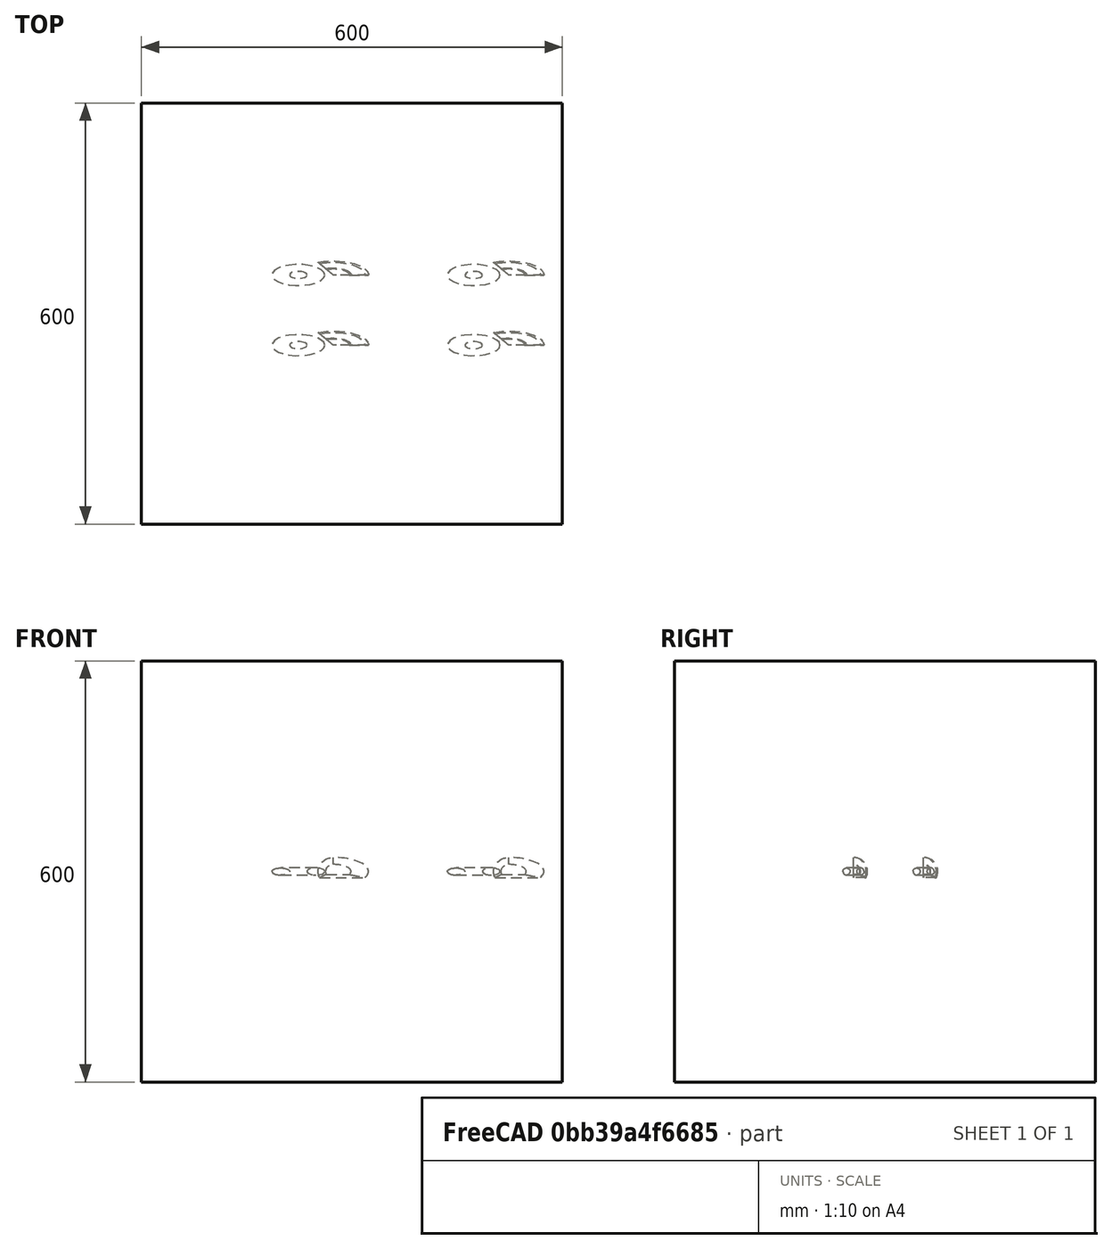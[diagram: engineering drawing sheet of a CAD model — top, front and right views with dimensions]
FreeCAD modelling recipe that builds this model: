
FCSTD DOCUMENT  (FreeCAD 1.0R39109 (Git))
Label: arrayTest-6_scaled
License: All rights reserved
LicenseURL: http://en.wikipedia.org/wiki/All_rights_reserved
objects: App::DocumentObjectGroupPython×1248, Part::FeaturePython×5, App::Part×2, Part::MultiFuse×1
note: 6 computed .brp shape members not serialized (recipe doc carries the construction recipe); baked Part::Feature solids carry a one-line shape summary decoded from their .brp

FEATURE [App::DocumentObjectGroupPython] HALFPI  # scripted group (container) (typed FeaturePython)
  name = HALFPI
  value = pi/2.
FEATURE [App::DocumentObjectGroupPython] PI  # scripted group (container) (typed FeaturePython)
  name = PI
  value = 1.*pi
FEATURE [App::DocumentObjectGroupPython] TWOPI  # scripted group (container) (typed FeaturePython)
  name = TWOPI
  value = 2.*pi
FEATURE [App::DocumentObjectGroupPython] Constants  # scripted group (container) (typed FeaturePython)
  Group = -> [HALFPI,PI,TWOPI]
FEATURE [App::DocumentObjectGroupPython] Variables  # scripted group (container) (typed FeaturePython)
FEATURE [App::DocumentObjectGroupPython] Quantities  # scripted group (container) (typed FeaturePython)
FEATURE [App::DocumentObjectGroupPython] Isotopes  # scripted group (container) (typed FeaturePython)
FEATURE [App::DocumentObjectGroupPython] Elements  # scripted group (container) (typed FeaturePython)
FEATURE [App::DocumentObjectGroupPython] G4Isotopes  # scripted group (container) (typed FeaturePython)
FEATURE [App::DocumentObjectGroupPython] H_element  # scripted group (container) (typed FeaturePython)
  Z = 1
  atom_value = 1.008
  formula = H
  name = H_element
FEATURE [App::DocumentObjectGroupPython] He_element  # scripted group (container) (typed FeaturePython)
  Z = 2
  atom_value = 4.0026
  formula = He
  name = He_element
FEATURE [App::DocumentObjectGroupPython] Li_element  # scripted group (container) (typed FeaturePython)
  Z = 3
  atom_value = 6.94
  formula = Li
  name = Li_element
FEATURE [App::DocumentObjectGroupPython] Be_element  # scripted group (container) (typed FeaturePython)
  Z = 4
  atom_value = 9.01218
  formula = Be
  name = Be_element
FEATURE [App::DocumentObjectGroupPython] B_element  # scripted group (container) (typed FeaturePython)
  Z = 5
  atom_value = 10.81
  formula = B
  name = B_element
FEATURE [App::DocumentObjectGroupPython] C_element  # scripted group (container) (typed FeaturePython)
  Z = 6
  atom_value = 12.011
  formula = C
  name = C_element
FEATURE [App::DocumentObjectGroupPython] N_element  # scripted group (container) (typed FeaturePython)
  Z = 7
  atom_value = 14.007
  formula = N
  name = N_element
FEATURE [App::DocumentObjectGroupPython] O_element  # scripted group (container) (typed FeaturePython)
  Z = 8
  atom_value = 15.999
  formula = O
  name = O_element
FEATURE [App::DocumentObjectGroupPython] F_element  # scripted group (container) (typed FeaturePython)
  Z = 9
  atom_value = 18.9984
  formula = F
  name = F_element
FEATURE [App::DocumentObjectGroupPython] Ne_element  # scripted group (container) (typed FeaturePython)
  Z = 10
  atom_value = 20.1797
  formula = Ne
  name = Ne_element
FEATURE [App::DocumentObjectGroupPython] Na_element  # scripted group (container) (typed FeaturePython)
  Z = 11
  atom_value = 22.9898
  formula = Na
  name = Na_element
FEATURE [App::DocumentObjectGroupPython] Mg_element  # scripted group (container) (typed FeaturePython)
  Z = 12
  atom_value = 24.305
  formula = Mg
  name = Mg_element
FEATURE [App::DocumentObjectGroupPython] Al_element  # scripted group (container) (typed FeaturePython)
  Z = 13
  atom_value = 26.9815
  formula = Al
  name = Al_element
FEATURE [App::DocumentObjectGroupPython] Si_element  # scripted group (container) (typed FeaturePython)
  Z = 14
  atom_value = 28.085
  formula = Si
  name = Si_element
FEATURE [App::DocumentObjectGroupPython] P_element  # scripted group (container) (typed FeaturePython)
  Z = 15
  atom_value = 30.9738
  formula = P
  name = P_element
FEATURE [App::DocumentObjectGroupPython] S_element  # scripted group (container) (typed FeaturePython)
  Z = 16
  atom_value = 32.06
  formula = S
  name = S_element
FEATURE [App::DocumentObjectGroupPython] Cl_element  # scripted group (container) (typed FeaturePython)
  Z = 17
  atom_value = 35.45
  formula = Cl
  name = Cl_element
FEATURE [App::DocumentObjectGroupPython] Ar_element  # scripted group (container) (typed FeaturePython)
  Z = 18
  atom_value = 39.95
  formula = Ar
  name = Ar_element
FEATURE [App::DocumentObjectGroupPython] K_element  # scripted group (container) (typed FeaturePython)
  Z = 19
  atom_value = 39.0983
  formula = K
  name = K_element
FEATURE [App::DocumentObjectGroupPython] Ca_element  # scripted group (container) (typed FeaturePython)
  Z = 20
  atom_value = 40.078
  formula = Ca
  name = Ca_element
FEATURE [App::DocumentObjectGroupPython] Sc_element  # scripted group (container) (typed FeaturePython)
  Z = 21
  atom_value = 44.9559
  formula = Sc
  name = Sc_element
FEATURE [App::DocumentObjectGroupPython] Ti_element  # scripted group (container) (typed FeaturePython)
  Z = 22
  atom_value = 47.867
  formula = Ti
  name = Ti_element
FEATURE [App::DocumentObjectGroupPython] V_element  # scripted group (container) (typed FeaturePython)
  Z = 23
  atom_value = 50.9415
  formula = V
  name = V_element
FEATURE [App::DocumentObjectGroupPython] Cr_element  # scripted group (container) (typed FeaturePython)
  Z = 24
  atom_value = 51.9961
  formula = Cr
  name = Cr_element
FEATURE [App::DocumentObjectGroupPython] Mn_element  # scripted group (container) (typed FeaturePython)
  Z = 25
  atom_value = 54.938
  formula = Mn
  name = Mn_element
FEATURE [App::DocumentObjectGroupPython] Fe_element  # scripted group (container) (typed FeaturePython)
  Z = 26
  atom_value = 55.845
  formula = Fe
  name = Fe_element
FEATURE [App::DocumentObjectGroupPython] Co_element  # scripted group (container) (typed FeaturePython)
  Z = 27
  atom_value = 58.9332
  formula = Co
  name = Co_element
FEATURE [App::DocumentObjectGroupPython] Ni_element  # scripted group (container) (typed FeaturePython)
  Z = 28
  atom_value = 58.6934
  formula = Ni
  name = Ni_element
FEATURE [App::DocumentObjectGroupPython] Cu_element  # scripted group (container) (typed FeaturePython)
  Z = 29
  atom_value = 63.546
  formula = Cu
  name = Cu_element
FEATURE [App::DocumentObjectGroupPython] Zn_element  # scripted group (container) (typed FeaturePython)
  Z = 30
  atom_value = 65.38
  formula = Zn
  name = Zn_element
FEATURE [App::DocumentObjectGroupPython] Ga_element  # scripted group (container) (typed FeaturePython)
  Z = 31
  atom_value = 69.723
  formula = Ga
  name = Ga_element
FEATURE [App::DocumentObjectGroupPython] Ge_element  # scripted group (container) (typed FeaturePython)
  Z = 32
  atom_value = 72.63
  formula = Ge
  name = Ge_element
FEATURE [App::DocumentObjectGroupPython] As_element  # scripted group (container) (typed FeaturePython)
  Z = 33
  atom_value = 74.9216
  formula = As
  name = As_element
FEATURE [App::DocumentObjectGroupPython] Se_element  # scripted group (container) (typed FeaturePython)
  Z = 34
  atom_value = 78.971
  formula = Se
  name = Se_element
FEATURE [App::DocumentObjectGroupPython] Br_element  # scripted group (container) (typed FeaturePython)
  Z = 35
  atom_value = 79.904
  formula = Br
  name = Br_element
FEATURE [App::DocumentObjectGroupPython] Kr_element  # scripted group (container) (typed FeaturePython)
  Z = 36
  atom_value = 83.798
  formula = Kr
  name = Kr_element
FEATURE [App::DocumentObjectGroupPython] Rb_element  # scripted group (container) (typed FeaturePython)
  Z = 37
  atom_value = 85.4678
  formula = Rb
  name = Rb_element
FEATURE [App::DocumentObjectGroupPython] Sr_element  # scripted group (container) (typed FeaturePython)
  Z = 38
  atom_value = 87.62
  formula = Sr
  name = Sr_element
FEATURE [App::DocumentObjectGroupPython] Y_element  # scripted group (container) (typed FeaturePython)
  Z = 39
  atom_value = 88.9058
  formula = Y
  name = Y_element
FEATURE [App::DocumentObjectGroupPython] Zr_element  # scripted group (container) (typed FeaturePython)
  Z = 40
  atom_value = 91.224
  formula = Zr
  name = Zr_element
FEATURE [App::DocumentObjectGroupPython] Nb_element  # scripted group (container) (typed FeaturePython)
  Z = 41
  atom_value = 92.9064
  formula = Nb
  name = Nb_element
FEATURE [App::DocumentObjectGroupPython] Mo_element  # scripted group (container) (typed FeaturePython)
  Z = 42
  atom_value = 95.95
  formula = Mo
  name = Mo_element
FEATURE [App::DocumentObjectGroupPython] Tc_element  # scripted group (container) (typed FeaturePython)
  Z = 43
  atom_value = 97
  formula = Tc
  name = Tc_element
FEATURE [App::DocumentObjectGroupPython] Ru_element  # scripted group (container) (typed FeaturePython)
  Z = 44
  atom_value = 101.07
  formula = Ru
  name = Ru_element
FEATURE [App::DocumentObjectGroupPython] Rh_element  # scripted group (container) (typed FeaturePython)
  Z = 45
  atom_value = 102.905
  formula = Rh
  name = Rh_element
FEATURE [App::DocumentObjectGroupPython] Pd_element  # scripted group (container) (typed FeaturePython)
  Z = 46
  atom_value = 106.42
  formula = Pd
  name = Pd_element
FEATURE [App::DocumentObjectGroupPython] Ag_element  # scripted group (container) (typed FeaturePython)
  Z = 47
  atom_value = 107.868
  formula = Ag
  name = Ag_element
FEATURE [App::DocumentObjectGroupPython] Cd_element  # scripted group (container) (typed FeaturePython)
  Z = 48
  atom_value = 112.414
  formula = Cd
  name = Cd_element
FEATURE [App::DocumentObjectGroupPython] In_element  # scripted group (container) (typed FeaturePython)
  Z = 49
  atom_value = 114.818
  formula = In
  name = In_element
FEATURE [App::DocumentObjectGroupPython] Sn_element  # scripted group (container) (typed FeaturePython)
  Z = 50
  atom_value = 118.71
  formula = Sn
  name = Sn_element
FEATURE [App::DocumentObjectGroupPython] Sb_element  # scripted group (container) (typed FeaturePython)
  Z = 51
  atom_value = 121.76
  formula = Sb
  name = Sb_element
FEATURE [App::DocumentObjectGroupPython] Te_element  # scripted group (container) (typed FeaturePython)
  Z = 52
  atom_value = 127.6
  formula = Te
  name = Te_element
FEATURE [App::DocumentObjectGroupPython] I_element  # scripted group (container) (typed FeaturePython)
  Z = 53
  atom_value = 126.904
  formula = I
  name = I_element
FEATURE [App::DocumentObjectGroupPython] Xe_element  # scripted group (container) (typed FeaturePython)
  Z = 54
  atom_value = 131.293
  formula = Xe
  name = Xe_element
FEATURE [App::DocumentObjectGroupPython] Cs_element  # scripted group (container) (typed FeaturePython)
  Z = 55
  atom_value = 132.905
  formula = Cs
  name = Cs_element
FEATURE [App::DocumentObjectGroupPython] Ba_element  # scripted group (container) (typed FeaturePython)
  Z = 56
  atom_value = 137.327
  formula = Ba
  name = Ba_element
FEATURE [App::DocumentObjectGroupPython] La_element  # scripted group (container) (typed FeaturePython)
  Z = 57
  atom_value = 138.905
  formula = La
  name = La_element
FEATURE [App::DocumentObjectGroupPython] Ce_element  # scripted group (container) (typed FeaturePython)
  Z = 58
  atom_value = 140.116
  formula = Ce
  name = Ce_element
FEATURE [App::DocumentObjectGroupPython] Pr_element  # scripted group (container) (typed FeaturePython)
  Z = 59
  atom_value = 140.908
  formula = Pr
  name = Pr_element
FEATURE [App::DocumentObjectGroupPython] Nd_element  # scripted group (container) (typed FeaturePython)
  Z = 60
  atom_value = 144.242
  formula = Nd
  name = Nd_element
FEATURE [App::DocumentObjectGroupPython] Pm_element  # scripted group (container) (typed FeaturePython)
  Z = 61
  atom_value = 145
  formula = Pm
  name = Pm_element
FEATURE [App::DocumentObjectGroupPython] Sm_element  # scripted group (container) (typed FeaturePython)
  Z = 62
  atom_value = 150.36
  formula = Sm
  name = Sm_element
FEATURE [App::DocumentObjectGroupPython] Eu_element  # scripted group (container) (typed FeaturePython)
  Z = 63
  atom_value = 151.964
  formula = Eu
  name = Eu_element
FEATURE [App::DocumentObjectGroupPython] Gd_element  # scripted group (container) (typed FeaturePython)
  Z = 64
  atom_value = 157.25
  formula = Gd
  name = Gd_element
FEATURE [App::DocumentObjectGroupPython] Tb_element  # scripted group (container) (typed FeaturePython)
  Z = 65
  atom_value = 158.925
  formula = Tb
  name = Tb_element
FEATURE [App::DocumentObjectGroupPython] Dy_element  # scripted group (container) (typed FeaturePython)
  Z = 66
  atom_value = 162.5
  formula = Dy
  name = Dy_element
FEATURE [App::DocumentObjectGroupPython] Ho_element  # scripted group (container) (typed FeaturePython)
  Z = 67
  atom_value = 164.93
  formula = Ho
  name = Ho_element
FEATURE [App::DocumentObjectGroupPython] Er_element  # scripted group (container) (typed FeaturePython)
  Z = 68
  atom_value = 167.259
  formula = Er
  name = Er_element
FEATURE [App::DocumentObjectGroupPython] Tm_element  # scripted group (container) (typed FeaturePython)
  Z = 69
  atom_value = 168.934
  formula = Tm
  name = Tm_element
FEATURE [App::DocumentObjectGroupPython] Yb_element  # scripted group (container) (typed FeaturePython)
  Z = 70
  atom_value = 173.045
  formula = Yb
  name = Yb_element
FEATURE [App::DocumentObjectGroupPython] Lu_element  # scripted group (container) (typed FeaturePython)
  Z = 71
  atom_value = 174.967
  formula = Lu
  name = Lu_element
FEATURE [App::DocumentObjectGroupPython] Hf_element  # scripted group (container) (typed FeaturePython)
  Z = 72
  atom_value = 178.49
  formula = Hf
  name = Hf_element
FEATURE [App::DocumentObjectGroupPython] Ta_element  # scripted group (container) (typed FeaturePython)
  Z = 73
  atom_value = 180.948
  formula = Ta
  name = Ta_element
FEATURE [App::DocumentObjectGroupPython] W_element  # scripted group (container) (typed FeaturePython)
  Z = 74
  atom_value = 183.84
  formula = W
  name = W_element
FEATURE [App::DocumentObjectGroupPython] Re_element  # scripted group (container) (typed FeaturePython)
  Z = 75
  atom_value = 186.207
  formula = Re
  name = Re_element
FEATURE [App::DocumentObjectGroupPython] Os_element  # scripted group (container) (typed FeaturePython)
  Z = 76
  atom_value = 190.23
  formula = Os
  name = Os_element
FEATURE [App::DocumentObjectGroupPython] Ir_element  # scripted group (container) (typed FeaturePython)
  Z = 77
  atom_value = 192.217
  formula = Ir
  name = Ir_element
FEATURE [App::DocumentObjectGroupPython] Pt_element  # scripted group (container) (typed FeaturePython)
  Z = 78
  atom_value = 195.084
  formula = Pt
  name = Pt_element
FEATURE [App::DocumentObjectGroupPython] Au_element  # scripted group (container) (typed FeaturePython)
  Z = 79
  atom_value = 196.967
  formula = Au
  name = Au_element
FEATURE [App::DocumentObjectGroupPython] Hg_element  # scripted group (container) (typed FeaturePython)
  Z = 80
  atom_value = 200.592
  formula = Hg
  name = Hg_element
FEATURE [App::DocumentObjectGroupPython] Tl_element  # scripted group (container) (typed FeaturePython)
  Z = 81
  atom_value = 204.38
  formula = Tl
  name = Tl_element
FEATURE [App::DocumentObjectGroupPython] Pb_element  # scripted group (container) (typed FeaturePython)
  Z = 82
  atom_value = 207.2
  formula = Pb
  name = Pb_element
FEATURE [App::DocumentObjectGroupPython] Bi_element  # scripted group (container) (typed FeaturePython)
  Z = 83
  atom_value = 208.98
  formula = Bi
  name = Bi_element
FEATURE [App::DocumentObjectGroupPython] Po_element  # scripted group (container) (typed FeaturePython)
  Z = 84
  atom_value = 209
  formula = Po
  name = Po_element
FEATURE [App::DocumentObjectGroupPython] At_element  # scripted group (container) (typed FeaturePython)
  Z = 85
  atom_value = 210
  formula = At
  name = At_element
FEATURE [App::DocumentObjectGroupPython] Rn_element  # scripted group (container) (typed FeaturePython)
  Z = 86
  atom_value = 222
  formula = Rn
  name = Rn_element
FEATURE [App::DocumentObjectGroupPython] Fr_element  # scripted group (container) (typed FeaturePython)
  Z = 87
  atom_value = 223
  formula = Fr
  name = Fr_element
FEATURE [App::DocumentObjectGroupPython] Ra_element  # scripted group (container) (typed FeaturePython)
  Z = 88
  atom_value = 226
  formula = Ra
  name = Ra_element
FEATURE [App::DocumentObjectGroupPython] Ac_element  # scripted group (container) (typed FeaturePython)
  Z = 89
  atom_value = 227
  formula = Ac
  name = Ac_element
FEATURE [App::DocumentObjectGroupPython] Th_element  # scripted group (container) (typed FeaturePython)
  Z = 90
  atom_value = 232.038
  formula = Th
  name = Th_element
FEATURE [App::DocumentObjectGroupPython] Pa_element  # scripted group (container) (typed FeaturePython)
  Z = 91
  atom_value = 231.036
  formula = Pa
  name = Pa_element
FEATURE [App::DocumentObjectGroupPython] U_element  # scripted group (container) (typed FeaturePython)
  Z = 92
  atom_value = 238.029
  formula = U
  name = U_element
FEATURE [App::DocumentObjectGroupPython] Np_element  # scripted group (container) (typed FeaturePython)
  Z = 93
  atom_value = 237
  formula = Np
  name = Np_element
FEATURE [App::DocumentObjectGroupPython] Pu_element  # scripted group (container) (typed FeaturePython)
  Z = 94
  atom_value = 244
  formula = Pu
  name = Pu_element
FEATURE [App::DocumentObjectGroupPython] Am_element  # scripted group (container) (typed FeaturePython)
  Z = 95
  atom_value = 243
  formula = Am
  name = Am_element
FEATURE [App::DocumentObjectGroupPython] Cm_element  # scripted group (container) (typed FeaturePython)
  Z = 96
  atom_value = 247
  formula = Cm
  name = Cm_element
FEATURE [App::DocumentObjectGroupPython] Bk_element  # scripted group (container) (typed FeaturePython)
  Z = 97
  atom_value = 247
  formula = Bk
  name = Bk_element
FEATURE [App::DocumentObjectGroupPython] Cf_element  # scripted group (container) (typed FeaturePython)
  Z = 98
  atom_value = 251
  formula = Cf
  name = Cf_element
FEATURE [App::DocumentObjectGroupPython] G4Elements  # scripted group (container) (typed FeaturePython)
  Group = -> [H_element,He_element,Li_element,Be_element,B_element,C_element,N_element,O_element,F_element,Ne_element,Na_element,Mg_element,Al_element,Si_element,P_element,S_element,Cl_element,Ar_element,K_element,Ca_element,Sc_element,Ti_element,V_element,Cr_element,Mn_element,Fe_element,Co_element,Ni_element,Cu_element,Zn_element,Ga_element,Ge_element,As_element,Se_element,Br_element,Kr_element,Rb_element,+61 more]
FEATURE [App::DocumentObjectGroupPython] H_element001  label="H_element : 0.101"  # scripted group (container) (typed FeaturePython)
  n = 0.101327
FEATURE [App::DocumentObjectGroupPython] C_element001  label="C_element : 0.775"  # scripted group (container) (typed FeaturePython)
  n = 0.7755
FEATURE [App::DocumentObjectGroupPython] N_element001  label="N_element : 0.035"  # scripted group (container) (typed FeaturePython)
  n = 0.035057
FEATURE [App::DocumentObjectGroupPython] O_element001  label="O_element : 0.052"  # scripted group (container) (typed FeaturePython)
  n = 0.0523159
FEATURE [App::DocumentObjectGroupPython] F_element001  label="F_element : 0.017"  # scripted group (container) (typed FeaturePython)
  n = 0.017422
FEATURE [App::DocumentObjectGroupPython] Ca_element001  label="Ca_element : 0.018"  # scripted group (container) (typed FeaturePython)
  n = 0.018378
FEATURE [App::DocumentObjectGroupPython] G4_A_150_TISSUE  label="G4_A-150_TISSUE"  # scripted group (container) (typed FeaturePython)
  Dunit = g/cm3
  Dvalue = 1.127
  Group = -> [H_element001,C_element001,N_element001,O_element001,F_element001,Ca_element001]
  conduct = 2
  density = 1
  expand = 3
  formula = G4_A-150_TISSUE
  name = G4_A-150_TISSUE
  specific = 4
FEATURE [App::DocumentObjectGroupPython] C_element002  label="C_element : 3"  # scripted group (container) (typed FeaturePython)
  n = 3
  ref = C_element
FEATURE [App::DocumentObjectGroupPython] H_element002  label="H_element : 6"  # scripted group (container) (typed FeaturePython)
  n = 6
  ref = H_element
FEATURE [App::DocumentObjectGroupPython] O_element002  label="O_element : 1"  # scripted group (container) (typed FeaturePython)
  n = 1
  ref = O_element
FEATURE [App::DocumentObjectGroupPython] G4_ACETONE  # scripted group (container) (typed FeaturePython)
  Dunit = g/cm3
  Dvalue = 0.7899
  Group = -> [C_element002,H_element002,O_element002]
  conduct = 2
  density = 1
  expand = 3
  formula = G4_ACETONE
  name = G4_ACETONE
  specific = 4
FEATURE [App::DocumentObjectGroupPython] C_element003  label="C_element : 2"  # scripted group (container) (typed FeaturePython)
  n = 2
  ref = C_element
FEATURE [App::DocumentObjectGroupPython] H_element003  label="H_element : 2"  # scripted group (container) (typed FeaturePython)
  n = 2
  ref = H_element
FEATURE [App::DocumentObjectGroupPython] G4_ACETYLENE  # scripted group (container) (typed FeaturePython)
  Dunit = g/cm3
  Dvalue = 0.0010967
  Group = -> [C_element003,H_element003]
  conduct = 2
  density = 1
  expand = 3
  formula = G4_ACETYLENE
  name = G4_ACETYLENE
  specific = 4
FEATURE [App::DocumentObjectGroupPython] C_element004  label="C_element : 5"  # scripted group (container) (typed FeaturePython)
  n = 5
  ref = C_element
FEATURE [App::DocumentObjectGroupPython] H_element004  label="H_element : 5"  # scripted group (container) (typed FeaturePython)
  n = 5
  ref = H_element
FEATURE [App::DocumentObjectGroupPython] N_element002  label="N_element : 5"  # scripted group (container) (typed FeaturePython)
  n = 5
  ref = N_element
FEATURE [App::DocumentObjectGroupPython] G4_ADENINE  # scripted group (container) (typed FeaturePython)
  Dunit = g/cm3
  Dvalue = 1.6
  Group = -> [C_element004,H_element004,N_element002]
  conduct = 2
  density = 1
  expand = 3
  formula = G4_ADENINE
  name = G4_ADENINE
  specific = 4
FEATURE [App::DocumentObjectGroupPython] H_element005  label="H_element : 0.114"  # scripted group (container) (typed FeaturePython)
  n = 0.114
FEATURE [App::DocumentObjectGroupPython] C_element005  label="C_element : 0.598"  # scripted group (container) (typed FeaturePython)
  n = 0.598
FEATURE [App::DocumentObjectGroupPython] N_element003  label="N_element : 0.007"  # scripted group (container) (typed FeaturePython)
  n = 0.007
FEATURE [App::DocumentObjectGroupPython] O_element003  label="O_element : 0.278"  # scripted group (container) (typed FeaturePython)
  n = 0.278
FEATURE [App::DocumentObjectGroupPython] Na_element001  label="Na_element : 0.001"  # scripted group (container) (typed FeaturePython)
  n = 0.001
FEATURE [App::DocumentObjectGroupPython] S_element001  label="S_element : 0.001"  # scripted group (container) (typed FeaturePython)
  n = 0.001
FEATURE [App::DocumentObjectGroupPython] Cl_element001  label="Cl_element : 0.001"  # scripted group (container) (typed FeaturePython)
  n = 0.001
FEATURE [App::DocumentObjectGroupPython] G4_ADIPOSE_TISSUE_ICRP  # scripted group (container) (typed FeaturePython)
  Dunit = g/cm3
  Dvalue = 0.95
  Group = -> [H_element005,C_element005,N_element003,O_element003,Na_element001,S_element001,Cl_element001]
  conduct = 2
  density = 1
  expand = 3
  formula = G4_ADIPOSE_TISSUE_ICRP
  name = G4_ADIPOSE_TISSUE_ICRP
  specific = 4
FEATURE [App::DocumentObjectGroupPython] C_element006  label="C_element : 0.000"  # scripted group (container) (typed FeaturePython)
  n = 0.000124
FEATURE [App::DocumentObjectGroupPython] N_element004  label="N_element : 0.755"  # scripted group (container) (typed FeaturePython)
  n = 0.755268
FEATURE [App::DocumentObjectGroupPython] O_element004  label="O_element : 0.232"  # scripted group (container) (typed FeaturePython)
  n = 0.231781
FEATURE [App::DocumentObjectGroupPython] Ar_element001  label="Ar_element : 0.013"  # scripted group (container) (typed FeaturePython)
  n = 0.012827
FEATURE [App::DocumentObjectGroupPython] G4_AIR  # scripted group (container) (typed FeaturePython)
  Dunit = g/cm3
  Dvalue = 0.00120479
  Group = -> [C_element006,N_element004,O_element004,Ar_element001]
  conduct = 2
  density = 1
  expand = 3
  formula = G4_AIR
  name = G4_AIR
  specific = 4
FEATURE [App::DocumentObjectGroupPython] C_element007  label="C_element : 006"  # scripted group (container) (typed FeaturePython)
  n = 3
  ref = C_element
FEATURE [App::DocumentObjectGroupPython] H_element006  label="H_element : 7"  # scripted group (container) (typed FeaturePython)
  n = 7
  ref = H_element
FEATURE [App::DocumentObjectGroupPython] N_element005  label="N_element : 1"  # scripted group (container) (typed FeaturePython)
  n = 1
  ref = N_element
FEATURE [App::DocumentObjectGroupPython] O_element005  label="O_element : 2"  # scripted group (container) (typed FeaturePython)
  n = 2
  ref = O_element
FEATURE [App::DocumentObjectGroupPython] G4_ALANINE  # scripted group (container) (typed FeaturePython)
  Dunit = g/cm3
  Dvalue = 1.42
  Group = -> [C_element007,H_element006,N_element005,O_element005]
  conduct = 2
  density = 1
  expand = 3
  formula = G4_ALANINE
  name = G4_ALANINE
  specific = 4
FEATURE [App::DocumentObjectGroupPython] Al_element001  label="Al_element : 2"  # scripted group (container) (typed FeaturePython)
  n = 2
  ref = Al_element
FEATURE [App::DocumentObjectGroupPython] O_element006  label="O_element : 3"  # scripted group (container) (typed FeaturePython)
  n = 3
  ref = O_element
FEATURE [App::DocumentObjectGroupPython] G4_ALUMINUM_OXIDE  # scripted group (container) (typed FeaturePython)
  Dunit = g/cm3
  Dvalue = 3.97
  Group = -> [Al_element001,O_element006]
  conduct = 2
  density = 1
  expand = 3
  formula = G4_ALUMINUM_OXIDE
  name = G4_ALUMINUM_OXIDE
  specific = 4
FEATURE [App::DocumentObjectGroupPython] H_element007  label="H_element : 0.106"  # scripted group (container) (typed FeaturePython)
  n = 0.10593
FEATURE [App::DocumentObjectGroupPython] C_element008  label="C_element : 0.789"  # scripted group (container) (typed FeaturePython)
  n = 0.788974
FEATURE [App::DocumentObjectGroupPython] O_element007  label="O_element : 0.105"  # scripted group (container) (typed FeaturePython)
  n = 0.105096
FEATURE [App::DocumentObjectGroupPython] G4_AMBER  # scripted group (container) (typed FeaturePython)
  Dunit = g/cm3
  Dvalue = 1.1
  Group = -> [H_element007,C_element008,O_element007]
  conduct = 2
  density = 1
  expand = 3
  formula = G4_AMBER
  name = G4_AMBER
  specific = 4
FEATURE [App::DocumentObjectGroupPython] N_element006  label="N_element : 006"  # scripted group (container) (typed FeaturePython)
  n = 1
  ref = N_element
FEATURE [App::DocumentObjectGroupPython] H_element008  label="H_element : 3"  # scripted group (container) (typed FeaturePython)
  n = 3
  ref = H_element
FEATURE [App::DocumentObjectGroupPython] G4_AMMONIA  # scripted group (container) (typed FeaturePython)
  Dunit = g/cm3
  Dvalue = 0.000826019
  Group = -> [N_element006,H_element008]
  conduct = 2
  density = 1
  expand = 3
  formula = G4_AMMONIA
  name = G4_AMMONIA
  specific = 4
FEATURE [App::DocumentObjectGroupPython] C_element009  label="C_element : 6"  # scripted group (container) (typed FeaturePython)
  n = 6
  ref = C_element
FEATURE [App::DocumentObjectGroupPython] H_element009  label="H_element : 008"  # scripted group (container) (typed FeaturePython)
  n = 7
  ref = H_element
FEATURE [App::DocumentObjectGroupPython] N_element007  label="N_element : 007"  # scripted group (container) (typed FeaturePython)
  n = 1
  ref = N_element
FEATURE [App::DocumentObjectGroupPython] G4_ANILINE  # scripted group (container) (typed FeaturePython)
  Dunit = g/cm3
  Dvalue = 1.0235
  Group = -> [C_element009,H_element009,N_element007]
  conduct = 2
  density = 1
  expand = 3
  formula = G4_ANILINE
  name = G4_ANILINE
  specific = 4
FEATURE [App::DocumentObjectGroupPython] C_element010  label="C_element : 14"  # scripted group (container) (typed FeaturePython)
  n = 14
  ref = C_element
FEATURE [App::DocumentObjectGroupPython] H_element010  label="H_element : 10"  # scripted group (container) (typed FeaturePython)
  n = 10
  ref = H_element
FEATURE [App::DocumentObjectGroupPython] G4_ANTHRACENE  # scripted group (container) (typed FeaturePython)
  Dunit = g/cm3
  Dvalue = 1.283
  Group = -> [C_element010,H_element010]
  conduct = 2
  density = 1
  expand = 3
  formula = G4_ANTHRACENE
  name = G4_ANTHRACENE
  specific = 4
FEATURE [App::DocumentObjectGroupPython] H_element011  label="H_element : 0.065"  # scripted group (container) (typed FeaturePython)
  n = 0.0654709
FEATURE [App::DocumentObjectGroupPython] C_element011  label="C_element : 0.537"  # scripted group (container) (typed FeaturePython)
  n = 0.536944
FEATURE [App::DocumentObjectGroupPython] N_element008  label="N_element : 0.021"  # scripted group (container) (typed FeaturePython)
  n = 0.0215
FEATURE [App::DocumentObjectGroupPython] O_element008  label="O_element : 0.032"  # scripted group (container) (typed FeaturePython)
  n = 0.032085
FEATURE [App::DocumentObjectGroupPython] F_element002  label="F_element : 0.167"  # scripted group (container) (typed FeaturePython)
  n = 0.167411
FEATURE [App::DocumentObjectGroupPython] Ca_element002  label="Ca_element : 0.177"  # scripted group (container) (typed FeaturePython)
  n = 0.176589
FEATURE [App::DocumentObjectGroupPython] G4_B_100_BONE  label="G4_B-100_BONE"  # scripted group (container) (typed FeaturePython)
  Dunit = g/cm3
  Dvalue = 1.45
  Group = -> [H_element011,C_element011,N_element008,O_element008,F_element002,Ca_element002]
  conduct = 2
  density = 1
  expand = 3
  formula = G4_B-100_BONE
  name = G4_B-100_BONE
  specific = 4
FEATURE [App::DocumentObjectGroupPython] H_element012  label="H_element : 0.057"  # scripted group (container) (typed FeaturePython)
  n = 0.057441
FEATURE [App::DocumentObjectGroupPython] C_element012  label="C_element : 0.790"  # scripted group (container) (typed FeaturePython)
  n = 0.774591
FEATURE [App::DocumentObjectGroupPython] O_element009  label="O_element : 0.168"  # scripted group (container) (typed FeaturePython)
  n = 0.167968
FEATURE [App::DocumentObjectGroupPython] G4_BAKELITE  # scripted group (container) (typed FeaturePython)
  Dunit = g/cm3
  Dvalue = 1.25
  Group = -> [H_element012,C_element012,O_element009]
  conduct = 2
  density = 1
  expand = 3
  formula = G4_BAKELITE
  name = G4_BAKELITE
  specific = 4
FEATURE [App::DocumentObjectGroupPython] Ba_element001  label="Ba_element : 1"  # scripted group (container) (typed FeaturePython)
  n = 1
  ref = Ba_element
FEATURE [App::DocumentObjectGroupPython] F_element003  label="F_element : 2"  # scripted group (container) (typed FeaturePython)
  n = 2
  ref = F_element
FEATURE [App::DocumentObjectGroupPython] G4_BARIUM_FLUORIDE  # scripted group (container) (typed FeaturePython)
  Dunit = g/cm3
  Dvalue = 4.89
  Group = -> [Ba_element001,F_element003]
  conduct = 2
  density = 1
  expand = 3
  formula = G4_BARIUM_FLUORIDE
  name = G4_BARIUM_FLUORIDE
  specific = 4
FEATURE [App::DocumentObjectGroupPython] Ba_element002  label="Ba_element : 002"  # scripted group (container) (typed FeaturePython)
  n = 1
  ref = Ba_element
FEATURE [App::DocumentObjectGroupPython] S_element002  label="S_element : 1"  # scripted group (container) (typed FeaturePython)
  n = 1
  ref = S_element
FEATURE [App::DocumentObjectGroupPython] O_element010  label="O_element : 4"  # scripted group (container) (typed FeaturePython)
  n = 4
  ref = O_element
FEATURE [App::DocumentObjectGroupPython] G4_BARIUM_SULFATE  # scripted group (container) (typed FeaturePython)
  Dunit = g/cm3
  Dvalue = 4.5
  Group = -> [Ba_element002,S_element002,O_element010]
  conduct = 2
  density = 1
  expand = 3
  formula = G4_BARIUM_SULFATE
  name = G4_BARIUM_SULFATE
  specific = 4
FEATURE [App::DocumentObjectGroupPython] C_element013  label="C_element : 007"  # scripted group (container) (typed FeaturePython)
  n = 6
  ref = C_element
FEATURE [App::DocumentObjectGroupPython] H_element013  label="H_element : 009"  # scripted group (container) (typed FeaturePython)
  n = 6
  ref = H_element
FEATURE [App::DocumentObjectGroupPython] G4_BENZENE  # scripted group (container) (typed FeaturePython)
  Dunit = g/cm3
  Dvalue = 0.87865
  Group = -> [C_element013,H_element013]
  conduct = 2
  density = 1
  expand = 3
  formula = G4_BENZENE
  name = G4_BENZENE
  specific = 4
FEATURE [App::DocumentObjectGroupPython] Be_element001  label="Be_element : 1"  # scripted group (container) (typed FeaturePython)
  n = 1
  ref = Be_element
FEATURE [App::DocumentObjectGroupPython] O_element011  label="O_element : 005"  # scripted group (container) (typed FeaturePython)
  n = 1
  ref = O_element
FEATURE [App::DocumentObjectGroupPython] G4_BERYLLIUM_OXIDE  # scripted group (container) (typed FeaturePython)
  Dunit = g/cm3
  Dvalue = 3.01
  Group = -> [Be_element001,O_element011]
  conduct = 2
  density = 1
  expand = 3
  formula = G4_BERYLLIUM_OXIDE
  name = G4_BERYLLIUM_OXIDE
  specific = 4
FEATURE [App::DocumentObjectGroupPython] Bi_element001  label="Bi_element : 4"  # scripted group (container) (typed FeaturePython)
  n = 4
  ref = Bi_element
FEATURE [App::DocumentObjectGroupPython] Ge_element001  label="Ge_element : 3"  # scripted group (container) (typed FeaturePython)
  n = 3
  ref = Ge_element
FEATURE [App::DocumentObjectGroupPython] O_element012  label="O_element : 12"  # scripted group (container) (typed FeaturePython)
  n = 12
  ref = O_element
FEATURE [App::DocumentObjectGroupPython] G4_BGO  # scripted group (container) (typed FeaturePython)
  Dunit = g/cm3
  Dvalue = 7.13
  Group = -> [Bi_element001,Ge_element001,O_element012]
  conduct = 2
  density = 1
  expand = 3
  formula = G4_BGO
  name = G4_BGO
  specific = 4
FEATURE [App::DocumentObjectGroupPython] H_element014  label="H_element : 0.102"  # scripted group (container) (typed FeaturePython)
  n = 0.102
FEATURE [App::DocumentObjectGroupPython] C_element014  label="C_element : 0.110"  # scripted group (container) (typed FeaturePython)
  n = 0.11
FEATURE [App::DocumentObjectGroupPython] N_element009  label="N_element : 0.033"  # scripted group (container) (typed FeaturePython)
  n = 0.033
FEATURE [App::DocumentObjectGroupPython] O_element013  label="O_element : 0.745"  # scripted group (container) (typed FeaturePython)
  n = 0.745
FEATURE [App::DocumentObjectGroupPython] Na_element002  label="Na_element : 0.002"  # scripted group (container) (typed FeaturePython)
  n = 0.001
FEATURE [App::DocumentObjectGroupPython] P_element001  label="P_element : 0.001"  # scripted group (container) (typed FeaturePython)
  n = 0.001
FEATURE [App::DocumentObjectGroupPython] S_element003  label="S_element : 0.002"  # scripted group (container) (typed FeaturePython)
  n = 0.002
FEATURE [App::DocumentObjectGroupPython] Cl_element002  label="Cl_element : 0.003"  # scripted group (container) (typed FeaturePython)
  n = 0.003
FEATURE [App::DocumentObjectGroupPython] K_element001  label="K_element : 0.002"  # scripted group (container) (typed FeaturePython)
  n = 0.002
FEATURE [App::DocumentObjectGroupPython] Fe_element001  label="Fe_element : 0.001"  # scripted group (container) (typed FeaturePython)
  n = 0.001
FEATURE [App::DocumentObjectGroupPython] G4_BLOOD_ICRP  # scripted group (container) (typed FeaturePython)
  Dunit = g/cm3
  Dvalue = 1.06
  Group = -> [H_element014,C_element014,N_element009,O_element013,Na_element002,P_element001,S_element003,Cl_element002,K_element001,Fe_element001]
  conduct = 2
  density = 1
  expand = 3
  formula = G4_BLOOD_ICRP
  name = G4_BLOOD_ICRP
  specific = 4
FEATURE [App::DocumentObjectGroupPython] H_element015  label="H_element : 0.064"  # scripted group (container) (typed FeaturePython)
  n = 0.064
FEATURE [App::DocumentObjectGroupPython] C_element015  label="C_element : 0.278"  # scripted group (container) (typed FeaturePython)
  n = 0.278
FEATURE [App::DocumentObjectGroupPython] N_element010  label="N_element : 0.027"  # scripted group (container) (typed FeaturePython)
  n = 0.027
FEATURE [App::DocumentObjectGroupPython] O_element014  label="O_element : 0.410"  # scripted group (container) (typed FeaturePython)
  n = 0.41
FEATURE [App::DocumentObjectGroupPython] Mg_element001  label="Mg_element : 0.002"  # scripted group (container) (typed FeaturePython)
  n = 0.002
FEATURE [App::DocumentObjectGroupPython] P_element002  label="P_element : 0.070"  # scripted group (container) (typed FeaturePython)
  n = 0.07
FEATURE [App::DocumentObjectGroupPython] S_element004  label="S_element : 0.003"  # scripted group (container) (typed FeaturePython)
  n = 0.002
FEATURE [App::DocumentObjectGroupPython] Ca_element003  label="Ca_element : 0.147"  # scripted group (container) (typed FeaturePython)
  n = 0.147
FEATURE [App::DocumentObjectGroupPython] G4_BONE_COMPACT_ICRU  # scripted group (container) (typed FeaturePython)
  Dunit = g/cm3
  Dvalue = 1.85
  Group = -> [H_element015,C_element015,N_element010,O_element014,Mg_element001,P_element002,S_element004,Ca_element003]
  conduct = 2
  density = 1
  expand = 3
  formula = G4_BONE_COMPACT_ICRU
  name = G4_BONE_COMPACT_ICRU
  specific = 4
FEATURE [App::DocumentObjectGroupPython] H_element016  label="H_element : 0.034"  # scripted group (container) (typed FeaturePython)
  n = 0.034
FEATURE [App::DocumentObjectGroupPython] C_element016  label="C_element : 0.155"  # scripted group (container) (typed FeaturePython)
  n = 0.155
FEATURE [App::DocumentObjectGroupPython] N_element011  label="N_element : 0.042"  # scripted group (container) (typed FeaturePython)
  n = 0.042
FEATURE [App::DocumentObjectGroupPython] O_element015  label="O_element : 0.435"  # scripted group (container) (typed FeaturePython)
  n = 0.435
FEATURE [App::DocumentObjectGroupPython] Na_element003  label="Na_element : 0.003"  # scripted group (container) (typed FeaturePython)
  n = 0.001
FEATURE [App::DocumentObjectGroupPython] Mg_element002  label="Mg_element : 0.003"  # scripted group (container) (typed FeaturePython)
  n = 0.002
FEATURE [App::DocumentObjectGroupPython] P_element003  label="P_element : 0.103"  # scripted group (container) (typed FeaturePython)
  n = 0.103
FEATURE [App::DocumentObjectGroupPython] S_element005  label="S_element : 0.004"  # scripted group (container) (typed FeaturePython)
  n = 0.003
FEATURE [App::DocumentObjectGroupPython] Ca_element004  label="Ca_element : 0.225"  # scripted group (container) (typed FeaturePython)
  n = 0.225
FEATURE [App::DocumentObjectGroupPython] G4_BONE_CORTICAL_ICRP  # scripted group (container) (typed FeaturePython)
  Dunit = g/cm3
  Dvalue = 1.92
  Group = -> [H_element016,C_element016,N_element011,O_element015,Na_element003,Mg_element002,P_element003,S_element005,Ca_element004]
  conduct = 2
  density = 1
  expand = 3
  formula = G4_BONE_CORTICAL_ICRP
  name = G4_BONE_CORTICAL_ICRP
  specific = 4
FEATURE [App::DocumentObjectGroupPython] B_element001  label="B_element : 4"  # scripted group (container) (typed FeaturePython)
  n = 4
  ref = B_element
FEATURE [App::DocumentObjectGroupPython] C_element017  label="C_element : 1"  # scripted group (container) (typed FeaturePython)
  n = 1
  ref = C_element
FEATURE [App::DocumentObjectGroupPython] G4_BORON_CARBIDE  # scripted group (container) (typed FeaturePython)
  Dunit = g/cm3
  Dvalue = 2.52
  Group = -> [B_element001,C_element017]
  conduct = 2
  density = 1
  expand = 3
  formula = G4_BORON_CARBIDE
  name = G4_BORON_CARBIDE
  specific = 4
FEATURE [App::DocumentObjectGroupPython] B_element002  label="B_element : 2"  # scripted group (container) (typed FeaturePython)
  n = 2
  ref = B_element
FEATURE [App::DocumentObjectGroupPython] O_element016  label="O_element : 006"  # scripted group (container) (typed FeaturePython)
  n = 3
  ref = O_element
FEATURE [App::DocumentObjectGroupPython] G4_BORON_OXIDE  # scripted group (container) (typed FeaturePython)
  Dunit = g/cm3
  Dvalue = 1.812
  Group = -> [B_element002,O_element016]
  conduct = 2
  density = 1
  expand = 3
  formula = G4_BORON_OXIDE
  name = G4_BORON_OXIDE
  specific = 4
FEATURE [App::DocumentObjectGroupPython] H_element017  label="H_element : 0.107"  # scripted group (container) (typed FeaturePython)
  n = 0.107
FEATURE [App::DocumentObjectGroupPython] C_element018  label="C_element : 0.145"  # scripted group (container) (typed FeaturePython)
  n = 0.145
FEATURE [App::DocumentObjectGroupPython] N_element012  label="N_element : 0.022"  # scripted group (container) (typed FeaturePython)
  n = 0.022
FEATURE [App::DocumentObjectGroupPython] O_element017  label="O_element : 0.712"  # scripted group (container) (typed FeaturePython)
  n = 0.712
FEATURE [App::DocumentObjectGroupPython] Na_element004  label="Na_element : 0.004"  # scripted group (container) (typed FeaturePython)
  n = 0.002
FEATURE [App::DocumentObjectGroupPython] P_element004  label="P_element : 0.004"  # scripted group (container) (typed FeaturePython)
  n = 0.004
FEATURE [App::DocumentObjectGroupPython] S_element006  label="S_element : 0.005"  # scripted group (container) (typed FeaturePython)
  n = 0.002
FEATURE [App::DocumentObjectGroupPython] Cl_element003  label="Cl_element : 0.004"  # scripted group (container) (typed FeaturePython)
  n = 0.003
FEATURE [App::DocumentObjectGroupPython] K_element002  label="K_element : 0.003"  # scripted group (container) (typed FeaturePython)
  n = 0.003
FEATURE [App::DocumentObjectGroupPython] G4_BRAIN_ICRP  # scripted group (container) (typed FeaturePython)
  Dunit = g/cm3
  Dvalue = 1.04
  Group = -> [H_element017,C_element018,N_element012,O_element017,Na_element004,P_element004,S_element006,Cl_element003,K_element002]
  conduct = 2
  density = 1
  expand = 3
  formula = G4_BRAIN_ICRP
  name = G4_BRAIN_ICRP
  specific = 4
FEATURE [App::DocumentObjectGroupPython] C_element019  label="C_element : 4"  # scripted group (container) (typed FeaturePython)
  n = 4
  ref = C_element
FEATURE [App::DocumentObjectGroupPython] H_element018  label="H_element : 010"  # scripted group (container) (typed FeaturePython)
  n = 10
  ref = H_element
FEATURE [App::DocumentObjectGroupPython] G4_BUTANE  # scripted group (container) (typed FeaturePython)
  Dunit = g/cm3
  Dvalue = 0.00249343
  Group = -> [C_element019,H_element018]
  conduct = 2
  density = 1
  expand = 3
  formula = G4_BUTANE
  name = G4_BUTANE
  specific = 4
FEATURE [App::DocumentObjectGroupPython] C_element020  label="C_element : 008"  # scripted group (container) (typed FeaturePython)
  n = 4
  ref = C_element
FEATURE [App::DocumentObjectGroupPython] H_element019  label="H_element : 011"  # scripted group (container) (typed FeaturePython)
  n = 10
  ref = H_element
FEATURE [App::DocumentObjectGroupPython] O_element018  label="O_element : 007"  # scripted group (container) (typed FeaturePython)
  n = 1
  ref = O_element
FEATURE [App::DocumentObjectGroupPython] G4_N_BUTYL_ALCOHOL  label="G4_N-BUTYL_ALCOHOL"  # scripted group (container) (typed FeaturePython)
  Dunit = g/cm3
  Dvalue = 0.8098
  Group = -> [C_element020,H_element019,O_element018]
  conduct = 2
  density = 1
  expand = 3
  formula = G4_N-BUTYL_ALCOHOL
  name = G4_N-BUTYL_ALCOHOL
  specific = 4
FEATURE [App::DocumentObjectGroupPython] H_element020  label="H_element : 0.025"  # scripted group (container) (typed FeaturePython)
  n = 0.02468
FEATURE [App::DocumentObjectGroupPython] C_element021  label="C_element : 0.502"  # scripted group (container) (typed FeaturePython)
  n = 0.501611
FEATURE [App::DocumentObjectGroupPython] O_element019  label="O_element : 0.005"  # scripted group (container) (typed FeaturePython)
  n = 0.004527
FEATURE [App::DocumentObjectGroupPython] F_element004  label="F_element : 0.465"  # scripted group (container) (typed FeaturePython)
  n = 0.465209
FEATURE [App::DocumentObjectGroupPython] Si_element001  label="Si_element : 0.004"  # scripted group (container) (typed FeaturePython)
  n = 0.003973
FEATURE [App::DocumentObjectGroupPython] G4_C_552  label="G4_C-552"  # scripted group (container) (typed FeaturePython)
  Dunit = g/cm3
  Dvalue = 1.76
  Group = -> [H_element020,C_element021,O_element019,F_element004,Si_element001]
  conduct = 2
  density = 1
  expand = 3
  formula = G4_C-552
  name = G4_C-552
  specific = 4
FEATURE [App::DocumentObjectGroupPython] Cd_element001  label="Cd_element : 1"  # scripted group (container) (typed FeaturePython)
  n = 1
  ref = Cd_element
FEATURE [App::DocumentObjectGroupPython] Te_element001  label="Te_element : 1"  # scripted group (container) (typed FeaturePython)
  n = 1
  ref = Te_element
FEATURE [App::DocumentObjectGroupPython] G4_CADMIUM_TELLURIDE  # scripted group (container) (typed FeaturePython)
  Dunit = g/cm3
  Dvalue = 6.2
  Group = -> [Cd_element001,Te_element001]
  conduct = 2
  density = 1
  expand = 3
  formula = G4_CADMIUM_TELLURIDE
  name = G4_CADMIUM_TELLURIDE
  specific = 4
FEATURE [App::DocumentObjectGroupPython] Cd_element002  label="Cd_element : 002"  # scripted group (container) (typed FeaturePython)
  n = 1
  ref = Cd_element
FEATURE [App::DocumentObjectGroupPython] W_element001  label="W_element : 1"  # scripted group (container) (typed FeaturePython)
  n = 1
  ref = W_element
FEATURE [App::DocumentObjectGroupPython] O_element020  label="O_element : 008"  # scripted group (container) (typed FeaturePython)
  n = 4
  ref = O_element
FEATURE [App::DocumentObjectGroupPython] G4_CADMIUM_TUNGSTATE  # scripted group (container) (typed FeaturePython)
  Dunit = g/cm3
  Dvalue = 7.9
  Group = -> [Cd_element002,W_element001,O_element020]
  conduct = 2
  density = 1
  expand = 3
  formula = G4_CADMIUM_TUNGSTATE
  name = G4_CADMIUM_TUNGSTATE
  specific = 4
FEATURE [App::DocumentObjectGroupPython] Ca_element005  label="Ca_element : 1"  # scripted group (container) (typed FeaturePython)
  n = 1
  ref = Ca_element
FEATURE [App::DocumentObjectGroupPython] C_element022  label="C_element : 009"  # scripted group (container) (typed FeaturePython)
  n = 1
  ref = C_element
FEATURE [App::DocumentObjectGroupPython] O_element021  label="O_element : 009"  # scripted group (container) (typed FeaturePython)
  n = 3
  ref = O_element
FEATURE [App::DocumentObjectGroupPython] G4_CALCIUM_CARBONATE  # scripted group (container) (typed FeaturePython)
  Dunit = g/cm3
  Dvalue = 2.8
  Group = -> [Ca_element005,C_element022,O_element021]
  conduct = 2
  density = 1
  expand = 3
  formula = G4_CALCIUM_CARBONATE
  name = G4_CALCIUM_CARBONATE
  specific = 4
FEATURE [App::DocumentObjectGroupPython] Ca_element006  label="Ca_element : 002"  # scripted group (container) (typed FeaturePython)
  n = 1
  ref = Ca_element
FEATURE [App::DocumentObjectGroupPython] F_element005  label="F_element : 003"  # scripted group (container) (typed FeaturePython)
  n = 2
  ref = F_element
FEATURE [App::DocumentObjectGroupPython] G4_CALCIUM_FLUORIDE  # scripted group (container) (typed FeaturePython)
  Dunit = g/cm3
  Dvalue = 3.18
  Group = -> [Ca_element006,F_element005]
  conduct = 2
  density = 1
  expand = 3
  formula = G4_CALCIUM_FLUORIDE
  name = G4_CALCIUM_FLUORIDE
  specific = 4
FEATURE [App::DocumentObjectGroupPython] Ca_element007  label="Ca_element : 003"  # scripted group (container) (typed FeaturePython)
  n = 1
  ref = Ca_element
FEATURE [App::DocumentObjectGroupPython] O_element022  label="O_element : 010"  # scripted group (container) (typed FeaturePython)
  n = 1
  ref = O_element
FEATURE [App::DocumentObjectGroupPython] G4_CALCIUM_OXIDE  # scripted group (container) (typed FeaturePython)
  Dunit = g/cm3
  Dvalue = 3.3
  Group = -> [Ca_element007,O_element022]
  conduct = 2
  density = 1
  expand = 3
  formula = G4_CALCIUM_OXIDE
  name = G4_CALCIUM_OXIDE
  specific = 4
FEATURE [App::DocumentObjectGroupPython] Ca_element008  label="Ca_element : 004"  # scripted group (container) (typed FeaturePython)
  n = 1
  ref = Ca_element
FEATURE [App::DocumentObjectGroupPython] S_element007  label="S_element : 002"  # scripted group (container) (typed FeaturePython)
  n = 1
  ref = S_element
FEATURE [App::DocumentObjectGroupPython] O_element023  label="O_element : 011"  # scripted group (container) (typed FeaturePython)
  n = 4
  ref = O_element
FEATURE [App::DocumentObjectGroupPython] G4_CALCIUM_SULFATE  # scripted group (container) (typed FeaturePython)
  Dunit = g/cm3
  Dvalue = 2.96
  Group = -> [Ca_element008,S_element007,O_element023]
  conduct = 2
  density = 1
  expand = 3
  formula = G4_CALCIUM_SULFATE
  name = G4_CALCIUM_SULFATE
  specific = 4
FEATURE [App::DocumentObjectGroupPython] Ca_element009  label="Ca_element : 005"  # scripted group (container) (typed FeaturePython)
  n = 1
  ref = Ca_element
FEATURE [App::DocumentObjectGroupPython] W_element002  label="W_element : 002"  # scripted group (container) (typed FeaturePython)
  n = 1
  ref = W_element
FEATURE [App::DocumentObjectGroupPython] O_element024  label="O_element : 012"  # scripted group (container) (typed FeaturePython)
  n = 4
  ref = O_element
FEATURE [App::DocumentObjectGroupPython] G4_CALCIUM_TUNGSTATE  # scripted group (container) (typed FeaturePython)
  Dunit = g/cm3
  Dvalue = 6.062
  Group = -> [Ca_element009,W_element002,O_element024]
  conduct = 2
  density = 1
  expand = 3
  formula = G4_CALCIUM_TUNGSTATE
  name = G4_CALCIUM_TUNGSTATE
  specific = 4
FEATURE [App::DocumentObjectGroupPython] C_element023  label="C_element : 010"  # scripted group (container) (typed FeaturePython)
  n = 1
  ref = C_element
FEATURE [App::DocumentObjectGroupPython] O_element025  label="O_element : 013"  # scripted group (container) (typed FeaturePython)
  n = 2
  ref = O_element
FEATURE [App::DocumentObjectGroupPython] G4_CARBON_DIOXIDE  # scripted group (container) (typed FeaturePython)
  Dunit = g/cm3
  Dvalue = 0.00184212
  Group = -> [C_element023,O_element025]
  conduct = 2
  density = 1
  expand = 3
  formula = G4_CARBON_DIOXIDE
  name = G4_CARBON_DIOXIDE
  specific = 4
FEATURE [App::DocumentObjectGroupPython] C_element024  label="C_element : 011"  # scripted group (container) (typed FeaturePython)
  n = 1
  ref = C_element
FEATURE [App::DocumentObjectGroupPython] Cl_element004  label="Cl_element : 4"  # scripted group (container) (typed FeaturePython)
  n = 4
  ref = Cl_element
FEATURE [App::DocumentObjectGroupPython] G4_CARBON_TETRACHLORIDE  # scripted group (container) (typed FeaturePython)
  Dunit = g/cm3
  Dvalue = 1.594
  Group = -> [C_element024,Cl_element004]
  conduct = 2
  density = 1
  expand = 3
  formula = G4_CARBON_TETRACHLORIDE
  name = G4_CARBON_TETRACHLORIDE
  specific = 4
FEATURE [App::DocumentObjectGroupPython] C_element025  label="C_element : 012"  # scripted group (container) (typed FeaturePython)
  n = 6
  ref = C_element
FEATURE [App::DocumentObjectGroupPython] H_element021  label="H_element : 012"  # scripted group (container) (typed FeaturePython)
  n = 10
  ref = H_element
FEATURE [App::DocumentObjectGroupPython] O_element026  label="O_element : 5"  # scripted group (container) (typed FeaturePython)
  n = 5
  ref = O_element
FEATURE [App::DocumentObjectGroupPython] G4_CELLULOSE_CELLOPHANE  # scripted group (container) (typed FeaturePython)
  Dunit = g/cm3
  Dvalue = 1.42
  Group = -> [C_element025,H_element021,O_element026]
  conduct = 2
  density = 1
  expand = 3
  formula = G4_CELLULOSE_CELLOPHANE
  name = G4_CELLULOSE_CELLOPHANE
  specific = 4
FEATURE [App::DocumentObjectGroupPython] H_element022  label="H_element : 0.067"  # scripted group (container) (typed FeaturePython)
  n = 0.067125
FEATURE [App::DocumentObjectGroupPython] C_element026  label="C_element : 0.545"  # scripted group (container) (typed FeaturePython)
  n = 0.545403
FEATURE [App::DocumentObjectGroupPython] O_element027  label="O_element : 0.387"  # scripted group (container) (typed FeaturePython)
  n = 0.387472
FEATURE [App::DocumentObjectGroupPython] G4_CELLULOSE_BUTYRATE  # scripted group (container) (typed FeaturePython)
  Dunit = g/cm3
  Dvalue = 1.2
  Group = -> [H_element022,C_element026,O_element027]
  conduct = 2
  density = 1
  expand = 3
  formula = G4_CELLULOSE_BUTYRATE
  name = G4_CELLULOSE_BUTYRATE
  specific = 4
FEATURE [App::DocumentObjectGroupPython] H_element023  label="H_element : 0.029"  # scripted group (container) (typed FeaturePython)
  n = 0.029216
FEATURE [App::DocumentObjectGroupPython] C_element027  label="C_element : 0.271"  # scripted group (container) (typed FeaturePython)
  n = 0.271296
FEATURE [App::DocumentObjectGroupPython] N_element013  label="N_element : 0.121"  # scripted group (container) (typed FeaturePython)
  n = 0.121276
FEATURE [App::DocumentObjectGroupPython] O_element028  label="O_element : 0.578"  # scripted group (container) (typed FeaturePython)
  n = 0.578212
FEATURE [App::DocumentObjectGroupPython] G4_CELLULOSE_NITRATE  # scripted group (container) (typed FeaturePython)
  Dunit = g/cm3
  Dvalue = 1.49
  Group = -> [H_element023,C_element027,N_element013,O_element028]
  conduct = 2
  density = 1
  expand = 3
  formula = G4_CELLULOSE_NITRATE
  name = G4_CELLULOSE_NITRATE
  specific = 4
FEATURE [App::DocumentObjectGroupPython] H_element024  label="H_element : 0.108"  # scripted group (container) (typed FeaturePython)
  n = 0.107596
FEATURE [App::DocumentObjectGroupPython] N_element014  label="N_element : 0.001"  # scripted group (container) (typed FeaturePython)
  n = 0.0008
FEATURE [App::DocumentObjectGroupPython] O_element029  label="O_element : 0.875"  # scripted group (container) (typed FeaturePython)
  n = 0.874976
FEATURE [App::DocumentObjectGroupPython] S_element008  label="S_element : 0.015"  # scripted group (container) (typed FeaturePython)
  n = 0.014627
FEATURE [App::DocumentObjectGroupPython] Ce_element001  label="Ce_element : 0.002"  # scripted group (container) (typed FeaturePython)
  n = 0.002001
FEATURE [App::DocumentObjectGroupPython] G4_CERIC_SULFATE  # scripted group (container) (typed FeaturePython)
  Dunit = g/cm3
  Dvalue = 1.03
  Group = -> [H_element024,N_element014,O_element029,S_element008,Ce_element001]
  conduct = 2
  density = 1
  expand = 3
  formula = G4_CERIC_SULFATE
  name = G4_CERIC_SULFATE
  specific = 4
FEATURE [App::DocumentObjectGroupPython] Cs_element001  label="Cs_element : 1"  # scripted group (container) (typed FeaturePython)
  n = 1
  ref = Cs_element
FEATURE [App::DocumentObjectGroupPython] F_element006  label="F_element : 1"  # scripted group (container) (typed FeaturePython)
  n = 1
  ref = F_element
FEATURE [App::DocumentObjectGroupPython] G4_CESIUM_FLUORIDE  # scripted group (container) (typed FeaturePython)
  Dunit = g/cm3
  Dvalue = 4.115
  Group = -> [Cs_element001,F_element006]
  conduct = 2
  density = 1
  expand = 3
  formula = G4_CESIUM_FLUORIDE
  name = G4_CESIUM_FLUORIDE
  specific = 4
FEATURE [App::DocumentObjectGroupPython] Cs_element002  label="Cs_element : 002"  # scripted group (container) (typed FeaturePython)
  n = 1
  ref = Cs_element
FEATURE [App::DocumentObjectGroupPython] I_element001  label="I_element : 1"  # scripted group (container) (typed FeaturePython)
  n = 1
  ref = I_element
FEATURE [App::DocumentObjectGroupPython] G4_CESIUM_IODIDE  # scripted group (container) (typed FeaturePython)
  Dunit = g/cm3
  Dvalue = 4.51
  Group = -> [Cs_element002,I_element001]
  conduct = 2
  density = 1
  expand = 3
  formula = G4_CESIUM_IODIDE
  name = G4_CESIUM_IODIDE
  specific = 4
FEATURE [App::DocumentObjectGroupPython] C_element028  label="C_element : 013"  # scripted group (container) (typed FeaturePython)
  n = 6
  ref = C_element
FEATURE [App::DocumentObjectGroupPython] H_element025  label="H_element : 013"  # scripted group (container) (typed FeaturePython)
  n = 5
  ref = H_element
FEATURE [App::DocumentObjectGroupPython] Cl_element005  label="Cl_element : 1"  # scripted group (container) (typed FeaturePython)
  n = 1
  ref = Cl_element
FEATURE [App::DocumentObjectGroupPython] G4_CHLOROBENZENE  # scripted group (container) (typed FeaturePython)
  Dunit = g/cm3
  Dvalue = 1.1058
  Group = -> [C_element028,H_element025,Cl_element005]
  conduct = 2
  density = 1
  expand = 3
  formula = G4_CHLOROBENZENE
  name = G4_CHLOROBENZENE
  specific = 4
FEATURE [App::DocumentObjectGroupPython] C_element029  label="C_element : 014"  # scripted group (container) (typed FeaturePython)
  n = 1
  ref = C_element
FEATURE [App::DocumentObjectGroupPython] H_element026  label="H_element : 1"  # scripted group (container) (typed FeaturePython)
  n = 1
  ref = H_element
FEATURE [App::DocumentObjectGroupPython] Cl_element006  label="Cl_element : 3"  # scripted group (container) (typed FeaturePython)
  n = 3
  ref = Cl_element
FEATURE [App::DocumentObjectGroupPython] G4_CHLOROFORM  # scripted group (container) (typed FeaturePython)
  Dunit = g/cm3
  Dvalue = 1.4832
  Group = -> [C_element029,H_element026,Cl_element006]
  conduct = 2
  density = 1
  expand = 3
  formula = G4_CHLOROFORM
  name = G4_CHLOROFORM
  specific = 4
FEATURE [App::DocumentObjectGroupPython] H_element027  label="H_element : 0.010"  # scripted group (container) (typed FeaturePython)
  n = 0.01
FEATURE [App::DocumentObjectGroupPython] C_element030  label="C_element : 0.001"  # scripted group (container) (typed FeaturePython)
  n = 0.001
FEATURE [App::DocumentObjectGroupPython] O_element030  label="O_element : 0.529"  # scripted group (container) (typed FeaturePython)
  n = 0.529107
FEATURE [App::DocumentObjectGroupPython] Na_element005  label="Na_element : 0.016"  # scripted group (container) (typed FeaturePython)
  n = 0.016
FEATURE [App::DocumentObjectGroupPython] Mg_element003  label="Mg_element : 0.004"  # scripted group (container) (typed FeaturePython)
  n = 0.002
FEATURE [App::DocumentObjectGroupPython] Al_element002  label="Al_element : 0.034"  # scripted group (container) (typed FeaturePython)
  n = 0.033872
FEATURE [App::DocumentObjectGroupPython] Si_element002  label="Si_element : 0.337"  # scripted group (container) (typed FeaturePython)
  n = 0.337021
FEATURE [App::DocumentObjectGroupPython] K_element003  label="K_element : 0.013"  # scripted group (container) (typed FeaturePython)
  n = 0.013
FEATURE [App::DocumentObjectGroupPython] Ca_element010  label="Ca_element : 0.044"  # scripted group (container) (typed FeaturePython)
  n = 0.044
FEATURE [App::DocumentObjectGroupPython] Fe_element002  label="Fe_element : 0.014"  # scripted group (container) (typed FeaturePython)
  n = 0.014
FEATURE [App::DocumentObjectGroupPython] G4_CONCRETE  # scripted group (container) (typed FeaturePython)
  Dunit = g/cm3
  Dvalue = 2.3
  Group = -> [H_element027,C_element030,O_element030,Na_element005,Mg_element003,Al_element002,Si_element002,K_element003,Ca_element010,Fe_element002]
  conduct = 2
  density = 1
  expand = 3
  formula = G4_CONCRETE
  name = G4_CONCRETE
  specific = 4
FEATURE [App::DocumentObjectGroupPython] C_element031  label="C_element : 015"  # scripted group (container) (typed FeaturePython)
  n = 6
  ref = C_element
FEATURE [App::DocumentObjectGroupPython] H_element028  label="H_element : 12"  # scripted group (container) (typed FeaturePython)
  n = 12
  ref = H_element
FEATURE [App::DocumentObjectGroupPython] G4_CYCLOHEXANE  # scripted group (container) (typed FeaturePython)
  Dunit = g/cm3
  Dvalue = 0.779
  Group = -> [C_element031,H_element028]
  conduct = 2
  density = 1
  expand = 3
  formula = G4_CYCLOHEXANE
  name = G4_CYCLOHEXANE
  specific = 4
FEATURE [App::DocumentObjectGroupPython] C_element032  label="C_element : 016"  # scripted group (container) (typed FeaturePython)
  n = 6
  ref = C_element
FEATURE [App::DocumentObjectGroupPython] H_element029  label="H_element : 4"  # scripted group (container) (typed FeaturePython)
  n = 4
  ref = H_element
FEATURE [App::DocumentObjectGroupPython] Cl_element007  label="Cl_element : 2"  # scripted group (container) (typed FeaturePython)
  n = 2
  ref = Cl_element
FEATURE [App::DocumentObjectGroupPython] G4_1_2_DICHLOROBENZENE  label="G4_1.2-DICHLOROBENZENE"  # scripted group (container) (typed FeaturePython)
  Dunit = g/cm3
  Dvalue = 1.3048
  Group = -> [C_element032,H_element029,Cl_element007]
  conduct = 2
  density = 1
  expand = 3
  formula = G4_1.2-DICHLOROBENZENE
  name = G4_1.2-DICHLOROBENZENE
  specific = 4
FEATURE [App::DocumentObjectGroupPython] C_element033  label="C_element : 017"  # scripted group (container) (typed FeaturePython)
  n = 4
  ref = C_element
FEATURE [App::DocumentObjectGroupPython] H_element030  label="H_element : 8"  # scripted group (container) (typed FeaturePython)
  n = 8
  ref = H_element
FEATURE [App::DocumentObjectGroupPython] O_element031  label="O_element : 014"  # scripted group (container) (typed FeaturePython)
  n = 1
  ref = O_element
FEATURE [App::DocumentObjectGroupPython] Cl_element008  label="Cl_element : 005"  # scripted group (container) (typed FeaturePython)
  n = 2
  ref = Cl_element
FEATURE [App::DocumentObjectGroupPython] G4_DICHLORODIETHYL_ETHER  # scripted group (container) (typed FeaturePython)
  Dunit = g/cm3
  Dvalue = 1.2199
  Group = -> [C_element033,H_element030,O_element031,Cl_element008]
  conduct = 2
  density = 1
  expand = 3
  formula = G4_DICHLORODIETHYL_ETHER
  name = G4_DICHLORODIETHYL_ETHER
  specific = 4
FEATURE [App::DocumentObjectGroupPython] C_element034  label="C_element : 018"  # scripted group (container) (typed FeaturePython)
  n = 2
  ref = C_element
FEATURE [App::DocumentObjectGroupPython] H_element031  label="H_element : 014"  # scripted group (container) (typed FeaturePython)
  n = 4
  ref = H_element
FEATURE [App::DocumentObjectGroupPython] Cl_element009  label="Cl_element : 006"  # scripted group (container) (typed FeaturePython)
  n = 2
  ref = Cl_element
FEATURE [App::DocumentObjectGroupPython] G4_1_2_DICHLOROETHANE  label="G4_1.2-DICHLOROETHANE"  # scripted group (container) (typed FeaturePython)
  Dunit = g/cm3
  Dvalue = 1.2351
  Group = -> [C_element034,H_element031,Cl_element009]
  conduct = 2
  density = 1
  expand = 3
  formula = G4_1.2-DICHLOROETHANE
  name = G4_1.2-DICHLOROETHANE
  specific = 4
FEATURE [App::DocumentObjectGroupPython] C_element035  label="C_element : 019"  # scripted group (container) (typed FeaturePython)
  n = 4
  ref = C_element
FEATURE [App::DocumentObjectGroupPython] H_element032  label="H_element : 015"  # scripted group (container) (typed FeaturePython)
  n = 10
  ref = H_element
FEATURE [App::DocumentObjectGroupPython] O_element032  label="O_element : 015"  # scripted group (container) (typed FeaturePython)
  n = 1
  ref = O_element
FEATURE [App::DocumentObjectGroupPython] G4_DIETHYL_ETHER  # scripted group (container) (typed FeaturePython)
  Dunit = g/cm3
  Dvalue = 0.71378
  Group = -> [C_element035,H_element032,O_element032]
  conduct = 2
  density = 1
  expand = 3
  formula = G4_DIETHYL_ETHER
  name = G4_DIETHYL_ETHER
  specific = 4
FEATURE [App::DocumentObjectGroupPython] C_element036  label="C_element : 020"  # scripted group (container) (typed FeaturePython)
  n = 3
  ref = C_element
FEATURE [App::DocumentObjectGroupPython] H_element033  label="H_element : 016"  # scripted group (container) (typed FeaturePython)
  n = 7
  ref = H_element
FEATURE [App::DocumentObjectGroupPython] N_element015  label="N_element : 008"  # scripted group (container) (typed FeaturePython)
  n = 1
  ref = N_element
FEATURE [App::DocumentObjectGroupPython] O_element033  label="O_element : 016"  # scripted group (container) (typed FeaturePython)
  n = 1
  ref = O_element
FEATURE [App::DocumentObjectGroupPython] G4_N_N_DIMETHYL_FORMAMIDE  label="G4_N.N-DIMETHYL_FORMAMIDE"  # scripted group (container) (typed FeaturePython)
  Dunit = g/cm3
  Dvalue = 0.9487
  Group = -> [C_element036,H_element033,N_element015,O_element033]
  conduct = 2
  density = 1
  expand = 3
  formula = G4_N.N-DIMETHYL_FORMAMIDE
  name = G4_N.N-DIMETHYL_FORMAMIDE
  specific = 4
FEATURE [App::DocumentObjectGroupPython] C_element037  label="C_element : 021"  # scripted group (container) (typed FeaturePython)
  n = 2
  ref = C_element
FEATURE [App::DocumentObjectGroupPython] H_element034  label="H_element : 017"  # scripted group (container) (typed FeaturePython)
  n = 6
  ref = H_element
FEATURE [App::DocumentObjectGroupPython] O_element034  label="O_element : 017"  # scripted group (container) (typed FeaturePython)
  n = 1
  ref = O_element
FEATURE [App::DocumentObjectGroupPython] S_element009  label="S_element : 003"  # scripted group (container) (typed FeaturePython)
  n = 1
  ref = S_element
FEATURE [App::DocumentObjectGroupPython] G4_DIMETHYL_SULFOXIDE  # scripted group (container) (typed FeaturePython)
  Dunit = g/cm3
  Dvalue = 1.1014
  Group = -> [C_element037,H_element034,O_element034,S_element009]
  conduct = 2
  density = 1
  expand = 3
  formula = G4_DIMETHYL_SULFOXIDE
  name = G4_DIMETHYL_SULFOXIDE
  specific = 4
FEATURE [App::DocumentObjectGroupPython] C_element038  label="C_element : 022"  # scripted group (container) (typed FeaturePython)
  n = 2
  ref = C_element
FEATURE [App::DocumentObjectGroupPython] H_element035  label="H_element : 018"  # scripted group (container) (typed FeaturePython)
  n = 6
  ref = H_element
FEATURE [App::DocumentObjectGroupPython] G4_ETHANE  # scripted group (container) (typed FeaturePython)
  Dunit = g/cm3
  Dvalue = 0.00125324
  Group = -> [C_element038,H_element035]
  conduct = 2
  density = 1
  expand = 3
  formula = G4_ETHANE
  name = G4_ETHANE
  specific = 4
FEATURE [App::DocumentObjectGroupPython] C_element039  label="C_element : 023"  # scripted group (container) (typed FeaturePython)
  n = 2
  ref = C_element
FEATURE [App::DocumentObjectGroupPython] H_element036  label="H_element : 019"  # scripted group (container) (typed FeaturePython)
  n = 6
  ref = H_element
FEATURE [App::DocumentObjectGroupPython] O_element035  label="O_element : 018"  # scripted group (container) (typed FeaturePython)
  n = 1
  ref = O_element
FEATURE [App::DocumentObjectGroupPython] G4_ETHYL_ALCOHOL  # scripted group (container) (typed FeaturePython)
  Dunit = g/cm3
  Dvalue = 0.7893
  Group = -> [C_element039,H_element036,O_element035]
  conduct = 2
  density = 1
  expand = 3
  formula = G4_ETHYL_ALCOHOL
  name = G4_ETHYL_ALCOHOL
  specific = 4
FEATURE [App::DocumentObjectGroupPython] H_element037  label="H_element : 0.090"  # scripted group (container) (typed FeaturePython)
  n = 0.090027
FEATURE [App::DocumentObjectGroupPython] C_element040  label="C_element : 0.585"  # scripted group (container) (typed FeaturePython)
  n = 0.585182
FEATURE [App::DocumentObjectGroupPython] O_element036  label="O_element : 0.325"  # scripted group (container) (typed FeaturePython)
  n = 0.324791
FEATURE [App::DocumentObjectGroupPython] G4_ETHYL_CELLULOSE  # scripted group (container) (typed FeaturePython)
  Dunit = g/cm3
  Dvalue = 1.13
  Group = -> [H_element037,C_element040,O_element036]
  conduct = 2
  density = 1
  expand = 3
  formula = G4_ETHYL_CELLULOSE
  name = G4_ETHYL_CELLULOSE
  specific = 4
FEATURE [App::DocumentObjectGroupPython] C_element041  label="C_element : 024"  # scripted group (container) (typed FeaturePython)
  n = 2
  ref = C_element
FEATURE [App::DocumentObjectGroupPython] H_element038  label="H_element : 020"  # scripted group (container) (typed FeaturePython)
  n = 4
  ref = H_element
FEATURE [App::DocumentObjectGroupPython] G4_ETHYLENE  # scripted group (container) (typed FeaturePython)
  Dunit = g/cm3
  Dvalue = 0.00117497
  Group = -> [C_element041,H_element038]
  conduct = 2
  density = 1
  expand = 3
  formula = G4_ETHYLENE
  name = G4_ETHYLENE
  specific = 4
FEATURE [App::DocumentObjectGroupPython] H_element039  label="H_element : 0.096"  # scripted group (container) (typed FeaturePython)
  n = 0.096
FEATURE [App::DocumentObjectGroupPython] C_element042  label="C_element : 0.195"  # scripted group (container) (typed FeaturePython)
  n = 0.195
FEATURE [App::DocumentObjectGroupPython] N_element016  label="N_element : 0.057"  # scripted group (container) (typed FeaturePython)
  n = 0.057
FEATURE [App::DocumentObjectGroupPython] O_element037  label="O_element : 0.646"  # scripted group (container) (typed FeaturePython)
  n = 0.646
FEATURE [App::DocumentObjectGroupPython] Na_element006  label="Na_element : 0.017"  # scripted group (container) (typed FeaturePython)
  n = 0.001
FEATURE [App::DocumentObjectGroupPython] P_element005  label="P_element : 0.104"  # scripted group (container) (typed FeaturePython)
  n = 0.001
FEATURE [App::DocumentObjectGroupPython] S_element010  label="S_element : 0.016"  # scripted group (container) (typed FeaturePython)
  n = 0.003
FEATURE [App::DocumentObjectGroupPython] Cl_element010  label="Cl_element : 0.005"  # scripted group (container) (typed FeaturePython)
  n = 0.001
FEATURE [App::DocumentObjectGroupPython] G4_EYE_LENS_ICRP  # scripted group (container) (typed FeaturePython)
  Dunit = g/cm3
  Dvalue = 1.07
  Group = -> [H_element039,C_element042,N_element016,O_element037,Na_element006,P_element005,S_element010,Cl_element010]
  conduct = 2
  density = 1
  expand = 3
  formula = G4_EYE_LENS_ICRP
  name = G4_EYE_LENS_ICRP
  specific = 4
FEATURE [App::DocumentObjectGroupPython] Fe_element003  label="Fe_element : 2"  # scripted group (container) (typed FeaturePython)
  n = 2
  ref = Fe_element
FEATURE [App::DocumentObjectGroupPython] O_element038  label="O_element : 019"  # scripted group (container) (typed FeaturePython)
  n = 3
  ref = O_element
FEATURE [App::DocumentObjectGroupPython] G4_FERRIC_OXIDE  # scripted group (container) (typed FeaturePython)
  Dunit = g/cm3
  Dvalue = 5.2
  Group = -> [Fe_element003,O_element038]
  conduct = 2
  density = 1
  expand = 3
  formula = G4_FERRIC_OXIDE
  name = G4_FERRIC_OXIDE
  specific = 4
FEATURE [App::DocumentObjectGroupPython] Fe_element004  label="Fe_element : 1"  # scripted group (container) (typed FeaturePython)
  n = 1
  ref = Fe_element
FEATURE [App::DocumentObjectGroupPython] B_element003  label="B_element : 1"  # scripted group (container) (typed FeaturePython)
  n = 1
  ref = B_element
FEATURE [App::DocumentObjectGroupPython] G4_FERROBORIDE  # scripted group (container) (typed FeaturePython)
  Dunit = g/cm3
  Dvalue = 7.15
  Group = -> [Fe_element004,B_element003]
  conduct = 2
  density = 1
  expand = 3
  formula = G4_FERROBORIDE
  name = G4_FERROBORIDE
  specific = 4
FEATURE [App::DocumentObjectGroupPython] Fe_element005  label="Fe_element : 003"  # scripted group (container) (typed FeaturePython)
  n = 1
  ref = Fe_element
FEATURE [App::DocumentObjectGroupPython] O_element039  label="O_element : 020"  # scripted group (container) (typed FeaturePython)
  n = 1
  ref = O_element
FEATURE [App::DocumentObjectGroupPython] G4_FERROUS_OXIDE  # scripted group (container) (typed FeaturePython)
  Dunit = g/cm3
  Dvalue = 5.7
  Group = -> [Fe_element005,O_element039]
  conduct = 2
  density = 1
  expand = 3
  formula = G4_FERROUS_OXIDE
  name = G4_FERROUS_OXIDE
  specific = 4
FEATURE [App::DocumentObjectGroupPython] H_element040  label="H_element : 0.115"  # scripted group (container) (typed FeaturePython)
  n = 0.108259
FEATURE [App::DocumentObjectGroupPython] N_element017  label="N_element : 0.000"  # scripted group (container) (typed FeaturePython)
  n = 2.7e-05
FEATURE [App::DocumentObjectGroupPython] O_element040  label="O_element : 0.879"  # scripted group (container) (typed FeaturePython)
  n = 0.878636
FEATURE [App::DocumentObjectGroupPython] Na_element007  label="Na_element : 0.000"  # scripted group (container) (typed FeaturePython)
  n = 2.2e-05
FEATURE [App::DocumentObjectGroupPython] S_element011  label="S_element : 0.013"  # scripted group (container) (typed FeaturePython)
  n = 0.012968
FEATURE [App::DocumentObjectGroupPython] Cl_element011  label="Cl_element : 0.000"  # scripted group (container) (typed FeaturePython)
  n = 3.4e-05
FEATURE [App::DocumentObjectGroupPython] Fe_element006  label="Fe_element : 0.000"  # scripted group (container) (typed FeaturePython)
  n = 5.4e-05
FEATURE [App::DocumentObjectGroupPython] G4_FERROUS_SULFATE  # scripted group (container) (typed FeaturePython)
  Dunit = g/cm3
  Dvalue = 1.024
  Group = -> [H_element040,N_element017,O_element040,Na_element007,S_element011,Cl_element011,Fe_element006]
  conduct = 2
  density = 1
  expand = 3
  formula = G4_FERROUS_SULFATE
  name = G4_FERROUS_SULFATE
  specific = 4
FEATURE [App::DocumentObjectGroupPython] C_element043  label="C_element : 0.099"  # scripted group (container) (typed FeaturePython)
  n = 0.099335
FEATURE [App::DocumentObjectGroupPython] F_element007  label="F_element : 0.314"  # scripted group (container) (typed FeaturePython)
  n = 0.314247
FEATURE [App::DocumentObjectGroupPython] Cl_element012  label="Cl_element : 0.586"  # scripted group (container) (typed FeaturePython)
  n = 0.586418
FEATURE [App::DocumentObjectGroupPython] G4_FREON_12  label="G4_FREON-12"  # scripted group (container) (typed FeaturePython)
  Dunit = g/cm3
  Dvalue = 1.12
  Group = -> [C_element043,F_element007,Cl_element012]
  conduct = 2
  density = 1
  expand = 3
  formula = G4_FREON-12
  name = G4_FREON-12
  specific = 4
FEATURE [App::DocumentObjectGroupPython] C_element044  label="C_element : 0.057"  # scripted group (container) (typed FeaturePython)
  n = 0.057245
FEATURE [App::DocumentObjectGroupPython] F_element008  label="F_element : 0.181"  # scripted group (container) (typed FeaturePython)
  n = 0.181096
FEATURE [App::DocumentObjectGroupPython] Br_element001  label="Br_element : 0.762"  # scripted group (container) (typed FeaturePython)
  n = 0.761659
FEATURE [App::DocumentObjectGroupPython] G4_FREON_12B2  label="G4_FREON-12B2"  # scripted group (container) (typed FeaturePython)
  Dunit = g/cm3
  Dvalue = 1.8
  Group = -> [C_element044,F_element008,Br_element001]
  conduct = 2
  density = 1
  expand = 3
  formula = G4_FREON-12B2
  name = G4_FREON-12B2
  specific = 4
FEATURE [App::DocumentObjectGroupPython] C_element045  label="C_element : 0.115"  # scripted group (container) (typed FeaturePython)
  n = 0.114983
FEATURE [App::DocumentObjectGroupPython] F_element009  label="F_element : 0.546"  # scripted group (container) (typed FeaturePython)
  n = 0.545621
FEATURE [App::DocumentObjectGroupPython] Cl_element013  label="Cl_element : 0.339"  # scripted group (container) (typed FeaturePython)
  n = 0.339396
FEATURE [App::DocumentObjectGroupPython] G4_FREON_13  label="G4_FREON-13"  # scripted group (container) (typed FeaturePython)
  Dunit = g/cm3
  Dvalue = 0.95
  Group = -> [C_element045,F_element009,Cl_element013]
  conduct = 2
  density = 1
  expand = 3
  formula = G4_FREON-13
  name = G4_FREON-13
  specific = 4
FEATURE [App::DocumentObjectGroupPython] C_element046  label="C_element : 025"  # scripted group (container) (typed FeaturePython)
  n = 1
  ref = C_element
FEATURE [App::DocumentObjectGroupPython] F_element010  label="F_element : 3"  # scripted group (container) (typed FeaturePython)
  n = 3
  ref = F_element
FEATURE [App::DocumentObjectGroupPython] Br_element002  label="Br_element : 1"  # scripted group (container) (typed FeaturePython)
  n = 1
  ref = Br_element
FEATURE [App::DocumentObjectGroupPython] G4_FREON_13B1  label="G4_FREON-13B1"  # scripted group (container) (typed FeaturePython)
  Dunit = g/cm3
  Dvalue = 1.5
  Group = -> [C_element046,F_element010,Br_element002]
  conduct = 2
  density = 1
  expand = 3
  formula = G4_FREON-13B1
  name = G4_FREON-13B1
  specific = 4
FEATURE [App::DocumentObjectGroupPython] C_element047  label="C_element : 0.061"  # scripted group (container) (typed FeaturePython)
  n = 0.061309
FEATURE [App::DocumentObjectGroupPython] F_element011  label="F_element : 0.291"  # scripted group (container) (typed FeaturePython)
  n = 0.290924
FEATURE [App::DocumentObjectGroupPython] I_element002  label="I_element : 0.648"  # scripted group (container) (typed FeaturePython)
  n = 0.647767
FEATURE [App::DocumentObjectGroupPython] G4_FREON_13I1  label="G4_FREON-13I1"  # scripted group (container) (typed FeaturePython)
  Dunit = g/cm3
  Dvalue = 1.8
  Group = -> [C_element047,F_element011,I_element002]
  conduct = 2
  density = 1
  expand = 3
  formula = G4_FREON-13I1
  name = G4_FREON-13I1
  specific = 4
FEATURE [App::DocumentObjectGroupPython] Gd_element001  label="Gd_element : 2"  # scripted group (container) (typed FeaturePython)
  n = 2
  ref = Gd_element
FEATURE [App::DocumentObjectGroupPython] O_element041  label="O_element : 021"  # scripted group (container) (typed FeaturePython)
  n = 2
  ref = O_element
FEATURE [App::DocumentObjectGroupPython] S_element012  label="S_element : 004"  # scripted group (container) (typed FeaturePython)
  n = 1
  ref = S_element
FEATURE [App::DocumentObjectGroupPython] G4_GADOLINIUM_OXYSULFIDE  # scripted group (container) (typed FeaturePython)
  Dunit = g/cm3
  Dvalue = 7.44
  Group = -> [Gd_element001,O_element041,S_element012]
  conduct = 2
  density = 1
  expand = 3
  formula = G4_GADOLINIUM_OXYSULFIDE
  name = G4_GADOLINIUM_OXYSULFIDE
  specific = 4
FEATURE [App::DocumentObjectGroupPython] Ga_element001  label="Ga_element : 1"  # scripted group (container) (typed FeaturePython)
  n = 1
  ref = Ga_element
FEATURE [App::DocumentObjectGroupPython] As_element001  label="As_element : 1"  # scripted group (container) (typed FeaturePython)
  n = 1
  ref = As_element
FEATURE [App::DocumentObjectGroupPython] G4_GALLIUM_ARSENIDE  # scripted group (container) (typed FeaturePython)
  Dunit = g/cm3
  Dvalue = 5.31
  Group = -> [Ga_element001,As_element001]
  conduct = 2
  density = 1
  expand = 3
  formula = G4_GALLIUM_ARSENIDE
  name = G4_GALLIUM_ARSENIDE
  specific = 4
FEATURE [App::DocumentObjectGroupPython] H_element041  label="H_element : 0.081"  # scripted group (container) (typed FeaturePython)
  n = 0.08118
FEATURE [App::DocumentObjectGroupPython] C_element048  label="C_element : 0.416"  # scripted group (container) (typed FeaturePython)
  n = 0.41606
FEATURE [App::DocumentObjectGroupPython] N_element018  label="N_element : 0.111"  # scripted group (container) (typed FeaturePython)
  n = 0.11124
FEATURE [App::DocumentObjectGroupPython] O_element042  label="O_element : 0.381"  # scripted group (container) (typed FeaturePython)
  n = 0.38064
FEATURE [App::DocumentObjectGroupPython] S_element013  label="S_element : 0.011"  # scripted group (container) (typed FeaturePython)
  n = 0.01088
FEATURE [App::DocumentObjectGroupPython] G4_GEL_PHOTO_EMULSION  # scripted group (container) (typed FeaturePython)
  Dunit = g/cm3
  Dvalue = 1.2914
  Group = -> [H_element041,C_element048,N_element018,O_element042,S_element013]
  conduct = 2
  density = 1
  expand = 3
  formula = G4_GEL_PHOTO_EMULSION
  name = G4_GEL_PHOTO_EMULSION
  specific = 4
FEATURE [App::DocumentObjectGroupPython] B_element004  label="B_element : 0.040"  # scripted group (container) (typed FeaturePython)
  n = 0.0400639
FEATURE [App::DocumentObjectGroupPython] O_element043  label="O_element : 0.540"  # scripted group (container) (typed FeaturePython)
  n = 0.539561
FEATURE [App::DocumentObjectGroupPython] Na_element008  label="Na_element : 0.028"  # scripted group (container) (typed FeaturePython)
  n = 0.0281909
FEATURE [App::DocumentObjectGroupPython] Al_element003  label="Al_element : 0.012"  # scripted group (container) (typed FeaturePython)
  n = 0.011644
FEATURE [App::DocumentObjectGroupPython] Si_element003  label="Si_element : 0.377"  # scripted group (container) (typed FeaturePython)
  n = 0.377219
FEATURE [App::DocumentObjectGroupPython] K_element004  label="K_element : 0.014"  # scripted group (container) (typed FeaturePython)
  n = 0.00332099
FEATURE [App::DocumentObjectGroupPython] G4_Pyrex_Glass  # scripted group (container) (typed FeaturePython)
  Dunit = g/cm3
  Dvalue = 2.23
  Group = -> [B_element004,O_element043,Na_element008,Al_element003,Si_element003,K_element004]
  conduct = 2
  density = 1
  expand = 3
  formula = G4_Pyrex_Glass
  name = G4_Pyrex_Glass
  specific = 4
FEATURE [App::DocumentObjectGroupPython] O_element044  label="O_element : 0.156"  # scripted group (container) (typed FeaturePython)
  n = 0.156453
FEATURE [App::DocumentObjectGroupPython] Si_element004  label="Si_element : 0.081"  # scripted group (container) (typed FeaturePython)
  n = 0.080866
FEATURE [App::DocumentObjectGroupPython] Ti_element001  label="Ti_element : 0.008"  # scripted group (container) (typed FeaturePython)
  n = 0.008092
FEATURE [App::DocumentObjectGroupPython] As_element002  label="As_element : 0.003"  # scripted group (container) (typed FeaturePython)
  n = 0.002651
FEATURE [App::DocumentObjectGroupPython] Pb_element001  label="Pb_element : 0.752"  # scripted group (container) (typed FeaturePython)
  n = 0.751938
FEATURE [App::DocumentObjectGroupPython] G4_GLASS_LEAD  # scripted group (container) (typed FeaturePython)
  Dunit = g/cm3
  Dvalue = 6.22
  Group = -> [O_element044,Si_element004,Ti_element001,As_element002,Pb_element001]
  conduct = 2
  density = 1
  expand = 3
  formula = G4_GLASS_LEAD
  name = G4_GLASS_LEAD
  specific = 4
FEATURE [App::DocumentObjectGroupPython] O_element045  label="O_element : 0.460"  # scripted group (container) (typed FeaturePython)
  n = 0.4598
FEATURE [App::DocumentObjectGroupPython] Na_element009  label="Na_element : 0.096"  # scripted group (container) (typed FeaturePython)
  n = 0.0964411
FEATURE [App::DocumentObjectGroupPython] Si_element005  label="Si_element : 0.378"  # scripted group (container) (typed FeaturePython)
  n = 0.336553
FEATURE [App::DocumentObjectGroupPython] Ca_element011  label="Ca_element : 0.107"  # scripted group (container) (typed FeaturePython)
  n = 0.107205
FEATURE [App::DocumentObjectGroupPython] G4_GLASS_PLATE  # scripted group (container) (typed FeaturePython)
  Dunit = g/cm3
  Dvalue = 2.4
  Group = -> [O_element045,Na_element009,Si_element005,Ca_element011]
  conduct = 2
  density = 1
  expand = 3
  formula = G4_GLASS_PLATE
  name = G4_GLASS_PLATE
  specific = 4
FEATURE [App::DocumentObjectGroupPython] C_element049  label="C_element : 026"  # scripted group (container) (typed FeaturePython)
  n = 5
  ref = C_element
FEATURE [App::DocumentObjectGroupPython] H_element042  label="H_element : 021"  # scripted group (container) (typed FeaturePython)
  n = 10
  ref = H_element
FEATURE [App::DocumentObjectGroupPython] N_element019  label="N_element : 2"  # scripted group (container) (typed FeaturePython)
  n = 2
  ref = N_element
FEATURE [App::DocumentObjectGroupPython] O_element046  label="O_element : 022"  # scripted group (container) (typed FeaturePython)
  n = 3
  ref = O_element
FEATURE [App::DocumentObjectGroupPython] G4_GLUTAMINE  # scripted group (container) (typed FeaturePython)
  Dunit = g/cm3
  Dvalue = 1.46
  Group = -> [C_element049,H_element042,N_element019,O_element046]
  conduct = 2
  density = 1
  expand = 3
  formula = G4_GLUTAMINE
  name = G4_GLUTAMINE
  specific = 4
FEATURE [App::DocumentObjectGroupPython] C_element050  label="C_element : 027"  # scripted group (container) (typed FeaturePython)
  n = 3
  ref = C_element
FEATURE [App::DocumentObjectGroupPython] H_element043  label="H_element : 022"  # scripted group (container) (typed FeaturePython)
  n = 8
  ref = H_element
FEATURE [App::DocumentObjectGroupPython] O_element047  label="O_element : 023"  # scripted group (container) (typed FeaturePython)
  n = 3
  ref = O_element
FEATURE [App::DocumentObjectGroupPython] G4_GLYCEROL  # scripted group (container) (typed FeaturePython)
  Dunit = g/cm3
  Dvalue = 1.2613
  Group = -> [C_element050,H_element043,O_element047]
  conduct = 2
  density = 1
  expand = 3
  formula = G4_GLYCEROL
  name = G4_GLYCEROL
  specific = 4
FEATURE [App::DocumentObjectGroupPython] C_element051  label="C_element : 028"  # scripted group (container) (typed FeaturePython)
  n = 5
  ref = C_element
FEATURE [App::DocumentObjectGroupPython] H_element044  label="H_element : 023"  # scripted group (container) (typed FeaturePython)
  n = 5
  ref = H_element
FEATURE [App::DocumentObjectGroupPython] N_element020  label="N_element : 009"  # scripted group (container) (typed FeaturePython)
  n = 5
  ref = N_element
FEATURE [App::DocumentObjectGroupPython] O_element048  label="O_element : 024"  # scripted group (container) (typed FeaturePython)
  n = 1
  ref = O_element
FEATURE [App::DocumentObjectGroupPython] G4_GUANINE  # scripted group (container) (typed FeaturePython)
  Dunit = g/cm3
  Dvalue = 2.2
  Group = -> [C_element051,H_element044,N_element020,O_element048]
  conduct = 2
  density = 1
  expand = 3
  formula = G4_GUANINE
  name = G4_GUANINE
  specific = 4
FEATURE [App::DocumentObjectGroupPython] Ca_element012  label="Ca_element : 006"  # scripted group (container) (typed FeaturePython)
  n = 1
  ref = Ca_element
FEATURE [App::DocumentObjectGroupPython] S_element014  label="S_element : 005"  # scripted group (container) (typed FeaturePython)
  n = 1
  ref = S_element
FEATURE [App::DocumentObjectGroupPython] O_element049  label="O_element : 6"  # scripted group (container) (typed FeaturePython)
  n = 6
  ref = O_element
FEATURE [App::DocumentObjectGroupPython] H_element045  label="H_element : 024"  # scripted group (container) (typed FeaturePython)
  n = 4
  ref = H_element
FEATURE [App::DocumentObjectGroupPython] G4_GYPSUM  # scripted group (container) (typed FeaturePython)
  Dunit = g/cm3
  Dvalue = 2.32
  Group = -> [Ca_element012,S_element014,O_element049,H_element045]
  conduct = 2
  density = 1
  expand = 3
  formula = G4_GYPSUM
  name = G4_GYPSUM
  specific = 4
FEATURE [App::DocumentObjectGroupPython] C_element052  label="C_element : 7"  # scripted group (container) (typed FeaturePython)
  n = 7
  ref = C_element
FEATURE [App::DocumentObjectGroupPython] H_element046  label="H_element : 16"  # scripted group (container) (typed FeaturePython)
  n = 16
  ref = H_element
FEATURE [App::DocumentObjectGroupPython] G4_N_HEPTANE  label="G4_N-HEPTANE"  # scripted group (container) (typed FeaturePython)
  Dunit = g/cm3
  Dvalue = 0.68376
  Group = -> [C_element052,H_element046]
  conduct = 2
  density = 1
  expand = 3
  formula = G4_N-HEPTANE
  name = G4_N-HEPTANE
  specific = 4
FEATURE [App::DocumentObjectGroupPython] C_element053  label="C_element : 029"  # scripted group (container) (typed FeaturePython)
  n = 6
  ref = C_element
FEATURE [App::DocumentObjectGroupPython] H_element047  label="H_element : 14"  # scripted group (container) (typed FeaturePython)
  n = 14
  ref = H_element
FEATURE [App::DocumentObjectGroupPython] G4_N_HEXANE  label="G4_N-HEXANE"  # scripted group (container) (typed FeaturePython)
  Dunit = g/cm3
  Dvalue = 0.6603
  Group = -> [C_element053,H_element047]
  conduct = 2
  density = 1
  expand = 3
  formula = G4_N-HEXANE
  name = G4_N-HEXANE
  specific = 4
FEATURE [App::DocumentObjectGroupPython] C_element054  label="C_element : 22"  # scripted group (container) (typed FeaturePython)
  n = 22
  ref = C_element
FEATURE [App::DocumentObjectGroupPython] H_element048  label="H_element : 025"  # scripted group (container) (typed FeaturePython)
  n = 10
  ref = H_element
FEATURE [App::DocumentObjectGroupPython] N_element021  label="N_element : 010"  # scripted group (container) (typed FeaturePython)
  n = 2
  ref = N_element
FEATURE [App::DocumentObjectGroupPython] O_element050  label="O_element : 025"  # scripted group (container) (typed FeaturePython)
  n = 5
  ref = O_element
FEATURE [App::DocumentObjectGroupPython] G4_KAPTON  # scripted group (container) (typed FeaturePython)
  Dunit = g/cm3
  Dvalue = 1.42
  Group = -> [C_element054,H_element048,N_element021,O_element050]
  conduct = 2
  density = 1
  expand = 3
  formula = G4_KAPTON
  name = G4_KAPTON
  specific = 4
FEATURE [App::DocumentObjectGroupPython] La_element001  label="La_element : 1"  # scripted group (container) (typed FeaturePython)
  n = 1
  ref = La_element
FEATURE [App::DocumentObjectGroupPython] Br_element003  label="Br_element : 002"  # scripted group (container) (typed FeaturePython)
  n = 1
  ref = Br_element
FEATURE [App::DocumentObjectGroupPython] O_element051  label="O_element : 026"  # scripted group (container) (typed FeaturePython)
  n = 1
  ref = O_element
FEATURE [App::DocumentObjectGroupPython] G4_LANTHANUM_OXYBROMIDE  # scripted group (container) (typed FeaturePython)
  Dunit = g/cm3
  Dvalue = 6.28
  Group = -> [La_element001,Br_element003,O_element051]
  conduct = 2
  density = 1
  expand = 3
  formula = G4_LANTHANUM_OXYBROMIDE
  name = G4_LANTHANUM_OXYBROMIDE
  specific = 4
FEATURE [App::DocumentObjectGroupPython] La_element002  label="La_element : 2"  # scripted group (container) (typed FeaturePython)
  n = 2
  ref = La_element
FEATURE [App::DocumentObjectGroupPython] O_element052  label="O_element : 027"  # scripted group (container) (typed FeaturePython)
  n = 2
  ref = O_element
FEATURE [App::DocumentObjectGroupPython] S_element015  label="S_element : 006"  # scripted group (container) (typed FeaturePython)
  n = 1
  ref = S_element
FEATURE [App::DocumentObjectGroupPython] G4_LANTHANUM_OXYSULFIDE  # scripted group (container) (typed FeaturePython)
  Dunit = g/cm3
  Dvalue = 5.86
  Group = -> [La_element002,O_element052,S_element015]
  conduct = 2
  density = 1
  expand = 3
  formula = G4_LANTHANUM_OXYSULFIDE
  name = G4_LANTHANUM_OXYSULFIDE
  specific = 4
FEATURE [App::DocumentObjectGroupPython] O_element053  label="O_element : 0.072"  # scripted group (container) (typed FeaturePython)
  n = 0.071682
FEATURE [App::DocumentObjectGroupPython] Pb_element002  label="Pb_element : 0.928"  # scripted group (container) (typed FeaturePython)
  n = 0.928318
FEATURE [App::DocumentObjectGroupPython] G4_LEAD_OXIDE  # scripted group (container) (typed FeaturePython)
  Dunit = g/cm3
  Dvalue = 9.53
  Group = -> [O_element053,Pb_element002]
  conduct = 2
  density = 1
  expand = 3
  formula = G4_LEAD_OXIDE
  name = G4_LEAD_OXIDE
  specific = 4
FEATURE [App::DocumentObjectGroupPython] Li_element001  label="Li_element : 1"  # scripted group (container) (typed FeaturePython)
  n = 1
  ref = Li_element
FEATURE [App::DocumentObjectGroupPython] N_element022  label="N_element : 011"  # scripted group (container) (typed FeaturePython)
  n = 1
  ref = N_element
FEATURE [App::DocumentObjectGroupPython] H_element049  label="H_element : 026"  # scripted group (container) (typed FeaturePython)
  n = 2
  ref = H_element
FEATURE [App::DocumentObjectGroupPython] G4_LITHIUM_AMIDE  # scripted group (container) (typed FeaturePython)
  Dunit = g/cm3
  Dvalue = 1.178
  Group = -> [Li_element001,N_element022,H_element049]
  conduct = 2
  density = 1
  expand = 3
  formula = G4_LITHIUM_AMIDE
  name = G4_LITHIUM_AMIDE
  specific = 4
FEATURE [App::DocumentObjectGroupPython] Li_element002  label="Li_element : 2"  # scripted group (container) (typed FeaturePython)
  n = 2
  ref = Li_element
FEATURE [App::DocumentObjectGroupPython] C_element055  label="C_element : 030"  # scripted group (container) (typed FeaturePython)
  n = 1
  ref = C_element
FEATURE [App::DocumentObjectGroupPython] O_element054  label="O_element : 028"  # scripted group (container) (typed FeaturePython)
  n = 3
  ref = O_element
FEATURE [App::DocumentObjectGroupPython] G4_LITHIUM_CARBONATE  # scripted group (container) (typed FeaturePython)
  Dunit = g/cm3
  Dvalue = 2.11
  Group = -> [Li_element002,C_element055,O_element054]
  conduct = 2
  density = 1
  expand = 3
  formula = G4_LITHIUM_CARBONATE
  name = G4_LITHIUM_CARBONATE
  specific = 4
FEATURE [App::DocumentObjectGroupPython] Li_element003  label="Li_element : 003"  # scripted group (container) (typed FeaturePython)
  n = 1
  ref = Li_element
FEATURE [App::DocumentObjectGroupPython] F_element012  label="F_element : 004"  # scripted group (container) (typed FeaturePython)
  n = 1
  ref = F_element
FEATURE [App::DocumentObjectGroupPython] G4_LITHIUM_FLUORIDE  # scripted group (container) (typed FeaturePython)
  Dunit = g/cm3
  Dvalue = 2.635
  Group = -> [Li_element003,F_element012]
  conduct = 2
  density = 1
  expand = 3
  formula = G4_LITHIUM_FLUORIDE
  name = G4_LITHIUM_FLUORIDE
  specific = 4
FEATURE [App::DocumentObjectGroupPython] Li_element004  label="Li_element : 004"  # scripted group (container) (typed FeaturePython)
  n = 1
  ref = Li_element
FEATURE [App::DocumentObjectGroupPython] H_element050  label="H_element : 027"  # scripted group (container) (typed FeaturePython)
  n = 1
  ref = H_element
FEATURE [App::DocumentObjectGroupPython] G4_LITHIUM_HYDRIDE  # scripted group (container) (typed FeaturePython)
  Dunit = g/cm3
  Dvalue = 0.82
  Group = -> [Li_element004,H_element050]
  conduct = 2
  density = 1
  expand = 3
  formula = G4_LITHIUM_HYDRIDE
  name = G4_LITHIUM_HYDRIDE
  specific = 4
FEATURE [App::DocumentObjectGroupPython] Li_element005  label="Li_element : 005"  # scripted group (container) (typed FeaturePython)
  n = 1
  ref = Li_element
FEATURE [App::DocumentObjectGroupPython] I_element003  label="I_element : 002"  # scripted group (container) (typed FeaturePython)
  n = 1
  ref = I_element
FEATURE [App::DocumentObjectGroupPython] G4_LITHIUM_IODIDE  # scripted group (container) (typed FeaturePython)
  Dunit = g/cm3
  Dvalue = 3.494
  Group = -> [Li_element005,I_element003]
  conduct = 2
  density = 1
  expand = 3
  formula = G4_LITHIUM_IODIDE
  name = G4_LITHIUM_IODIDE
  specific = 4
FEATURE [App::DocumentObjectGroupPython] Li_element006  label="Li_element : 006"  # scripted group (container) (typed FeaturePython)
  n = 2
  ref = Li_element
FEATURE [App::DocumentObjectGroupPython] O_element055  label="O_element : 029"  # scripted group (container) (typed FeaturePython)
  n = 1
  ref = O_element
FEATURE [App::DocumentObjectGroupPython] G4_LITHIUM_OXIDE  # scripted group (container) (typed FeaturePython)
  Dunit = g/cm3
  Dvalue = 2.013
  Group = -> [Li_element006,O_element055]
  conduct = 2
  density = 1
  expand = 3
  formula = G4_LITHIUM_OXIDE
  name = G4_LITHIUM_OXIDE
  specific = 4
FEATURE [App::DocumentObjectGroupPython] Li_element007  label="Li_element : 007"  # scripted group (container) (typed FeaturePython)
  n = 2
  ref = Li_element
FEATURE [App::DocumentObjectGroupPython] B_element005  label="B_element : 005"  # scripted group (container) (typed FeaturePython)
  n = 4
  ref = B_element
FEATURE [App::DocumentObjectGroupPython] O_element056  label="O_element : 7"  # scripted group (container) (typed FeaturePython)
  n = 7
  ref = O_element
FEATURE [App::DocumentObjectGroupPython] G4_LITHIUM_TETRABORATE  # scripted group (container) (typed FeaturePython)
  Dunit = g/cm3
  Dvalue = 2.44
  Group = -> [Li_element007,B_element005,O_element056]
  conduct = 2
  density = 1
  expand = 3
  formula = G4_LITHIUM_TETRABORATE
  name = G4_LITHIUM_TETRABORATE
  specific = 4
FEATURE [App::DocumentObjectGroupPython] H_element051  label="H_element : 0.105"  # scripted group (container) (typed FeaturePython)
  n = 0.105
FEATURE [App::DocumentObjectGroupPython] C_element056  label="C_element : 0.083"  # scripted group (container) (typed FeaturePython)
  n = 0.083
FEATURE [App::DocumentObjectGroupPython] N_element023  label="N_element : 0.023"  # scripted group (container) (typed FeaturePython)
  n = 0.023
FEATURE [App::DocumentObjectGroupPython] O_element057  label="O_element : 0.779"  # scripted group (container) (typed FeaturePython)
  n = 0.779
FEATURE [App::DocumentObjectGroupPython] Na_element010  label="Na_element : 0.097"  # scripted group (container) (typed FeaturePython)
  n = 0.002
FEATURE [App::DocumentObjectGroupPython] P_element006  label="P_element : 0.105"  # scripted group (container) (typed FeaturePython)
  n = 0.001
FEATURE [App::DocumentObjectGroupPython] S_element016  label="S_element : 0.017"  # scripted group (container) (typed FeaturePython)
  n = 0.002
FEATURE [App::DocumentObjectGroupPython] Cl_element014  label="Cl_element : 0.587"  # scripted group (container) (typed FeaturePython)
  n = 0.003
FEATURE [App::DocumentObjectGroupPython] K_element005  label="K_element : 0.015"  # scripted group (container) (typed FeaturePython)
  n = 0.002
FEATURE [App::DocumentObjectGroupPython] G4_LUNG_ICRP  # scripted group (container) (typed FeaturePython)
  Dunit = g/cm3
  Dvalue = 1.04
  Group = -> [H_element051,C_element056,N_element023,O_element057,Na_element010,P_element006,S_element016,Cl_element014,K_element005]
  conduct = 2
  density = 1
  expand = 3
  formula = G4_LUNG_ICRP
  name = G4_LUNG_ICRP
  specific = 4
FEATURE [App::DocumentObjectGroupPython] H_element052  label="H_element : 0.116"  # scripted group (container) (typed FeaturePython)
  n = 0.114318
FEATURE [App::DocumentObjectGroupPython] C_element057  label="C_element : 0.656"  # scripted group (container) (typed FeaturePython)
  n = 0.655824
FEATURE [App::DocumentObjectGroupPython] O_element058  label="O_element : 0.092"  # scripted group (container) (typed FeaturePython)
  n = 0.0921831
FEATURE [App::DocumentObjectGroupPython] Mg_element004  label="Mg_element : 0.135"  # scripted group (container) (typed FeaturePython)
  n = 0.134792
FEATURE [App::DocumentObjectGroupPython] Ca_element013  label="Ca_element : 0.003"  # scripted group (container) (typed FeaturePython)
  n = 0.002883
FEATURE [App::DocumentObjectGroupPython] G4_M3_WAX  # scripted group (container) (typed FeaturePython)
  Dunit = g/cm3
  Dvalue = 1.05
  Group = -> [H_element052,C_element057,O_element058,Mg_element004,Ca_element013]
  conduct = 2
  density = 1
  expand = 3
  formula = G4_M3_WAX
  name = G4_M3_WAX
  specific = 4
FEATURE [App::DocumentObjectGroupPython] Mg_element005  label="Mg_element : 1"  # scripted group (container) (typed FeaturePython)
  n = 1
  ref = Mg_element
FEATURE [App::DocumentObjectGroupPython] C_element058  label="C_element : 031"  # scripted group (container) (typed FeaturePython)
  n = 1
  ref = C_element
FEATURE [App::DocumentObjectGroupPython] O_element059  label="O_element : 030"  # scripted group (container) (typed FeaturePython)
  n = 3
  ref = O_element
FEATURE [App::DocumentObjectGroupPython] G4_MAGNESIUM_CARBONATE  # scripted group (container) (typed FeaturePython)
  Dunit = g/cm3
  Dvalue = 2.958
  Group = -> [Mg_element005,C_element058,O_element059]
  conduct = 2
  density = 1
  expand = 3
  formula = G4_MAGNESIUM_CARBONATE
  name = G4_MAGNESIUM_CARBONATE
  specific = 4
FEATURE [App::DocumentObjectGroupPython] Mg_element006  label="Mg_element : 002"  # scripted group (container) (typed FeaturePython)
  n = 1
  ref = Mg_element
FEATURE [App::DocumentObjectGroupPython] F_element013  label="F_element : 005"  # scripted group (container) (typed FeaturePython)
  n = 2
  ref = F_element
FEATURE [App::DocumentObjectGroupPython] G4_MAGNESIUM_FLUORIDE  # scripted group (container) (typed FeaturePython)
  Dunit = g/cm3
  Dvalue = 3
  Group = -> [Mg_element006,F_element013]
  conduct = 2
  density = 1
  expand = 3
  formula = G4_MAGNESIUM_FLUORIDE
  name = G4_MAGNESIUM_FLUORIDE
  specific = 4
FEATURE [App::DocumentObjectGroupPython] Mg_element007  label="Mg_element : 003"  # scripted group (container) (typed FeaturePython)
  n = 1
  ref = Mg_element
FEATURE [App::DocumentObjectGroupPython] O_element060  label="O_element : 031"  # scripted group (container) (typed FeaturePython)
  n = 1
  ref = O_element
FEATURE [App::DocumentObjectGroupPython] G4_MAGNESIUM_OXIDE  # scripted group (container) (typed FeaturePython)
  Dunit = g/cm3
  Dvalue = 3.58
  Group = -> [Mg_element007,O_element060]
  conduct = 2
  density = 1
  expand = 3
  formula = G4_MAGNESIUM_OXIDE
  name = G4_MAGNESIUM_OXIDE
  specific = 4
FEATURE [App::DocumentObjectGroupPython] Mg_element008  label="Mg_element : 004"  # scripted group (container) (typed FeaturePython)
  n = 1
  ref = Mg_element
FEATURE [App::DocumentObjectGroupPython] B_element006  label="B_element : 006"  # scripted group (container) (typed FeaturePython)
  n = 4
  ref = B_element
FEATURE [App::DocumentObjectGroupPython] O_element061  label="O_element : 032"  # scripted group (container) (typed FeaturePython)
  n = 7
  ref = O_element
FEATURE [App::DocumentObjectGroupPython] G4_MAGNESIUM_TETRABORATE  # scripted group (container) (typed FeaturePython)
  Dunit = g/cm3
  Dvalue = 2.53
  Group = -> [Mg_element008,B_element006,O_element061]
  conduct = 2
  density = 1
  expand = 3
  formula = G4_MAGNESIUM_TETRABORATE
  name = G4_MAGNESIUM_TETRABORATE
  specific = 4
FEATURE [App::DocumentObjectGroupPython] Hg_element001  label="Hg_element : 1"  # scripted group (container) (typed FeaturePython)
  n = 1
  ref = Hg_element
FEATURE [App::DocumentObjectGroupPython] I_element004  label="I_element : 2"  # scripted group (container) (typed FeaturePython)
  n = 2
  ref = I_element
FEATURE [App::DocumentObjectGroupPython] G4_MERCURIC_IODIDE  # scripted group (container) (typed FeaturePython)
  Dunit = g/cm3
  Dvalue = 6.36
  Group = -> [Hg_element001,I_element004]
  conduct = 2
  density = 1
  expand = 3
  formula = G4_MERCURIC_IODIDE
  name = G4_MERCURIC_IODIDE
  specific = 4
FEATURE [App::DocumentObjectGroupPython] C_element059  label="C_element : 032"  # scripted group (container) (typed FeaturePython)
  n = 1
  ref = C_element
FEATURE [App::DocumentObjectGroupPython] H_element053  label="H_element : 028"  # scripted group (container) (typed FeaturePython)
  n = 4
  ref = H_element
FEATURE [App::DocumentObjectGroupPython] G4_METHANE  # scripted group (container) (typed FeaturePython)
  Dunit = g/cm3
  Dvalue = 0.000667151
  Group = -> [C_element059,H_element053]
  conduct = 2
  density = 1
  expand = 3
  formula = G4_METHANE
  name = G4_METHANE
  specific = 4
FEATURE [App::DocumentObjectGroupPython] C_element060  label="C_element : 033"  # scripted group (container) (typed FeaturePython)
  n = 1
  ref = C_element
FEATURE [App::DocumentObjectGroupPython] H_element054  label="H_element : 029"  # scripted group (container) (typed FeaturePython)
  n = 4
  ref = H_element
FEATURE [App::DocumentObjectGroupPython] O_element062  label="O_element : 033"  # scripted group (container) (typed FeaturePython)
  n = 1
  ref = O_element
FEATURE [App::DocumentObjectGroupPython] G4_METHANOL  # scripted group (container) (typed FeaturePython)
  Dunit = g/cm3
  Dvalue = 0.7914
  Group = -> [C_element060,H_element054,O_element062]
  conduct = 2
  density = 1
  expand = 3
  formula = G4_METHANOL
  name = G4_METHANOL
  specific = 4
FEATURE [App::DocumentObjectGroupPython] H_element055  label="H_element : 0.134"  # scripted group (container) (typed FeaturePython)
  n = 0.13404
FEATURE [App::DocumentObjectGroupPython] C_element061  label="C_element : 0.778"  # scripted group (container) (typed FeaturePython)
  n = 0.77796
FEATURE [App::DocumentObjectGroupPython] O_element063  label="O_element : 0.035"  # scripted group (container) (typed FeaturePython)
  n = 0.03502
FEATURE [App::DocumentObjectGroupPython] Mg_element009  label="Mg_element : 0.039"  # scripted group (container) (typed FeaturePython)
  n = 0.038594
FEATURE [App::DocumentObjectGroupPython] Ti_element002  label="Ti_element : 0.014"  # scripted group (container) (typed FeaturePython)
  n = 0.014386
FEATURE [App::DocumentObjectGroupPython] G4_MIX_D_WAX  # scripted group (container) (typed FeaturePython)
  Dunit = g/cm3
  Dvalue = 0.99
  Group = -> [H_element055,C_element061,O_element063,Mg_element009,Ti_element002]
  conduct = 2
  density = 1
  expand = 3
  formula = G4_MIX_D_WAX
  name = G4_MIX_D_WAX
  specific = 4
FEATURE [App::DocumentObjectGroupPython] H_element056  label="H_element : 0.135"  # scripted group (container) (typed FeaturePython)
  n = 0.081192
FEATURE [App::DocumentObjectGroupPython] C_element062  label="C_element : 0.583"  # scripted group (container) (typed FeaturePython)
  n = 0.583442
FEATURE [App::DocumentObjectGroupPython] N_element024  label="N_element : 0.018"  # scripted group (container) (typed FeaturePython)
  n = 0.017798
FEATURE [App::DocumentObjectGroupPython] O_element064  label="O_element : 0.186"  # scripted group (container) (typed FeaturePython)
  n = 0.186381
FEATURE [App::DocumentObjectGroupPython] Mg_element010  label="Mg_element : 0.130"  # scripted group (container) (typed FeaturePython)
  n = 0.130287
FEATURE [App::DocumentObjectGroupPython] Cl_element015  label="Cl_element : 0.588"  # scripted group (container) (typed FeaturePython)
  n = 0.0009
FEATURE [App::DocumentObjectGroupPython] G4_MS20_TISSUE  # scripted group (container) (typed FeaturePython)
  Dunit = g/cm3
  Dvalue = 1
  Group = -> [H_element056,C_element062,N_element024,O_element064,Mg_element010,Cl_element015]
  conduct = 2
  density = 1
  expand = 3
  formula = G4_MS20_TISSUE
  name = G4_MS20_TISSUE
  specific = 4
FEATURE [App::DocumentObjectGroupPython] H_element057  label="H_element : 0.136"  # scripted group (container) (typed FeaturePython)
  n = 0.102
FEATURE [App::DocumentObjectGroupPython] C_element063  label="C_element : 0.143"  # scripted group (container) (typed FeaturePython)
  n = 0.143
FEATURE [App::DocumentObjectGroupPython] N_element025  label="N_element : 0.034"  # scripted group (container) (typed FeaturePython)
  n = 0.034
FEATURE [App::DocumentObjectGroupPython] O_element065  label="O_element : 0.710"  # scripted group (container) (typed FeaturePython)
  n = 0.71
FEATURE [App::DocumentObjectGroupPython] Na_element011  label="Na_element : 0.098"  # scripted group (container) (typed FeaturePython)
  n = 0.001
FEATURE [App::DocumentObjectGroupPython] P_element007  label="P_element : 0.002"  # scripted group (container) (typed FeaturePython)
  n = 0.002
FEATURE [App::DocumentObjectGroupPython] S_element017  label="S_element : 0.018"  # scripted group (container) (typed FeaturePython)
  n = 0.003
FEATURE [App::DocumentObjectGroupPython] Cl_element016  label="Cl_element : 0.589"  # scripted group (container) (typed FeaturePython)
  n = 0.001
FEATURE [App::DocumentObjectGroupPython] K_element006  label="K_element : 0.004"  # scripted group (container) (typed FeaturePython)
  n = 0.004
FEATURE [App::DocumentObjectGroupPython] G4_MUSCLE_SKELETAL_ICRP  # scripted group (container) (typed FeaturePython)
  Dunit = g/cm3
  Dvalue = 1.05
  Group = -> [H_element057,C_element063,N_element025,O_element065,Na_element011,P_element007,S_element017,Cl_element016,K_element006]
  conduct = 2
  density = 1
  expand = 3
  formula = G4_MUSCLE_SKELETAL_ICRP
  name = G4_MUSCLE_SKELETAL_ICRP
  specific = 4
FEATURE [App::DocumentObjectGroupPython] H_element058  label="H_element : 0.137"  # scripted group (container) (typed FeaturePython)
  n = 0.102102
FEATURE [App::DocumentObjectGroupPython] C_element064  label="C_element : 0.123"  # scripted group (container) (typed FeaturePython)
  n = 0.123123
FEATURE [App::DocumentObjectGroupPython] N_element026  label="N_element : 0.756"  # scripted group (container) (typed FeaturePython)
  n = 0.035035
FEATURE [App::DocumentObjectGroupPython] O_element066  label="O_element : 0.730"  # scripted group (container) (typed FeaturePython)
  n = 0.72973
FEATURE [App::DocumentObjectGroupPython] Na_element012  label="Na_element : 0.099"  # scripted group (container) (typed FeaturePython)
  n = 0.001001
FEATURE [App::DocumentObjectGroupPython] P_element008  label="P_element : 0.106"  # scripted group (container) (typed FeaturePython)
  n = 0.002002
FEATURE [App::DocumentObjectGroupPython] S_element018  label="S_element : 0.019"  # scripted group (container) (typed FeaturePython)
  n = 0.004004
FEATURE [App::DocumentObjectGroupPython] K_element007  label="K_element : 0.016"  # scripted group (container) (typed FeaturePython)
  n = 0.003003
FEATURE [App::DocumentObjectGroupPython] G4_MUSCLE_STRIATED_ICRU  # scripted group (container) (typed FeaturePython)
  Dunit = g/cm3
  Dvalue = 1.04
  Group = -> [H_element058,C_element064,N_element026,O_element066,Na_element012,P_element008,S_element018,K_element007]
  conduct = 2
  density = 1
  expand = 3
  formula = G4_MUSCLE_STRIATED_ICRU
  name = G4_MUSCLE_STRIATED_ICRU
  specific = 4
FEATURE [App::DocumentObjectGroupPython] H_element059  label="H_element : 0.098"  # scripted group (container) (typed FeaturePython)
  n = 0.0982341
FEATURE [App::DocumentObjectGroupPython] C_element065  label="C_element : 0.156"  # scripted group (container) (typed FeaturePython)
  n = 0.156214
FEATURE [App::DocumentObjectGroupPython] N_element027  label="N_element : 0.757"  # scripted group (container) (typed FeaturePython)
  n = 0.035451
FEATURE [App::DocumentObjectGroupPython] O_element067  label="O_element : 0.880"  # scripted group (container) (typed FeaturePython)
  n = 0.710101
FEATURE [App::DocumentObjectGroupPython] G4_MUSCLE_WITH_SUCROSE  # scripted group (container) (typed FeaturePython)
  Dunit = g/cm3
  Dvalue = 1.11
  Group = -> [H_element059,C_element065,N_element027,O_element067]
  conduct = 2
  density = 1
  expand = 3
  formula = G4_MUSCLE_WITH_SUCROSE
  name = G4_MUSCLE_WITH_SUCROSE
  specific = 4
FEATURE [App::DocumentObjectGroupPython] H_element060  label="H_element : 0.138"  # scripted group (container) (typed FeaturePython)
  n = 0.101969
FEATURE [App::DocumentObjectGroupPython] C_element066  label="C_element : 0.120"  # scripted group (container) (typed FeaturePython)
  n = 0.120058
FEATURE [App::DocumentObjectGroupPython] N_element028  label="N_element : 0.758"  # scripted group (container) (typed FeaturePython)
  n = 0.035451
FEATURE [App::DocumentObjectGroupPython] O_element068  label="O_element : 0.743"  # scripted group (container) (typed FeaturePython)
  n = 0.742522
FEATURE [App::DocumentObjectGroupPython] G4_MUSCLE_WITHOUT_SUCROSE  # scripted group (container) (typed FeaturePython)
  Dunit = g/cm3
  Dvalue = 1.07
  Group = -> [H_element060,C_element066,N_element028,O_element068]
  conduct = 2
  density = 1
  expand = 3
  formula = G4_MUSCLE_WITHOUT_SUCROSE
  name = G4_MUSCLE_WITHOUT_SUCROSE
  specific = 4
FEATURE [App::DocumentObjectGroupPython] C_element067  label="C_element : 10"  # scripted group (container) (typed FeaturePython)
  n = 10
  ref = C_element
FEATURE [App::DocumentObjectGroupPython] H_element061  label="H_element : 030"  # scripted group (container) (typed FeaturePython)
  n = 8
  ref = H_element
FEATURE [App::DocumentObjectGroupPython] G4_NAPHTHALENE  # scripted group (container) (typed FeaturePython)
  Dunit = g/cm3
  Dvalue = 1.145
  Group = -> [C_element067,H_element061]
  conduct = 2
  density = 1
  expand = 3
  formula = G4_NAPHTHALENE
  name = G4_NAPHTHALENE
  specific = 4
FEATURE [App::DocumentObjectGroupPython] C_element068  label="C_element : 034"  # scripted group (container) (typed FeaturePython)
  n = 6
  ref = C_element
FEATURE [App::DocumentObjectGroupPython] H_element062  label="H_element : 031"  # scripted group (container) (typed FeaturePython)
  n = 5
  ref = H_element
FEATURE [App::DocumentObjectGroupPython] N_element029  label="N_element : 012"  # scripted group (container) (typed FeaturePython)
  n = 1
  ref = N_element
FEATURE [App::DocumentObjectGroupPython] O_element069  label="O_element : 034"  # scripted group (container) (typed FeaturePython)
  n = 2
  ref = O_element
FEATURE [App::DocumentObjectGroupPython] G4_NITROBENZENE  # scripted group (container) (typed FeaturePython)
  Dunit = g/cm3
  Dvalue = 1.19867
  Group = -> [C_element068,H_element062,N_element029,O_element069]
  conduct = 2
  density = 1
  expand = 3
  formula = G4_NITROBENZENE
  name = G4_NITROBENZENE
  specific = 4
FEATURE [App::DocumentObjectGroupPython] N_element030  label="N_element : 013"  # scripted group (container) (typed FeaturePython)
  n = 2
  ref = N_element
FEATURE [App::DocumentObjectGroupPython] O_element070  label="O_element : 035"  # scripted group (container) (typed FeaturePython)
  n = 1
  ref = O_element
FEATURE [App::DocumentObjectGroupPython] G4_NITROUS_OXIDE  # scripted group (container) (typed FeaturePython)
  Dunit = g/cm3
  Dvalue = 0.00183094
  Group = -> [N_element030,O_element070]
  conduct = 2
  density = 1
  expand = 3
  formula = G4_NITROUS_OXIDE
  name = G4_NITROUS_OXIDE
  specific = 4
FEATURE [App::DocumentObjectGroupPython] H_element063  label="H_element : 0.104"  # scripted group (container) (typed FeaturePython)
  n = 0.103509
FEATURE [App::DocumentObjectGroupPython] C_element069  label="C_element : 0.648"  # scripted group (container) (typed FeaturePython)
  n = 0.648416
FEATURE [App::DocumentObjectGroupPython] N_element031  label="N_element : 0.100"  # scripted group (container) (typed FeaturePython)
  n = 0.0995361
FEATURE [App::DocumentObjectGroupPython] O_element071  label="O_element : 0.149"  # scripted group (container) (typed FeaturePython)
  n = 0.148539
FEATURE [App::DocumentObjectGroupPython] G4_NYLON_8062  label="G4_NYLON-8062"  # scripted group (container) (typed FeaturePython)
  Dunit = g/cm3
  Dvalue = 1.08
  Group = -> [H_element063,C_element069,N_element031,O_element071]
  conduct = 2
  density = 1
  expand = 3
  formula = G4_NYLON-8062
  name = G4_NYLON-8062
  specific = 4
FEATURE [App::DocumentObjectGroupPython] C_element070  label="C_element : 035"  # scripted group (container) (typed FeaturePython)
  n = 6
  ref = C_element
FEATURE [App::DocumentObjectGroupPython] H_element064  label="H_element : 11"  # scripted group (container) (typed FeaturePython)
  n = 11
  ref = H_element
FEATURE [App::DocumentObjectGroupPython] N_element032  label="N_element : 014"  # scripted group (container) (typed FeaturePython)
  n = 1
  ref = N_element
FEATURE [App::DocumentObjectGroupPython] O_element072  label="O_element : 036"  # scripted group (container) (typed FeaturePython)
  n = 1
  ref = O_element
FEATURE [App::DocumentObjectGroupPython] G4_NYLON_6_6  label="G4_NYLON-6-6"  # scripted group (container) (typed FeaturePython)
  Dunit = g/cm3
  Dvalue = 1.14
  Group = -> [C_element070,H_element064,N_element032,O_element072]
  conduct = 2
  density = 1
  expand = 3
  formula = G4_NYLON-6-6
  name = G4_NYLON-6-6
  specific = 4
FEATURE [App::DocumentObjectGroupPython] H_element065  label="H_element : 0.139"  # scripted group (container) (typed FeaturePython)
  n = 0.107062
FEATURE [App::DocumentObjectGroupPython] C_element071  label="C_element : 0.680"  # scripted group (container) (typed FeaturePython)
  n = 0.680449
FEATURE [App::DocumentObjectGroupPython] N_element033  label="N_element : 0.099"  # scripted group (container) (typed FeaturePython)
  n = 0.099189
FEATURE [App::DocumentObjectGroupPython] O_element073  label="O_element : 0.113"  # scripted group (container) (typed FeaturePython)
  n = 0.1133
FEATURE [App::DocumentObjectGroupPython] G4_NYLON_6_10  label="G4_NYLON-6-10"  # scripted group (container) (typed FeaturePython)
  Dunit = g/cm3
  Dvalue = 1.14
  Group = -> [H_element065,C_element071,N_element033,O_element073]
  conduct = 2
  density = 1
  expand = 3
  formula = G4_NYLON-6-10
  name = G4_NYLON-6-10
  specific = 4
FEATURE [App::DocumentObjectGroupPython] H_element066  label="H_element : 0.140"  # scripted group (container) (typed FeaturePython)
  n = 0.115476
FEATURE [App::DocumentObjectGroupPython] C_element072  label="C_element : 0.721"  # scripted group (container) (typed FeaturePython)
  n = 0.720818
FEATURE [App::DocumentObjectGroupPython] N_element034  label="N_element : 0.076"  # scripted group (container) (typed FeaturePython)
  n = 0.0764169
FEATURE [App::DocumentObjectGroupPython] O_element074  label="O_element : 0.087"  # scripted group (container) (typed FeaturePython)
  n = 0.0872889
FEATURE [App::DocumentObjectGroupPython] G4_NYLON_11_RILSAN  label="G4_NYLON-11_RILSAN"  # scripted group (container) (typed FeaturePython)
  Dunit = g/cm3
  Dvalue = 1.425
  Group = -> [H_element066,C_element072,N_element034,O_element074]
  conduct = 2
  density = 1
  expand = 3
  formula = G4_NYLON-11_RILSAN
  name = G4_NYLON-11_RILSAN
  specific = 4
FEATURE [App::DocumentObjectGroupPython] C_element073  label="C_element : 8"  # scripted group (container) (typed FeaturePython)
  n = 8
  ref = C_element
FEATURE [App::DocumentObjectGroupPython] H_element067  label="H_element : 18"  # scripted group (container) (typed FeaturePython)
  n = 18
  ref = H_element
FEATURE [App::DocumentObjectGroupPython] G4_OCTANE  # scripted group (container) (typed FeaturePython)
  Dunit = g/cm3
  Dvalue = 0.7026
  Group = -> [C_element073,H_element067]
  conduct = 2
  density = 1
  expand = 3
  formula = G4_OCTANE
  name = G4_OCTANE
  specific = 4
FEATURE [App::DocumentObjectGroupPython] C_element074  label="C_element : 25"  # scripted group (container) (typed FeaturePython)
  n = 25
  ref = C_element
FEATURE [App::DocumentObjectGroupPython] H_element068  label="H_element : 52"  # scripted group (container) (typed FeaturePython)
  n = 52
  ref = H_element
FEATURE [App::DocumentObjectGroupPython] G4_PARAFFIN  # scripted group (container) (typed FeaturePython)
  Dunit = g/cm3
  Dvalue = 0.93
  Group = -> [C_element074,H_element068]
  conduct = 2
  density = 1
  expand = 3
  formula = G4_PARAFFIN
  name = G4_PARAFFIN
  specific = 4
FEATURE [App::DocumentObjectGroupPython] C_element075  label="C_element : 036"  # scripted group (container) (typed FeaturePython)
  n = 5
  ref = C_element
FEATURE [App::DocumentObjectGroupPython] H_element069  label="H_element : 032"  # scripted group (container) (typed FeaturePython)
  n = 12
  ref = H_element
FEATURE [App::DocumentObjectGroupPython] G4_N_PENTANE  label="G4_N-PENTANE"  # scripted group (container) (typed FeaturePython)
  Dunit = g/cm3
  Dvalue = 0.6262
  Group = -> [C_element075,H_element069]
  conduct = 2
  density = 1
  expand = 3
  formula = G4_N-PENTANE
  name = G4_N-PENTANE
  specific = 4
FEATURE [App::DocumentObjectGroupPython] H_element070  label="H_element : 0.014"  # scripted group (container) (typed FeaturePython)
  n = 0.0141
FEATURE [App::DocumentObjectGroupPython] C_element076  label="C_element : 0.072"  # scripted group (container) (typed FeaturePython)
  n = 0.072261
FEATURE [App::DocumentObjectGroupPython] N_element035  label="N_element : 0.019"  # scripted group (container) (typed FeaturePython)
  n = 0.01932
FEATURE [App::DocumentObjectGroupPython] O_element075  label="O_element : 0.066"  # scripted group (container) (typed FeaturePython)
  n = 0.066101
FEATURE [App::DocumentObjectGroupPython] S_element019  label="S_element : 0.020"  # scripted group (container) (typed FeaturePython)
  n = 0.00189
FEATURE [App::DocumentObjectGroupPython] Br_element004  label="Br_element : 0.349"  # scripted group (container) (typed FeaturePython)
  n = 0.349103
FEATURE [App::DocumentObjectGroupPython] Ag_element001  label="Ag_element : 0.474"  # scripted group (container) (typed FeaturePython)
  n = 0.474105
FEATURE [App::DocumentObjectGroupPython] I_element005  label="I_element : 0.003"  # scripted group (container) (typed FeaturePython)
  n = 0.00312
FEATURE [App::DocumentObjectGroupPython] G4_PHOTO_EMULSION  # scripted group (container) (typed FeaturePython)
  Dunit = g/cm3
  Dvalue = 3.815
  Group = -> [H_element070,C_element076,N_element035,O_element075,S_element019,Br_element004,Ag_element001,I_element005]
  conduct = 2
  density = 1
  expand = 3
  formula = G4_PHOTO_EMULSION
  name = G4_PHOTO_EMULSION
  specific = 4
FEATURE [App::DocumentObjectGroupPython] C_element077  label="C_element : 9"  # scripted group (container) (typed FeaturePython)
  n = 9
  ref = C_element
FEATURE [App::DocumentObjectGroupPython] H_element071  label="H_element : 033"  # scripted group (container) (typed FeaturePython)
  n = 10
  ref = H_element
FEATURE [App::DocumentObjectGroupPython] G4_PLASTIC_SC_VINYLTOLUENE  # scripted group (container) (typed FeaturePython)
  Dunit = g/cm3
  Dvalue = 1.032
  Group = -> [C_element077,H_element071]
  conduct = 2
  density = 1
  expand = 3
  formula = G4_PLASTIC_SC_VINYLTOLUENE
  name = G4_PLASTIC_SC_VINYLTOLUENE
  specific = 4
FEATURE [App::DocumentObjectGroupPython] Pu_element001  label="Pu_element : 1"  # scripted group (container) (typed FeaturePython)
  n = 1
  ref = Pu_element
FEATURE [App::DocumentObjectGroupPython] O_element076  label="O_element : 037"  # scripted group (container) (typed FeaturePython)
  n = 2
  ref = O_element
FEATURE [App::DocumentObjectGroupPython] G4_PLUTONIUM_DIOXIDE  # scripted group (container) (typed FeaturePython)
  Dunit = g/cm3
  Dvalue = 11.46
  Group = -> [Pu_element001,O_element076]
  conduct = 2
  density = 1
  expand = 3
  formula = G4_PLUTONIUM_DIOXIDE
  name = G4_PLUTONIUM_DIOXIDE
  specific = 4
FEATURE [App::DocumentObjectGroupPython] C_element078  label="C_element : 037"  # scripted group (container) (typed FeaturePython)
  n = 3
  ref = C_element
FEATURE [App::DocumentObjectGroupPython] H_element072  label="H_element : 034"  # scripted group (container) (typed FeaturePython)
  n = 3
  ref = H_element
FEATURE [App::DocumentObjectGroupPython] N_element036  label="N_element : 015"  # scripted group (container) (typed FeaturePython)
  n = 1
  ref = N_element
FEATURE [App::DocumentObjectGroupPython] G4_POLYACRYLONITRILE  # scripted group (container) (typed FeaturePython)
  Dunit = g/cm3
  Dvalue = 1.17
  Group = -> [C_element078,H_element072,N_element036]
  conduct = 2
  density = 1
  expand = 3
  formula = G4_POLYACRYLONITRILE
  name = G4_POLYACRYLONITRILE
  specific = 4
FEATURE [App::DocumentObjectGroupPython] C_element079  label="C_element : 16"  # scripted group (container) (typed FeaturePython)
  n = 16
  ref = C_element
FEATURE [App::DocumentObjectGroupPython] H_element073  label="H_element : 035"  # scripted group (container) (typed FeaturePython)
  n = 14
  ref = H_element
FEATURE [App::DocumentObjectGroupPython] O_element077  label="O_element : 038"  # scripted group (container) (typed FeaturePython)
  n = 3
  ref = O_element
FEATURE [App::DocumentObjectGroupPython] G4_POLYCARBONATE  # scripted group (container) (typed FeaturePython)
  Dunit = g/cm3
  Dvalue = 1.2
  Group = -> [C_element079,H_element073,O_element077]
  conduct = 2
  density = 1
  expand = 3
  formula = G4_POLYCARBONATE
  name = G4_POLYCARBONATE
  specific = 4
FEATURE [App::DocumentObjectGroupPython] C_element080  label="C_element : 038"  # scripted group (container) (typed FeaturePython)
  n = 8
  ref = C_element
FEATURE [App::DocumentObjectGroupPython] H_element074  label="H_element : 036"  # scripted group (container) (typed FeaturePython)
  n = 7
  ref = H_element
FEATURE [App::DocumentObjectGroupPython] Cl_element017  label="Cl_element : 007"  # scripted group (container) (typed FeaturePython)
  n = 1
  ref = Cl_element
FEATURE [App::DocumentObjectGroupPython] G4_POLYCHLOROSTYRENE  # scripted group (container) (typed FeaturePython)
  Dunit = g/cm3
  Dvalue = 1.3
  Group = -> [C_element080,H_element074,Cl_element017]
  conduct = 2
  density = 1
  expand = 3
  formula = G4_POLYCHLOROSTYRENE
  name = G4_POLYCHLOROSTYRENE
  specific = 4
FEATURE [App::DocumentObjectGroupPython] C_element081  label="C_element : 039"  # scripted group (container) (typed FeaturePython)
  n = 1
  ref = C_element
FEATURE [App::DocumentObjectGroupPython] H_element075  label="H_element : 037"  # scripted group (container) (typed FeaturePython)
  n = 2
  ref = H_element
FEATURE [App::DocumentObjectGroupPython] G4_POLYETHYLENE  # scripted group (container) (typed FeaturePython)
  Dunit = g/cm3
  Dvalue = 0.94
  Group = -> [C_element081,H_element075]
  conduct = 2
  density = 1
  expand = 3
  formula = G4_POLYETHYLENE
  name = G4_POLYETHYLENE
  specific = 4
FEATURE [App::DocumentObjectGroupPython] C_element082  label="C_element : 040"  # scripted group (container) (typed FeaturePython)
  n = 10
  ref = C_element
FEATURE [App::DocumentObjectGroupPython] H_element076  label="H_element : 038"  # scripted group (container) (typed FeaturePython)
  n = 8
  ref = H_element
FEATURE [App::DocumentObjectGroupPython] O_element078  label="O_element : 039"  # scripted group (container) (typed FeaturePython)
  n = 4
  ref = O_element
FEATURE [App::DocumentObjectGroupPython] G4_MYLAR  # scripted group (container) (typed FeaturePython)
  Dunit = g/cm3
  Dvalue = 1.4
  Group = -> [C_element082,H_element076,O_element078]
  conduct = 2
  density = 1
  expand = 3
  formula = G4_MYLAR
  name = G4_MYLAR
  specific = 4
FEATURE [App::DocumentObjectGroupPython] C_element083  label="C_element : 041"  # scripted group (container) (typed FeaturePython)
  n = 5
  ref = C_element
FEATURE [App::DocumentObjectGroupPython] H_element077  label="H_element : 039"  # scripted group (container) (typed FeaturePython)
  n = 8
  ref = H_element
FEATURE [App::DocumentObjectGroupPython] O_element079  label="O_element : 040"  # scripted group (container) (typed FeaturePython)
  n = 2
  ref = O_element
FEATURE [App::DocumentObjectGroupPython] G4_PLEXIGLASS  # scripted group (container) (typed FeaturePython)
  Dunit = g/cm3
  Dvalue = 1.19
  Group = -> [C_element083,H_element077,O_element079]
  conduct = 2
  density = 1
  expand = 3
  formula = G4_PLEXIGLASS
  name = G4_PLEXIGLASS
  specific = 4
FEATURE [App::DocumentObjectGroupPython] C_element084  label="C_element : 042"  # scripted group (container) (typed FeaturePython)
  n = 1
  ref = C_element
FEATURE [App::DocumentObjectGroupPython] H_element078  label="H_element : 040"  # scripted group (container) (typed FeaturePython)
  n = 2
  ref = H_element
FEATURE [App::DocumentObjectGroupPython] O_element080  label="O_element : 041"  # scripted group (container) (typed FeaturePython)
  n = 1
  ref = O_element
FEATURE [App::DocumentObjectGroupPython] G4_POLYOXYMETHYLENE  # scripted group (container) (typed FeaturePython)
  Dunit = g/cm3
  Dvalue = 1.425
  Group = -> [C_element084,H_element078,O_element080]
  conduct = 2
  density = 1
  expand = 3
  formula = G4_POLYOXYMETHYLENE
  name = G4_POLYOXYMETHYLENE
  specific = 4
FEATURE [App::DocumentObjectGroupPython] C_element085  label="C_element : 043"  # scripted group (container) (typed FeaturePython)
  n = 2
  ref = C_element
FEATURE [App::DocumentObjectGroupPython] H_element079  label="H_element : 041"  # scripted group (container) (typed FeaturePython)
  n = 4
  ref = H_element
FEATURE [App::DocumentObjectGroupPython] G4_POLYPROPYLENE  # scripted group (container) (typed FeaturePython)
  Dunit = g/cm3
  Dvalue = 0.9
  Group = -> [C_element085,H_element079]
  conduct = 2
  density = 1
  expand = 3
  formula = G4_POLYPROPYLENE
  name = G4_POLYPROPYLENE
  specific = 4
FEATURE [App::DocumentObjectGroupPython] C_element086  label="C_element : 044"  # scripted group (container) (typed FeaturePython)
  n = 8
  ref = C_element
FEATURE [App::DocumentObjectGroupPython] H_element080  label="H_element : 042"  # scripted group (container) (typed FeaturePython)
  n = 8
  ref = H_element
FEATURE [App::DocumentObjectGroupPython] G4_POLYSTYRENE  # scripted group (container) (typed FeaturePython)
  Dunit = g/cm3
  Dvalue = 1.06
  Group = -> [C_element086,H_element080]
  conduct = 2
  density = 1
  expand = 3
  formula = G4_POLYSTYRENE
  name = G4_POLYSTYRENE
  specific = 4
FEATURE [App::DocumentObjectGroupPython] C_element087  label="C_element : 045"  # scripted group (container) (typed FeaturePython)
  n = 2
  ref = C_element
FEATURE [App::DocumentObjectGroupPython] F_element014  label="F_element : 4"  # scripted group (container) (typed FeaturePython)
  n = 4
  ref = F_element
FEATURE [App::DocumentObjectGroupPython] G4_TEFLON  # scripted group (container) (typed FeaturePython)
  Dunit = g/cm3
  Dvalue = 2.2
  Group = -> [C_element087,F_element014]
  conduct = 2
  density = 1
  expand = 3
  formula = G4_TEFLON
  name = G4_TEFLON
  specific = 4
FEATURE [App::DocumentObjectGroupPython] C_element088  label="C_element : 046"  # scripted group (container) (typed FeaturePython)
  n = 2
  ref = C_element
FEATURE [App::DocumentObjectGroupPython] F_element015  label="F_element : 006"  # scripted group (container) (typed FeaturePython)
  n = 3
  ref = F_element
FEATURE [App::DocumentObjectGroupPython] Cl_element018  label="Cl_element : 008"  # scripted group (container) (typed FeaturePython)
  n = 1
  ref = Cl_element
FEATURE [App::DocumentObjectGroupPython] G4_POLYTRIFLUOROCHLOROETHYLENE  # scripted group (container) (typed FeaturePython)
  Dunit = g/cm3
  Dvalue = 2.1
  Group = -> [C_element088,F_element015,Cl_element018]
  conduct = 2
  density = 1
  expand = 3
  formula = G4_POLYTRIFLUOROCHLOROETHYLENE
  name = G4_POLYTRIFLUOROCHLOROETHYLENE
  specific = 4
FEATURE [App::DocumentObjectGroupPython] C_element089  label="C_element : 047"  # scripted group (container) (typed FeaturePython)
  n = 4
  ref = C_element
FEATURE [App::DocumentObjectGroupPython] H_element081  label="H_element : 043"  # scripted group (container) (typed FeaturePython)
  n = 6
  ref = H_element
FEATURE [App::DocumentObjectGroupPython] O_element081  label="O_element : 042"  # scripted group (container) (typed FeaturePython)
  n = 2
  ref = O_element
FEATURE [App::DocumentObjectGroupPython] G4_POLYVINYL_ACETATE  # scripted group (container) (typed FeaturePython)
  Dunit = g/cm3
  Dvalue = 1.19
  Group = -> [C_element089,H_element081,O_element081]
  conduct = 2
  density = 1
  expand = 3
  formula = G4_POLYVINYL_ACETATE
  name = G4_POLYVINYL_ACETATE
  specific = 4
FEATURE [App::DocumentObjectGroupPython] C_element090  label="C_element : 048"  # scripted group (container) (typed FeaturePython)
  n = 2
  ref = C_element
FEATURE [App::DocumentObjectGroupPython] H_element082  label="H_element : 044"  # scripted group (container) (typed FeaturePython)
  n = 4
  ref = H_element
FEATURE [App::DocumentObjectGroupPython] O_element082  label="O_element : 043"  # scripted group (container) (typed FeaturePython)
  n = 1
  ref = O_element
FEATURE [App::DocumentObjectGroupPython] G4_POLYVINYL_ALCOHOL  # scripted group (container) (typed FeaturePython)
  Dunit = g/cm3
  Dvalue = 1.3
  Group = -> [C_element090,H_element082,O_element082]
  conduct = 2
  density = 1
  expand = 3
  formula = G4_POLYVINYL_ALCOHOL
  name = G4_POLYVINYL_ALCOHOL
  specific = 4
FEATURE [App::DocumentObjectGroupPython] C_element091  label="C_element : 049"  # scripted group (container) (typed FeaturePython)
  n = 8
  ref = C_element
FEATURE [App::DocumentObjectGroupPython] H_element083  label="H_element : 045"  # scripted group (container) (typed FeaturePython)
  n = 14
  ref = H_element
FEATURE [App::DocumentObjectGroupPython] O_element083  label="O_element : 044"  # scripted group (container) (typed FeaturePython)
  n = 2
  ref = O_element
FEATURE [App::DocumentObjectGroupPython] G4_POLYVINYL_BUTYRAL  # scripted group (container) (typed FeaturePython)
  Dunit = g/cm3
  Dvalue = 1.12
  Group = -> [C_element091,H_element083,O_element083]
  conduct = 2
  density = 1
  expand = 3
  formula = G4_POLYVINYL_BUTYRAL
  name = G4_POLYVINYL_BUTYRAL
  specific = 4
FEATURE [App::DocumentObjectGroupPython] C_element092  label="C_element : 050"  # scripted group (container) (typed FeaturePython)
  n = 2
  ref = C_element
FEATURE [App::DocumentObjectGroupPython] H_element084  label="H_element : 046"  # scripted group (container) (typed FeaturePython)
  n = 3
  ref = H_element
FEATURE [App::DocumentObjectGroupPython] Cl_element019  label="Cl_element : 009"  # scripted group (container) (typed FeaturePython)
  n = 1
  ref = Cl_element
FEATURE [App::DocumentObjectGroupPython] G4_POLYVINYL_CHLORIDE  # scripted group (container) (typed FeaturePython)
  Dunit = g/cm3
  Dvalue = 1.3
  Group = -> [C_element092,H_element084,Cl_element019]
  conduct = 2
  density = 1
  expand = 3
  formula = G4_POLYVINYL_CHLORIDE
  name = G4_POLYVINYL_CHLORIDE
  specific = 4
FEATURE [App::DocumentObjectGroupPython] C_element093  label="C_element : 051"  # scripted group (container) (typed FeaturePython)
  n = 2
  ref = C_element
FEATURE [App::DocumentObjectGroupPython] H_element085  label="H_element : 047"  # scripted group (container) (typed FeaturePython)
  n = 2
  ref = H_element
FEATURE [App::DocumentObjectGroupPython] Cl_element020  label="Cl_element : 010"  # scripted group (container) (typed FeaturePython)
  n = 2
  ref = Cl_element
FEATURE [App::DocumentObjectGroupPython] G4_POLYVINYLIDENE_CHLORIDE  # scripted group (container) (typed FeaturePython)
  Dunit = g/cm3
  Dvalue = 1.7
  Group = -> [C_element093,H_element085,Cl_element020]
  conduct = 2
  density = 1
  expand = 3
  formula = G4_POLYVINYLIDENE_CHLORIDE
  name = G4_POLYVINYLIDENE_CHLORIDE
  specific = 4
FEATURE [App::DocumentObjectGroupPython] C_element094  label="C_element : 052"  # scripted group (container) (typed FeaturePython)
  n = 2
  ref = C_element
FEATURE [App::DocumentObjectGroupPython] H_element086  label="H_element : 048"  # scripted group (container) (typed FeaturePython)
  n = 2
  ref = H_element
FEATURE [App::DocumentObjectGroupPython] F_element016  label="F_element : 007"  # scripted group (container) (typed FeaturePython)
  n = 2
  ref = F_element
FEATURE [App::DocumentObjectGroupPython] G4_POLYVINYLIDENE_FLUORIDE  # scripted group (container) (typed FeaturePython)
  Dunit = g/cm3
  Dvalue = 1.76
  Group = -> [C_element094,H_element086,F_element016]
  conduct = 2
  density = 1
  expand = 3
  formula = G4_POLYVINYLIDENE_FLUORIDE
  name = G4_POLYVINYLIDENE_FLUORIDE
  specific = 4
FEATURE [App::DocumentObjectGroupPython] C_element095  label="C_element : 053"  # scripted group (container) (typed FeaturePython)
  n = 6
  ref = C_element
FEATURE [App::DocumentObjectGroupPython] H_element087  label="H_element : 9"  # scripted group (container) (typed FeaturePython)
  n = 9
  ref = H_element
FEATURE [App::DocumentObjectGroupPython] N_element037  label="N_element : 016"  # scripted group (container) (typed FeaturePython)
  n = 1
  ref = N_element
FEATURE [App::DocumentObjectGroupPython] O_element084  label="O_element : 045"  # scripted group (container) (typed FeaturePython)
  n = 1
  ref = O_element
FEATURE [App::DocumentObjectGroupPython] G4_POLYVINYL_PYRROLIDONE  # scripted group (container) (typed FeaturePython)
  Dunit = g/cm3
  Dvalue = 1.25
  Group = -> [C_element095,H_element087,N_element037,O_element084]
  conduct = 2
  density = 1
  expand = 3
  formula = G4_POLYVINYL_PYRROLIDONE
  name = G4_POLYVINYL_PYRROLIDONE
  specific = 4
FEATURE [App::DocumentObjectGroupPython] K_element008  label="K_element : 1"  # scripted group (container) (typed FeaturePython)
  n = 1
  ref = K_element
FEATURE [App::DocumentObjectGroupPython] I_element006  label="I_element : 003"  # scripted group (container) (typed FeaturePython)
  n = 1
  ref = I_element
FEATURE [App::DocumentObjectGroupPython] G4_POTASSIUM_IODIDE  # scripted group (container) (typed FeaturePython)
  Dunit = g/cm3
  Dvalue = 3.13
  Group = -> [K_element008,I_element006]
  conduct = 2
  density = 1
  expand = 3
  formula = G4_POTASSIUM_IODIDE
  name = G4_POTASSIUM_IODIDE
  specific = 4
FEATURE [App::DocumentObjectGroupPython] K_element009  label="K_element : 2"  # scripted group (container) (typed FeaturePython)
  n = 2
  ref = K_element
FEATURE [App::DocumentObjectGroupPython] O_element085  label="O_element : 046"  # scripted group (container) (typed FeaturePython)
  n = 1
  ref = O_element
FEATURE [App::DocumentObjectGroupPython] G4_POTASSIUM_OXIDE  # scripted group (container) (typed FeaturePython)
  Dunit = g/cm3
  Dvalue = 2.32
  Group = -> [K_element009,O_element085]
  conduct = 2
  density = 1
  expand = 3
  formula = G4_POTASSIUM_OXIDE
  name = G4_POTASSIUM_OXIDE
  specific = 4
FEATURE [App::DocumentObjectGroupPython] C_element096  label="C_element : 054"  # scripted group (container) (typed FeaturePython)
  n = 3
  ref = C_element
FEATURE [App::DocumentObjectGroupPython] H_element088  label="H_element : 049"  # scripted group (container) (typed FeaturePython)
  n = 8
  ref = H_element
FEATURE [App::DocumentObjectGroupPython] G4_PROPANE  # scripted group (container) (typed FeaturePython)
  Dunit = g/cm3
  Dvalue = 0.00187939
  Group = -> [C_element096,H_element088]
  conduct = 2
  density = 1
  expand = 3
  formula = G4_PROPANE
  name = G4_PROPANE
  specific = 4
FEATURE [App::DocumentObjectGroupPython] C_element097  label="C_element : 055"  # scripted group (container) (typed FeaturePython)
  n = 3
  ref = C_element
FEATURE [App::DocumentObjectGroupPython] H_element089  label="H_element : 050"  # scripted group (container) (typed FeaturePython)
  n = 8
  ref = H_element
FEATURE [App::DocumentObjectGroupPython] G4_lPROPANE  # scripted group (container) (typed FeaturePython)
  Dunit = g/cm3
  Dvalue = 0.43
  Group = -> [C_element097,H_element089]
  conduct = 2
  density = 1
  expand = 3
  formula = G4_lPROPANE
  name = G4_lPROPANE
  specific = 4
FEATURE [App::DocumentObjectGroupPython] C_element098  label="C_element : 056"  # scripted group (container) (typed FeaturePython)
  n = 3
  ref = C_element
FEATURE [App::DocumentObjectGroupPython] H_element090  label="H_element : 051"  # scripted group (container) (typed FeaturePython)
  n = 8
  ref = H_element
FEATURE [App::DocumentObjectGroupPython] O_element086  label="O_element : 047"  # scripted group (container) (typed FeaturePython)
  n = 1
  ref = O_element
FEATURE [App::DocumentObjectGroupPython] G4_N_PROPYL_ALCOHOL  label="G4_N-PROPYL_ALCOHOL"  # scripted group (container) (typed FeaturePython)
  Dunit = g/cm3
  Dvalue = 0.8035
  Group = -> [C_element098,H_element090,O_element086]
  conduct = 2
  density = 1
  expand = 3
  formula = G4_N-PROPYL_ALCOHOL
  name = G4_N-PROPYL_ALCOHOL
  specific = 4
FEATURE [App::DocumentObjectGroupPython] C_element099  label="C_element : 057"  # scripted group (container) (typed FeaturePython)
  n = 5
  ref = C_element
FEATURE [App::DocumentObjectGroupPython] H_element091  label="H_element : 052"  # scripted group (container) (typed FeaturePython)
  n = 5
  ref = H_element
FEATURE [App::DocumentObjectGroupPython] N_element038  label="N_element : 017"  # scripted group (container) (typed FeaturePython)
  n = 1
  ref = N_element
FEATURE [App::DocumentObjectGroupPython] G4_PYRIDINE  # scripted group (container) (typed FeaturePython)
  Dunit = g/cm3
  Dvalue = 0.9819
  Group = -> [C_element099,H_element091,N_element038]
  conduct = 2
  density = 1
  expand = 3
  formula = G4_PYRIDINE
  name = G4_PYRIDINE
  specific = 4
FEATURE [App::DocumentObjectGroupPython] H_element092  label="H_element : 0.144"  # scripted group (container) (typed FeaturePython)
  n = 0.143711
FEATURE [App::DocumentObjectGroupPython] C_element100  label="C_element : 0.856"  # scripted group (container) (typed FeaturePython)
  n = 0.856289
FEATURE [App::DocumentObjectGroupPython] G4_RUBBER_BUTYL  # scripted group (container) (typed FeaturePython)
  Dunit = g/cm3
  Dvalue = 0.92
  Group = -> [H_element092,C_element100]
  conduct = 2
  density = 1
  expand = 3
  formula = G4_RUBBER_BUTYL
  name = G4_RUBBER_BUTYL
  specific = 4
FEATURE [App::DocumentObjectGroupPython] H_element093  label="H_element : 0.118"  # scripted group (container) (typed FeaturePython)
  n = 0.118371
FEATURE [App::DocumentObjectGroupPython] C_element101  label="C_element : 0.882"  # scripted group (container) (typed FeaturePython)
  n = 0.881629
FEATURE [App::DocumentObjectGroupPython] G4_RUBBER_NATURAL  # scripted group (container) (typed FeaturePython)
  Dunit = g/cm3
  Dvalue = 0.92
  Group = -> [H_element093,C_element101]
  conduct = 2
  density = 1
  expand = 3
  formula = G4_RUBBER_NATURAL
  name = G4_RUBBER_NATURAL
  specific = 4
FEATURE [App::DocumentObjectGroupPython] H_element094  label="H_element : 0.145"  # scripted group (container) (typed FeaturePython)
  n = 0.05692
FEATURE [App::DocumentObjectGroupPython] C_element102  label="C_element : 0.543"  # scripted group (container) (typed FeaturePython)
  n = 0.542646
FEATURE [App::DocumentObjectGroupPython] Cl_element021  label="Cl_element : 0.400"  # scripted group (container) (typed FeaturePython)
  n = 0.400434
FEATURE [App::DocumentObjectGroupPython] G4_RUBBER_NEOPRENE  # scripted group (container) (typed FeaturePython)
  Dunit = g/cm3
  Dvalue = 1.23
  Group = -> [H_element094,C_element102,Cl_element021]
  conduct = 2
  density = 1
  expand = 3
  formula = G4_RUBBER_NEOPRENE
  name = G4_RUBBER_NEOPRENE
  specific = 4
FEATURE [App::DocumentObjectGroupPython] Si_element006  label="Si_element : 1"  # scripted group (container) (typed FeaturePython)
  n = 1
  ref = Si_element
FEATURE [App::DocumentObjectGroupPython] O_element087  label="O_element : 048"  # scripted group (container) (typed FeaturePython)
  n = 2
  ref = O_element
FEATURE [App::DocumentObjectGroupPython] G4_SILICON_DIOXIDE  # scripted group (container) (typed FeaturePython)
  Dunit = g/cm3
  Dvalue = 2.32
  Group = -> [Si_element006,O_element087]
  conduct = 2
  density = 1
  expand = 3
  formula = G4_SILICON_DIOXIDE
  name = G4_SILICON_DIOXIDE
  specific = 4
FEATURE [App::DocumentObjectGroupPython] Ag_element002  label="Ag_element : 1"  # scripted group (container) (typed FeaturePython)
  n = 1
  ref = Ag_element
FEATURE [App::DocumentObjectGroupPython] Br_element005  label="Br_element : 003"  # scripted group (container) (typed FeaturePython)
  n = 1
  ref = Br_element
FEATURE [App::DocumentObjectGroupPython] G4_SILVER_BROMIDE  # scripted group (container) (typed FeaturePython)
  Dunit = g/cm3
  Dvalue = 6.473
  Group = -> [Ag_element002,Br_element005]
  conduct = 2
  density = 1
  expand = 3
  formula = G4_SILVER_BROMIDE
  name = G4_SILVER_BROMIDE
  specific = 4
FEATURE [App::DocumentObjectGroupPython] Ag_element003  label="Ag_element : 002"  # scripted group (container) (typed FeaturePython)
  n = 1
  ref = Ag_element
FEATURE [App::DocumentObjectGroupPython] Cl_element022  label="Cl_element : 011"  # scripted group (container) (typed FeaturePython)
  n = 1
  ref = Cl_element
FEATURE [App::DocumentObjectGroupPython] G4_SILVER_CHLORIDE  # scripted group (container) (typed FeaturePython)
  Dunit = g/cm3
  Dvalue = 5.56
  Group = -> [Ag_element003,Cl_element022]
  conduct = 2
  density = 1
  expand = 3
  formula = G4_SILVER_CHLORIDE
  name = G4_SILVER_CHLORIDE
  specific = 4
FEATURE [App::DocumentObjectGroupPython] Br_element006  label="Br_element : 0.423"  # scripted group (container) (typed FeaturePython)
  n = 0.422895
FEATURE [App::DocumentObjectGroupPython] Ag_element004  label="Ag_element : 0.574"  # scripted group (container) (typed FeaturePython)
  n = 0.573748
FEATURE [App::DocumentObjectGroupPython] I_element007  label="I_element : 0.649"  # scripted group (container) (typed FeaturePython)
  n = 0.003357
FEATURE [App::DocumentObjectGroupPython] G4_SILVER_HALIDES  # scripted group (container) (typed FeaturePython)
  Dunit = g/cm3
  Dvalue = 6.47
  Group = -> [Br_element006,Ag_element004,I_element007]
  conduct = 2
  density = 1
  expand = 3
  formula = G4_SILVER_HALIDES
  name = G4_SILVER_HALIDES
  specific = 4
FEATURE [App::DocumentObjectGroupPython] Ag_element005  label="Ag_element : 003"  # scripted group (container) (typed FeaturePython)
  n = 1
  ref = Ag_element
FEATURE [App::DocumentObjectGroupPython] I_element008  label="I_element : 004"  # scripted group (container) (typed FeaturePython)
  n = 1
  ref = I_element
FEATURE [App::DocumentObjectGroupPython] G4_SILVER_IODIDE  # scripted group (container) (typed FeaturePython)
  Dunit = g/cm3
  Dvalue = 6.01
  Group = -> [Ag_element005,I_element008]
  conduct = 2
  density = 1
  expand = 3
  formula = G4_SILVER_IODIDE
  name = G4_SILVER_IODIDE
  specific = 4
FEATURE [App::DocumentObjectGroupPython] H_element095  label="H_element : 0.100"  # scripted group (container) (typed FeaturePython)
  n = 0.1
FEATURE [App::DocumentObjectGroupPython] C_element103  label="C_element : 0.204"  # scripted group (container) (typed FeaturePython)
  n = 0.204
FEATURE [App::DocumentObjectGroupPython] N_element039  label="N_element : 0.759"  # scripted group (container) (typed FeaturePython)
  n = 0.042
FEATURE [App::DocumentObjectGroupPython] O_element088  label="O_element : 0.645"  # scripted group (container) (typed FeaturePython)
  n = 0.645
FEATURE [App::DocumentObjectGroupPython] Na_element013  label="Na_element : 0.100"  # scripted group (container) (typed FeaturePython)
  n = 0.002
FEATURE [App::DocumentObjectGroupPython] P_element009  label="P_element : 0.107"  # scripted group (container) (typed FeaturePython)
  n = 0.001
FEATURE [App::DocumentObjectGroupPython] S_element020  label="S_element : 0.021"  # scripted group (container) (typed FeaturePython)
  n = 0.002
FEATURE [App::DocumentObjectGroupPython] Cl_element023  label="Cl_element : 0.590"  # scripted group (container) (typed FeaturePython)
  n = 0.003
FEATURE [App::DocumentObjectGroupPython] K_element010  label="K_element : 0.001"  # scripted group (container) (typed FeaturePython)
  n = 0.001
FEATURE [App::DocumentObjectGroupPython] G4_SKIN_ICRP  # scripted group (container) (typed FeaturePython)
  Dunit = g/cm3
  Dvalue = 1.09
  Group = -> [H_element095,C_element103,N_element039,O_element088,Na_element013,P_element009,S_element020,Cl_element023,K_element010]
  conduct = 2
  density = 1
  expand = 3
  formula = G4_SKIN_ICRP
  name = G4_SKIN_ICRP
  specific = 4
FEATURE [App::DocumentObjectGroupPython] Na_element014  label="Na_element : 2"  # scripted group (container) (typed FeaturePython)
  n = 2
  ref = Na_element
FEATURE [App::DocumentObjectGroupPython] C_element104  label="C_element : 058"  # scripted group (container) (typed FeaturePython)
  n = 1
  ref = C_element
FEATURE [App::DocumentObjectGroupPython] O_element089  label="O_element : 049"  # scripted group (container) (typed FeaturePython)
  n = 3
  ref = O_element
FEATURE [App::DocumentObjectGroupPython] G4_SODIUM_CARBONATE  # scripted group (container) (typed FeaturePython)
  Dunit = g/cm3
  Dvalue = 2.532
  Group = -> [Na_element014,C_element104,O_element089]
  conduct = 2
  density = 1
  expand = 3
  formula = G4_SODIUM_CARBONATE
  name = G4_SODIUM_CARBONATE
  specific = 4
FEATURE [App::DocumentObjectGroupPython] Na_element015  label="Na_element : 1"  # scripted group (container) (typed FeaturePython)
  n = 1
  ref = Na_element
FEATURE [App::DocumentObjectGroupPython] I_element009  label="I_element : 005"  # scripted group (container) (typed FeaturePython)
  n = 1
  ref = I_element
FEATURE [App::DocumentObjectGroupPython] G4_SODIUM_IODIDE  # scripted group (container) (typed FeaturePython)
  Dunit = g/cm3
  Dvalue = 3.667
  Group = -> [Na_element015,I_element009]
  conduct = 2
  density = 1
  expand = 3
  formula = G4_SODIUM_IODIDE
  name = G4_SODIUM_IODIDE
  specific = 4
FEATURE [App::DocumentObjectGroupPython] Na_element016  label="Na_element : 003"  # scripted group (container) (typed FeaturePython)
  n = 2
  ref = Na_element
FEATURE [App::DocumentObjectGroupPython] O_element090  label="O_element : 050"  # scripted group (container) (typed FeaturePython)
  n = 1
  ref = O_element
FEATURE [App::DocumentObjectGroupPython] G4_SODIUM_MONOXIDE  # scripted group (container) (typed FeaturePython)
  Dunit = g/cm3
  Dvalue = 2.27
  Group = -> [Na_element016,O_element090]
  conduct = 2
  density = 1
  expand = 3
  formula = G4_SODIUM_MONOXIDE
  name = G4_SODIUM_MONOXIDE
  specific = 4
FEATURE [App::DocumentObjectGroupPython] Na_element017  label="Na_element : 004"  # scripted group (container) (typed FeaturePython)
  n = 1
  ref = Na_element
FEATURE [App::DocumentObjectGroupPython] N_element040  label="N_element : 018"  # scripted group (container) (typed FeaturePython)
  n = 1
  ref = N_element
FEATURE [App::DocumentObjectGroupPython] O_element091  label="O_element : 051"  # scripted group (container) (typed FeaturePython)
  n = 3
  ref = O_element
FEATURE [App::DocumentObjectGroupPython] G4_SODIUM_NITRATE  # scripted group (container) (typed FeaturePython)
  Dunit = g/cm3
  Dvalue = 2.261
  Group = -> [Na_element017,N_element040,O_element091]
  conduct = 2
  density = 1
  expand = 3
  formula = G4_SODIUM_NITRATE
  name = G4_SODIUM_NITRATE
  specific = 4
FEATURE [App::DocumentObjectGroupPython] C_element105  label="C_element : 059"  # scripted group (container) (typed FeaturePython)
  n = 14
  ref = C_element
FEATURE [App::DocumentObjectGroupPython] H_element096  label="H_element : 053"  # scripted group (container) (typed FeaturePython)
  n = 12
  ref = H_element
FEATURE [App::DocumentObjectGroupPython] G4_STILBENE  # scripted group (container) (typed FeaturePython)
  Dunit = g/cm3
  Dvalue = 0.9707
  Group = -> [C_element105,H_element096]
  conduct = 2
  density = 1
  expand = 3
  formula = G4_STILBENE
  name = G4_STILBENE
  specific = 4
FEATURE [App::DocumentObjectGroupPython] C_element106  label="C_element : 12"  # scripted group (container) (typed FeaturePython)
  n = 12
  ref = C_element
FEATURE [App::DocumentObjectGroupPython] H_element097  label="H_element : 22"  # scripted group (container) (typed FeaturePython)
  n = 22
  ref = H_element
FEATURE [App::DocumentObjectGroupPython] O_element092  label="O_element : 11"  # scripted group (container) (typed FeaturePython)
  n = 11
  ref = O_element
FEATURE [App::DocumentObjectGroupPython] G4_SUCROSE  # scripted group (container) (typed FeaturePython)
  Dunit = g/cm3
  Dvalue = 1.5805
  Group = -> [C_element106,H_element097,O_element092]
  conduct = 2
  density = 1
  expand = 3
  formula = G4_SUCROSE
  name = G4_SUCROSE
  specific = 4
FEATURE [App::DocumentObjectGroupPython] C_element107  label="C_element : 18"  # scripted group (container) (typed FeaturePython)
  n = 18
  ref = C_element
FEATURE [App::DocumentObjectGroupPython] H_element098  label="H_element : 054"  # scripted group (container) (typed FeaturePython)
  n = 14
  ref = H_element
FEATURE [App::DocumentObjectGroupPython] G4_TERPHENYL  # scripted group (container) (typed FeaturePython)
  Dunit = g/cm3
  Dvalue = 1.24
  Group = -> [C_element107,H_element098]
  conduct = 2
  density = 1
  expand = 3
  formula = G4_TERPHENYL
  name = G4_TERPHENYL
  specific = 4
FEATURE [App::DocumentObjectGroupPython] H_element099  label="H_element : 0.146"  # scripted group (container) (typed FeaturePython)
  n = 0.106
FEATURE [App::DocumentObjectGroupPython] C_element108  label="C_element : 0.883"  # scripted group (container) (typed FeaturePython)
  n = 0.099
FEATURE [App::DocumentObjectGroupPython] N_element041  label="N_element : 0.020"  # scripted group (container) (typed FeaturePython)
  n = 0.02
FEATURE [App::DocumentObjectGroupPython] O_element093  label="O_element : 0.766"  # scripted group (container) (typed FeaturePython)
  n = 0.766
FEATURE [App::DocumentObjectGroupPython] Na_element018  label="Na_element : 0.101"  # scripted group (container) (typed FeaturePython)
  n = 0.002
FEATURE [App::DocumentObjectGroupPython] P_element010  label="P_element : 0.108"  # scripted group (container) (typed FeaturePython)
  n = 0.001
FEATURE [App::DocumentObjectGroupPython] S_element021  label="S_element : 0.022"  # scripted group (container) (typed FeaturePython)
  n = 0.002
FEATURE [App::DocumentObjectGroupPython] Cl_element024  label="Cl_element : 0.002"  # scripted group (container) (typed FeaturePython)
  n = 0.002
FEATURE [App::DocumentObjectGroupPython] K_element011  label="K_element : 0.017"  # scripted group (container) (typed FeaturePython)
  n = 0.002
FEATURE [App::DocumentObjectGroupPython] G4_TESTIS_ICRP  # scripted group (container) (typed FeaturePython)
  Dunit = g/cm3
  Dvalue = 1.04
  Group = -> [H_element099,C_element108,N_element041,O_element093,Na_element018,P_element010,S_element021,Cl_element024,K_element011]
  conduct = 2
  density = 1
  expand = 3
  formula = G4_TESTIS_ICRP
  name = G4_TESTIS_ICRP
  specific = 4
FEATURE [App::DocumentObjectGroupPython] C_element109  label="C_element : 060"  # scripted group (container) (typed FeaturePython)
  n = 2
  ref = C_element
FEATURE [App::DocumentObjectGroupPython] Cl_element025  label="Cl_element : 012"  # scripted group (container) (typed FeaturePython)
  n = 4
  ref = Cl_element
FEATURE [App::DocumentObjectGroupPython] G4_TETRACHLOROETHYLENE  # scripted group (container) (typed FeaturePython)
  Dunit = g/cm3
  Dvalue = 1.625
  Group = -> [C_element109,Cl_element025]
  conduct = 2
  density = 1
  expand = 3
  formula = G4_TETRACHLOROETHYLENE
  name = G4_TETRACHLOROETHYLENE
  specific = 4
FEATURE [App::DocumentObjectGroupPython] Tl_element001  label="Tl_element : 1"  # scripted group (container) (typed FeaturePython)
  n = 1
  ref = Tl_element
FEATURE [App::DocumentObjectGroupPython] Cl_element026  label="Cl_element : 013"  # scripted group (container) (typed FeaturePython)
  n = 1
  ref = Cl_element
FEATURE [App::DocumentObjectGroupPython] G4_THALLIUM_CHLORIDE  # scripted group (container) (typed FeaturePython)
  Dunit = g/cm3
  Dvalue = 7.004
  Group = -> [Tl_element001,Cl_element026]
  conduct = 2
  density = 1
  expand = 3
  formula = G4_THALLIUM_CHLORIDE
  name = G4_THALLIUM_CHLORIDE
  specific = 4
FEATURE [App::DocumentObjectGroupPython] H_element100  label="H_element : 0.147"  # scripted group (container) (typed FeaturePython)
  n = 0.105
FEATURE [App::DocumentObjectGroupPython] C_element110  label="C_element : 0.256"  # scripted group (container) (typed FeaturePython)
  n = 0.256
FEATURE [App::DocumentObjectGroupPython] N_element042  label="N_element : 0.760"  # scripted group (container) (typed FeaturePython)
  n = 0.027
FEATURE [App::DocumentObjectGroupPython] O_element094  label="O_element : 0.602"  # scripted group (container) (typed FeaturePython)
  n = 0.602
FEATURE [App::DocumentObjectGroupPython] Na_element019  label="Na_element : 0.102"  # scripted group (container) (typed FeaturePython)
  n = 0.001
FEATURE [App::DocumentObjectGroupPython] P_element011  label="P_element : 0.109"  # scripted group (container) (typed FeaturePython)
  n = 0.002
FEATURE [App::DocumentObjectGroupPython] S_element022  label="S_element : 0.023"  # scripted group (container) (typed FeaturePython)
  n = 0.003
FEATURE [App::DocumentObjectGroupPython] Cl_element027  label="Cl_element : 0.591"  # scripted group (container) (typed FeaturePython)
  n = 0.002
FEATURE [App::DocumentObjectGroupPython] K_element012  label="K_element : 0.018"  # scripted group (container) (typed FeaturePython)
  n = 0.002
FEATURE [App::DocumentObjectGroupPython] G4_TISSUE_SOFT_ICRP  # scripted group (container) (typed FeaturePython)
  Dunit = g/cm3
  Dvalue = 1.03
  Group = -> [H_element100,C_element110,N_element042,O_element094,Na_element019,P_element011,S_element022,Cl_element027,K_element012]
  conduct = 2
  density = 1
  expand = 3
  formula = G4_TISSUE_SOFT_ICRP
  name = G4_TISSUE_SOFT_ICRP
  specific = 4
FEATURE [App::DocumentObjectGroupPython] H_element101  label="H_element : 0.148"  # scripted group (container) (typed FeaturePython)
  n = 0.101
FEATURE [App::DocumentObjectGroupPython] C_element111  label="C_element : 0.111"  # scripted group (container) (typed FeaturePython)
  n = 0.111
FEATURE [App::DocumentObjectGroupPython] N_element043  label="N_element : 0.026"  # scripted group (container) (typed FeaturePython)
  n = 0.026
FEATURE [App::DocumentObjectGroupPython] O_element095  label="O_element : 0.762"  # scripted group (container) (typed FeaturePython)
  n = 0.762
FEATURE [App::DocumentObjectGroupPython] G4_TISSUE_SOFT_ICRU_4  label="G4_TISSUE_SOFT_ICRU-4"  # scripted group (container) (typed FeaturePython)
  Dunit = g/cm3
  Dvalue = 1
  Group = -> [H_element101,C_element111,N_element043,O_element095]
  conduct = 2
  density = 1
  expand = 3
  formula = G4_TISSUE_SOFT_ICRU-4
  name = G4_TISSUE_SOFT_ICRU-4
  specific = 4
FEATURE [App::DocumentObjectGroupPython] H_element102  label="H_element : 0.149"  # scripted group (container) (typed FeaturePython)
  n = 0.101869
FEATURE [App::DocumentObjectGroupPython] C_element112  label="C_element : 0.456"  # scripted group (container) (typed FeaturePython)
  n = 0.456179
FEATURE [App::DocumentObjectGroupPython] N_element044  label="N_element : 0.761"  # scripted group (container) (typed FeaturePython)
  n = 0.035172
FEATURE [App::DocumentObjectGroupPython] O_element096  label="O_element : 0.407"  # scripted group (container) (typed FeaturePython)
  n = 0.40678
FEATURE [App::DocumentObjectGroupPython] G4_TISSUE_METHANE  label="G4_TISSUE-METHANE"  # scripted group (container) (typed FeaturePython)
  Dunit = g/cm3
  Dvalue = 0.00106409
  Group = -> [H_element102,C_element112,N_element044,O_element096]
  conduct = 2
  density = 1
  expand = 3
  formula = G4_TISSUE-METHANE
  name = G4_TISSUE-METHANE
  specific = 4
FEATURE [App::DocumentObjectGroupPython] H_element103  label="H_element : 0.103"  # scripted group (container) (typed FeaturePython)
  n = 0.102672
FEATURE [App::DocumentObjectGroupPython] C_element113  label="C_element : 0.569"  # scripted group (container) (typed FeaturePython)
  n = 0.56894
FEATURE [App::DocumentObjectGroupPython] N_element045  label="N_element : 0.762"  # scripted group (container) (typed FeaturePython)
  n = 0.035022
FEATURE [App::DocumentObjectGroupPython] O_element097  label="O_element : 0.293"  # scripted group (container) (typed FeaturePython)
  n = 0.293366
FEATURE [App::DocumentObjectGroupPython] G4_TISSUE_PROPANE  label="G4_TISSUE-PROPANE"  # scripted group (container) (typed FeaturePython)
  Dunit = g/cm3
  Dvalue = 0.00182628
  Group = -> [H_element103,C_element113,N_element045,O_element097]
  conduct = 2
  density = 1
  expand = 3
  formula = G4_TISSUE-PROPANE
  name = G4_TISSUE-PROPANE
  specific = 4
FEATURE [App::DocumentObjectGroupPython] Ti_element003  label="Ti_element : 1"  # scripted group (container) (typed FeaturePython)
  n = 1
  ref = Ti_element
FEATURE [App::DocumentObjectGroupPython] O_element098  label="O_element : 052"  # scripted group (container) (typed FeaturePython)
  n = 2
  ref = O_element
FEATURE [App::DocumentObjectGroupPython] G4_TITANIUM_DIOXIDE  # scripted group (container) (typed FeaturePython)
  Dunit = g/cm3
  Dvalue = 4.26
  Group = -> [Ti_element003,O_element098]
  conduct = 2
  density = 1
  expand = 3
  formula = G4_TITANIUM_DIOXIDE
  name = G4_TITANIUM_DIOXIDE
  specific = 4
FEATURE [App::DocumentObjectGroupPython] C_element114  label="C_element : 061"  # scripted group (container) (typed FeaturePython)
  n = 7
  ref = C_element
FEATURE [App::DocumentObjectGroupPython] H_element104  label="H_element : 055"  # scripted group (container) (typed FeaturePython)
  n = 8
  ref = H_element
FEATURE [App::DocumentObjectGroupPython] G4_TOLUENE  # scripted group (container) (typed FeaturePython)
  Dunit = g/cm3
  Dvalue = 0.8669
  Group = -> [C_element114,H_element104]
  conduct = 2
  density = 1
  expand = 3
  formula = G4_TOLUENE
  name = G4_TOLUENE
  specific = 4
FEATURE [App::DocumentObjectGroupPython] C_element115  label="C_element : 062"  # scripted group (container) (typed FeaturePython)
  n = 2
  ref = C_element
FEATURE [App::DocumentObjectGroupPython] H_element105  label="H_element : 056"  # scripted group (container) (typed FeaturePython)
  n = 1
  ref = H_element
FEATURE [App::DocumentObjectGroupPython] Cl_element028  label="Cl_element : 014"  # scripted group (container) (typed FeaturePython)
  n = 3
  ref = Cl_element
FEATURE [App::DocumentObjectGroupPython] G4_TRICHLOROETHYLENE  # scripted group (container) (typed FeaturePython)
  Dunit = g/cm3
  Dvalue = 1.46
  Group = -> [C_element115,H_element105,Cl_element028]
  conduct = 2
  density = 1
  expand = 3
  formula = G4_TRICHLOROETHYLENE
  name = G4_TRICHLOROETHYLENE
  specific = 4
FEATURE [App::DocumentObjectGroupPython] C_element116  label="C_element : 063"  # scripted group (container) (typed FeaturePython)
  n = 6
  ref = C_element
FEATURE [App::DocumentObjectGroupPython] H_element106  label="H_element : 15"  # scripted group (container) (typed FeaturePython)
  n = 15
  ref = H_element
FEATURE [App::DocumentObjectGroupPython] O_element099  label="O_element : 053"  # scripted group (container) (typed FeaturePython)
  n = 4
  ref = O_element
FEATURE [App::DocumentObjectGroupPython] P_element012  label="P_element : 1"  # scripted group (container) (typed FeaturePython)
  n = 1
  ref = P_element
FEATURE [App::DocumentObjectGroupPython] G4_TRIETHYL_PHOSPHATE  # scripted group (container) (typed FeaturePython)
  Dunit = g/cm3
  Dvalue = 1.07
  Group = -> [C_element116,H_element106,O_element099,P_element012]
  conduct = 2
  density = 1
  expand = 3
  formula = G4_TRIETHYL_PHOSPHATE
  name = G4_TRIETHYL_PHOSPHATE
  specific = 4
FEATURE [App::DocumentObjectGroupPython] W_element003  label="W_element : 003"  # scripted group (container) (typed FeaturePython)
  n = 1
  ref = W_element
FEATURE [App::DocumentObjectGroupPython] F_element017  label="F_element : 6"  # scripted group (container) (typed FeaturePython)
  n = 6
  ref = F_element
FEATURE [App::DocumentObjectGroupPython] G4_TUNGSTEN_HEXAFLUORIDE  # scripted group (container) (typed FeaturePython)
  Dunit = g/cm3
  Dvalue = 2.4
  Group = -> [W_element003,F_element017]
  conduct = 2
  density = 1
  expand = 3
  formula = G4_TUNGSTEN_HEXAFLUORIDE
  name = G4_TUNGSTEN_HEXAFLUORIDE
  specific = 4
FEATURE [App::DocumentObjectGroupPython] U_element001  label="U_element : 1"  # scripted group (container) (typed FeaturePython)
  n = 1
  ref = U_element
FEATURE [App::DocumentObjectGroupPython] C_element117  label="C_element : 064"  # scripted group (container) (typed FeaturePython)
  n = 2
  ref = C_element
FEATURE [App::DocumentObjectGroupPython] G4_URANIUM_DICARBIDE  # scripted group (container) (typed FeaturePython)
  Dunit = g/cm3
  Dvalue = 11.28
  Group = -> [U_element001,C_element117]
  conduct = 2
  density = 1
  expand = 3
  formula = G4_URANIUM_DICARBIDE
  name = G4_URANIUM_DICARBIDE
  specific = 4
FEATURE [App::DocumentObjectGroupPython] U_element002  label="U_element : 002"  # scripted group (container) (typed FeaturePython)
  n = 1
  ref = U_element
FEATURE [App::DocumentObjectGroupPython] C_element118  label="C_element : 065"  # scripted group (container) (typed FeaturePython)
  n = 1
  ref = C_element
FEATURE [App::DocumentObjectGroupPython] G4_URANIUM_MONOCARBIDE  # scripted group (container) (typed FeaturePython)
  Dunit = g/cm3
  Dvalue = 13.63
  Group = -> [U_element002,C_element118]
  conduct = 2
  density = 1
  expand = 3
  formula = G4_URANIUM_MONOCARBIDE
  name = G4_URANIUM_MONOCARBIDE
  specific = 4
FEATURE [App::DocumentObjectGroupPython] U_element003  label="U_element : 003"  # scripted group (container) (typed FeaturePython)
  n = 1
  ref = U_element
FEATURE [App::DocumentObjectGroupPython] O_element100  label="O_element : 054"  # scripted group (container) (typed FeaturePython)
  n = 2
  ref = O_element
FEATURE [App::DocumentObjectGroupPython] G4_URANIUM_OXIDE  # scripted group (container) (typed FeaturePython)
  Dunit = g/cm3
  Dvalue = 10.96
  Group = -> [U_element003,O_element100]
  conduct = 2
  density = 1
  expand = 3
  formula = G4_URANIUM_OXIDE
  name = G4_URANIUM_OXIDE
  specific = 4
FEATURE [App::DocumentObjectGroupPython] C_element119  label="C_element : 066"  # scripted group (container) (typed FeaturePython)
  n = 1
  ref = C_element
FEATURE [App::DocumentObjectGroupPython] H_element107  label="H_element : 057"  # scripted group (container) (typed FeaturePython)
  n = 4
  ref = H_element
FEATURE [App::DocumentObjectGroupPython] N_element046  label="N_element : 019"  # scripted group (container) (typed FeaturePython)
  n = 2
  ref = N_element
FEATURE [App::DocumentObjectGroupPython] O_element101  label="O_element : 055"  # scripted group (container) (typed FeaturePython)
  n = 1
  ref = O_element
FEATURE [App::DocumentObjectGroupPython] G4_UREA  # scripted group (container) (typed FeaturePython)
  Dunit = g/cm3
  Dvalue = 1.323
  Group = -> [C_element119,H_element107,N_element046,O_element101]
  conduct = 2
  density = 1
  expand = 3
  formula = G4_UREA
  name = G4_UREA
  specific = 4
FEATURE [App::DocumentObjectGroupPython] C_element120  label="C_element : 067"  # scripted group (container) (typed FeaturePython)
  n = 5
  ref = C_element
FEATURE [App::DocumentObjectGroupPython] H_element108  label="H_element : 058"  # scripted group (container) (typed FeaturePython)
  n = 11
  ref = H_element
FEATURE [App::DocumentObjectGroupPython] N_element047  label="N_element : 020"  # scripted group (container) (typed FeaturePython)
  n = 1
  ref = N_element
FEATURE [App::DocumentObjectGroupPython] O_element102  label="O_element : 056"  # scripted group (container) (typed FeaturePython)
  n = 2
  ref = O_element
FEATURE [App::DocumentObjectGroupPython] G4_VALINE  # scripted group (container) (typed FeaturePython)
  Dunit = g/cm3
  Dvalue = 1.23
  Group = -> [C_element120,H_element108,N_element047,O_element102]
  conduct = 2
  density = 1
  expand = 3
  formula = G4_VALINE
  name = G4_VALINE
  specific = 4
FEATURE [App::DocumentObjectGroupPython] H_element109  label="H_element : 0.009"  # scripted group (container) (typed FeaturePython)
  n = 0.009417
FEATURE [App::DocumentObjectGroupPython] C_element121  label="C_element : 0.281"  # scripted group (container) (typed FeaturePython)
  n = 0.280555
FEATURE [App::DocumentObjectGroupPython] F_element018  label="F_element : 0.710"  # scripted group (container) (typed FeaturePython)
  n = 0.710028
FEATURE [App::DocumentObjectGroupPython] G4_VITON  # scripted group (container) (typed FeaturePython)
  Dunit = g/cm3
  Dvalue = 1.8
  Group = -> [H_element109,C_element121,F_element018]
  conduct = 2
  density = 1
  expand = 3
  formula = G4_VITON
  name = G4_VITON
  specific = 4
FEATURE [App::DocumentObjectGroupPython] H_element110  label="H_element : 059"  # scripted group (container) (typed FeaturePython)
  n = 2
  ref = H_element
FEATURE [App::DocumentObjectGroupPython] O_element103  label="O_element : 057"  # scripted group (container) (typed FeaturePython)
  n = 1
  ref = O_element
FEATURE [App::DocumentObjectGroupPython] G4_WATER  # scripted group (container) (typed FeaturePython)
  Dunit = g/cm3
  Dvalue = 1
  Group = -> [H_element110,O_element103]
  conduct = 2
  density = 1
  expand = 3
  formula = G4_WATER
  name = G4_WATER
  specific = 4
FEATURE [App::DocumentObjectGroupPython] H_element111  label="H_element : 060"  # scripted group (container) (typed FeaturePython)
  n = 2
  ref = H_element
FEATURE [App::DocumentObjectGroupPython] O_element104  label="O_element : 058"  # scripted group (container) (typed FeaturePython)
  n = 1
  ref = O_element
FEATURE [App::DocumentObjectGroupPython] G4_WATER_VAPOR  # scripted group (container) (typed FeaturePython)
  Dunit = g/cm3
  Dvalue = 0.000756182
  Group = -> [H_element111,O_element104]
  conduct = 2
  density = 1
  expand = 3
  formula = G4_WATER_VAPOR
  name = G4_WATER_VAPOR
  specific = 4
FEATURE [App::DocumentObjectGroupPython] C_element122  label="C_element : 068"  # scripted group (container) (typed FeaturePython)
  n = 8
  ref = C_element
FEATURE [App::DocumentObjectGroupPython] H_element112  label="H_element : 061"  # scripted group (container) (typed FeaturePython)
  n = 10
  ref = H_element
FEATURE [App::DocumentObjectGroupPython] G4_XYLENE  # scripted group (container) (typed FeaturePython)
  Dunit = g/cm3
  Dvalue = 0.87
  Group = -> [C_element122,H_element112]
  conduct = 2
  density = 1
  expand = 3
  formula = G4_XYLENE
  name = G4_XYLENE
  specific = 4
FEATURE [App::DocumentObjectGroupPython] C_element123  label="C_element : 069"  # scripted group (container) (typed FeaturePython)
  n = 1
  ref = C_element
FEATURE [App::DocumentObjectGroupPython] G4_GRAPHITE  # scripted group (container) (typed FeaturePython)
  Dunit = g/cm3
  Dvalue = 2.21
  Group = -> [C_element123]
  conduct = 2
  density = 1
  expand = 3
  formula = G4_GRAPHITE
  name = G4_GRAPHITE
  specific = 4
FEATURE [App::DocumentObjectGroupPython] NIST  # scripted group (container) (typed FeaturePython)
  Group = -> [G4_A_150_TISSUE,G4_ACETONE,G4_ACETYLENE,G4_ADENINE,G4_ADIPOSE_TISSUE_ICRP,G4_AIR,G4_ALANINE,G4_ALUMINUM_OXIDE,G4_AMBER,G4_AMMONIA,G4_ANILINE,G4_ANTHRACENE,G4_B_100_BONE,G4_BAKELITE,G4_BARIUM_FLUORIDE,G4_BARIUM_SULFATE,G4_BENZENE,G4_BERYLLIUM_OXIDE,G4_BGO,G4_BLOOD_ICRP,G4_BONE_COMPACT_ICRU,G4_BONE_CORTICAL_ICRP,G4_BORON_CARBIDE,G4_BORON_OXIDE,G4_BRAIN_ICRP,G4_BUTANE,G4_N_BUTYL_ALCOHOL,G4_C_552,+152 more]
FEATURE [App::DocumentObjectGroupPython] H_element113  label="H_element : 062"  # scripted group (container) (typed FeaturePython)
  n = 1
  ref = H_element
FEATURE [App::DocumentObjectGroupPython] G4_H  # scripted group (container) (typed FeaturePython)
  Dunit = g/cm3
  Dvalue = 8.3748e-05
  Group = -> [H_element113]
  conduct = 2
  density = 1
  expand = 3
  formula = H
  name = G4_H
  specific = 4
FEATURE [App::DocumentObjectGroupPython] He_element001  label="He_element : 1"  # scripted group (container) (typed FeaturePython)
  n = 1
  ref = He_element
FEATURE [App::DocumentObjectGroupPython] G4_He  # scripted group (container) (typed FeaturePython)
  Dunit = g/cm3
  Dvalue = 0.000166322
  Group = -> [He_element001]
  conduct = 2
  density = 1
  expand = 3
  formula = He
  name = G4_He
  specific = 4
FEATURE [App::DocumentObjectGroupPython] Li_element008  label="Li_element : 008"  # scripted group (container) (typed FeaturePython)
  n = 1
  ref = Li_element
FEATURE [App::DocumentObjectGroupPython] G4_Li  # scripted group (container) (typed FeaturePython)
  Dunit = g/cm3
  Dvalue = 0.534
  Group = -> [Li_element008]
  conduct = 2
  density = 1
  expand = 3
  formula = Li
  name = G4_Li
  specific = 4
FEATURE [App::DocumentObjectGroupPython] Be_element002  label="Be_element : 002"  # scripted group (container) (typed FeaturePython)
  n = 1
  ref = Be_element
FEATURE [App::DocumentObjectGroupPython] G4_Be  # scripted group (container) (typed FeaturePython)
  Dunit = g/cm3
  Dvalue = 1.848
  Group = -> [Be_element002]
  conduct = 2
  density = 1
  expand = 3
  formula = Be
  name = G4_Be
  specific = 4
FEATURE [App::DocumentObjectGroupPython] B_element007  label="B_element : 007"  # scripted group (container) (typed FeaturePython)
  n = 1
  ref = B_element
FEATURE [App::DocumentObjectGroupPython] G4_B  # scripted group (container) (typed FeaturePython)
  Dunit = g/cm3
  Dvalue = 2.37
  Group = -> [B_element007]
  conduct = 2
  density = 1
  expand = 3
  formula = B
  name = G4_B
  specific = 4
FEATURE [App::DocumentObjectGroupPython] C_element124  label="C_element : 070"  # scripted group (container) (typed FeaturePython)
  n = 1
  ref = C_element
FEATURE [App::DocumentObjectGroupPython] G4_C  # scripted group (container) (typed FeaturePython)
  Dunit = g/cm3
  Dvalue = 2
  Group = -> [C_element124]
  conduct = 2
  density = 1
  expand = 3
  formula = C
  name = G4_C
  specific = 4
FEATURE [App::DocumentObjectGroupPython] N_element048  label="N_element : 021"  # scripted group (container) (typed FeaturePython)
  n = 1
  ref = N_element
FEATURE [App::DocumentObjectGroupPython] G4_N  # scripted group (container) (typed FeaturePython)
  Dunit = g/cm3
  Dvalue = 0.0011652
  Group = -> [N_element048]
  conduct = 2
  density = 1
  expand = 3
  formula = N
  name = G4_N
  specific = 4
FEATURE [App::DocumentObjectGroupPython] O_element105  label="O_element : 059"  # scripted group (container) (typed FeaturePython)
  n = 1
  ref = O_element
FEATURE [App::DocumentObjectGroupPython] G4_O  # scripted group (container) (typed FeaturePython)
  Dunit = g/cm3
  Dvalue = 0.00133151
  Group = -> [O_element105]
  conduct = 2
  density = 1
  expand = 3
  formula = O
  name = G4_O
  specific = 4
FEATURE [App::DocumentObjectGroupPython] F_element019  label="F_element : 008"  # scripted group (container) (typed FeaturePython)
  n = 1
  ref = F_element
FEATURE [App::DocumentObjectGroupPython] G4_F  # scripted group (container) (typed FeaturePython)
  Dunit = g/cm3
  Dvalue = 0.00158029
  Group = -> [F_element019]
  conduct = 2
  density = 1
  expand = 3
  formula = F
  name = G4_F
  specific = 4
FEATURE [App::DocumentObjectGroupPython] Ne_element001  label="Ne_element : 1"  # scripted group (container) (typed FeaturePython)
  n = 1
  ref = Ne_element
FEATURE [App::DocumentObjectGroupPython] G4_Ne  # scripted group (container) (typed FeaturePython)
  Dunit = g/cm3
  Dvalue = 0.000838505
  Group = -> [Ne_element001]
  conduct = 2
  density = 1
  expand = 3
  formula = Ne
  name = G4_Ne
  specific = 4
FEATURE [App::DocumentObjectGroupPython] Na_element020  label="Na_element : 005"  # scripted group (container) (typed FeaturePython)
  n = 1
  ref = Na_element
FEATURE [App::DocumentObjectGroupPython] G4_Na  # scripted group (container) (typed FeaturePython)
  Dunit = g/cm3
  Dvalue = 0.971
  Group = -> [Na_element020]
  conduct = 2
  density = 1
  expand = 3
  formula = Na
  name = G4_Na
  specific = 4
FEATURE [App::DocumentObjectGroupPython] Mg_element011  label="Mg_element : 005"  # scripted group (container) (typed FeaturePython)
  n = 1
  ref = Mg_element
FEATURE [App::DocumentObjectGroupPython] G4_Mg  # scripted group (container) (typed FeaturePython)
  Dunit = g/cm3
  Dvalue = 1.74
  Group = -> [Mg_element011]
  conduct = 2
  density = 1
  expand = 3
  formula = Mg
  name = G4_Mg
  specific = 4
FEATURE [App::DocumentObjectGroupPython] Al_element004  label="Al_element : 1"  # scripted group (container) (typed FeaturePython)
  n = 1
  ref = Al_element
FEATURE [App::DocumentObjectGroupPython] G4_Al  # scripted group (container) (typed FeaturePython)
  Dunit = g/cm3
  Dvalue = 2.699
  Group = -> [Al_element004]
  conduct = 2
  density = 1
  expand = 3
  formula = Al
  name = G4_Al
  specific = 4
FEATURE [App::DocumentObjectGroupPython] Si_element007  label="Si_element : 002"  # scripted group (container) (typed FeaturePython)
  n = 1
  ref = Si_element
FEATURE [App::DocumentObjectGroupPython] G4_Si  # scripted group (container) (typed FeaturePython)
  Dunit = g/cm3
  Dvalue = 2.33
  Group = -> [Si_element007]
  conduct = 2
  density = 1
  expand = 3
  formula = Si
  name = G4_Si
  specific = 4
FEATURE [App::DocumentObjectGroupPython] P_element013  label="P_element : 002"  # scripted group (container) (typed FeaturePython)
  n = 1
  ref = P_element
FEATURE [App::DocumentObjectGroupPython] G4_P  # scripted group (container) (typed FeaturePython)
  Dunit = g/cm3
  Dvalue = 2.2
  Group = -> [P_element013]
  conduct = 2
  density = 1
  expand = 3
  formula = P
  name = G4_P
  specific = 4
FEATURE [App::DocumentObjectGroupPython] S_element023  label="S_element : 007"  # scripted group (container) (typed FeaturePython)
  n = 1
  ref = S_element
FEATURE [App::DocumentObjectGroupPython] G4_S  # scripted group (container) (typed FeaturePython)
  Dunit = g/cm3
  Dvalue = 2
  Group = -> [S_element023]
  conduct = 2
  density = 1
  expand = 3
  formula = S
  name = G4_S
  specific = 4
FEATURE [App::DocumentObjectGroupPython] Cl_element029  label="Cl_element : 015"  # scripted group (container) (typed FeaturePython)
  n = 1
  ref = Cl_element
FEATURE [App::DocumentObjectGroupPython] G4_Cl  # scripted group (container) (typed FeaturePython)
  Dunit = g/cm3
  Dvalue = 0.00299473
  Group = -> [Cl_element029]
  conduct = 2
  density = 1
  expand = 3
  formula = Cl
  name = G4_Cl
  specific = 4
FEATURE [App::DocumentObjectGroupPython] Ar_element002  label="Ar_element : 1"  # scripted group (container) (typed FeaturePython)
  n = 1
  ref = Ar_element
FEATURE [App::DocumentObjectGroupPython] G4_Ar  # scripted group (container) (typed FeaturePython)
  Dunit = g/cm3
  Dvalue = 0.00166201
  Group = -> [Ar_element002]
  conduct = 2
  density = 1
  expand = 3
  formula = Ar
  name = G4_Ar
  specific = 4
FEATURE [App::DocumentObjectGroupPython] K_element013  label="K_element : 003"  # scripted group (container) (typed FeaturePython)
  n = 1
  ref = K_element
FEATURE [App::DocumentObjectGroupPython] G4_K  # scripted group (container) (typed FeaturePython)
  Dunit = g/cm3
  Dvalue = 0.862
  Group = -> [K_element013]
  conduct = 2
  density = 1
  expand = 3
  formula = K
  name = G4_K
  specific = 4
FEATURE [App::DocumentObjectGroupPython] Ca_element014  label="Ca_element : 007"  # scripted group (container) (typed FeaturePython)
  n = 1
  ref = Ca_element
FEATURE [App::DocumentObjectGroupPython] G4_Ca  # scripted group (container) (typed FeaturePython)
  Dunit = g/cm3
  Dvalue = 1.55
  Group = -> [Ca_element014]
  conduct = 2
  density = 1
  expand = 3
  formula = Ca
  name = G4_Ca
  specific = 4
FEATURE [App::DocumentObjectGroupPython] Sc_element001  label="Sc_element : 1"  # scripted group (container) (typed FeaturePython)
  n = 1
  ref = Sc_element
FEATURE [App::DocumentObjectGroupPython] G4_Sc  # scripted group (container) (typed FeaturePython)
  Dunit = g/cm3
  Dvalue = 2.989
  Group = -> [Sc_element001]
  conduct = 2
  density = 1
  expand = 3
  formula = Sc
  name = G4_Sc
  specific = 4
FEATURE [App::DocumentObjectGroupPython] Ti_element004  label="Ti_element : 002"  # scripted group (container) (typed FeaturePython)
  n = 1
  ref = Ti_element
FEATURE [App::DocumentObjectGroupPython] G4_Ti  # scripted group (container) (typed FeaturePython)
  Dunit = g/cm3
  Dvalue = 4.54
  Group = -> [Ti_element004]
  conduct = 2
  density = 1
  expand = 3
  formula = Ti
  name = G4_Ti
  specific = 4
FEATURE [App::DocumentObjectGroupPython] V_element001  label="V_element : 1"  # scripted group (container) (typed FeaturePython)
  n = 1
  ref = V_element
FEATURE [App::DocumentObjectGroupPython] G4_V  # scripted group (container) (typed FeaturePython)
  Dunit = g/cm3
  Dvalue = 6.11
  Group = -> [V_element001]
  conduct = 2
  density = 1
  expand = 3
  formula = V
  name = G4_V
  specific = 4
FEATURE [App::DocumentObjectGroupPython] Cr_element001  label="Cr_element : 1"  # scripted group (container) (typed FeaturePython)
  n = 1
  ref = Cr_element
FEATURE [App::DocumentObjectGroupPython] G4_Cr  # scripted group (container) (typed FeaturePython)
  Dunit = g/cm3
  Dvalue = 7.18
  Group = -> [Cr_element001]
  conduct = 2
  density = 1
  expand = 3
  formula = Cr
  name = G4_Cr
  specific = 4
FEATURE [App::DocumentObjectGroupPython] Mn_element001  label="Mn_element : 1"  # scripted group (container) (typed FeaturePython)
  n = 1
  ref = Mn_element
FEATURE [App::DocumentObjectGroupPython] G4_Mn  # scripted group (container) (typed FeaturePython)
  Dunit = g/cm3
  Dvalue = 7.44
  Group = -> [Mn_element001]
  conduct = 2
  density = 1
  expand = 3
  formula = Mn
  name = G4_Mn
  specific = 4
FEATURE [App::DocumentObjectGroupPython] Fe_element007  label="Fe_element : 004"  # scripted group (container) (typed FeaturePython)
  n = 1
  ref = Fe_element
FEATURE [App::DocumentObjectGroupPython] G4_Fe  # scripted group (container) (typed FeaturePython)
  Dunit = g/cm3
  Dvalue = 7.874
  Group = -> [Fe_element007]
  conduct = 2
  density = 1
  expand = 3
  formula = Fe
  name = G4_Fe
  specific = 4
FEATURE [App::DocumentObjectGroupPython] Co_element001  label="Co_element : 1"  # scripted group (container) (typed FeaturePython)
  n = 1
  ref = Co_element
FEATURE [App::DocumentObjectGroupPython] G4_Co  # scripted group (container) (typed FeaturePython)
  Dunit = g/cm3
  Dvalue = 8.9
  Group = -> [Co_element001]
  conduct = 2
  density = 1
  expand = 3
  formula = Co
  name = G4_Co
  specific = 4
FEATURE [App::DocumentObjectGroupPython] Ni_element001  label="Ni_element : 1"  # scripted group (container) (typed FeaturePython)
  n = 1
  ref = Ni_element
FEATURE [App::DocumentObjectGroupPython] G4_Ni  # scripted group (container) (typed FeaturePython)
  Dunit = g/cm3
  Dvalue = 8.902
  Group = -> [Ni_element001]
  conduct = 2
  density = 1
  expand = 3
  formula = Ni
  name = G4_Ni
  specific = 4
FEATURE [App::DocumentObjectGroupPython] Cu_element001  label="Cu_element : 1"  # scripted group (container) (typed FeaturePython)
  n = 1
  ref = Cu_element
FEATURE [App::DocumentObjectGroupPython] G4_Cu  # scripted group (container) (typed FeaturePython)
  Dunit = g/cm3
  Dvalue = 8.96
  Group = -> [Cu_element001]
  conduct = 2
  density = 1
  expand = 3
  formula = Cu
  name = G4_Cu
  specific = 4
FEATURE [App::DocumentObjectGroupPython] Zn_element001  label="Zn_element : 1"  # scripted group (container) (typed FeaturePython)
  n = 1
  ref = Zn_element
FEATURE [App::DocumentObjectGroupPython] G4_Zn  # scripted group (container) (typed FeaturePython)
  Dunit = g/cm3
  Dvalue = 7.133
  Group = -> [Zn_element001]
  conduct = 2
  density = 1
  expand = 3
  formula = Zn
  name = G4_Zn
  specific = 4
FEATURE [App::DocumentObjectGroupPython] Ga_element002  label="Ga_element : 002"  # scripted group (container) (typed FeaturePython)
  n = 1
  ref = Ga_element
FEATURE [App::DocumentObjectGroupPython] G4_Ga  # scripted group (container) (typed FeaturePython)
  Dunit = g/cm3
  Dvalue = 5.904
  Group = -> [Ga_element002]
  conduct = 2
  density = 1
  expand = 3
  formula = Ga
  name = G4_Ga
  specific = 4
FEATURE [App::DocumentObjectGroupPython] Ge_element002  label="Ge_element : 1"  # scripted group (container) (typed FeaturePython)
  n = 1
  ref = Ge_element
FEATURE [App::DocumentObjectGroupPython] G4_Ge  # scripted group (container) (typed FeaturePython)
  Dunit = g/cm3
  Dvalue = 5.323
  Group = -> [Ge_element002]
  conduct = 2
  density = 1
  expand = 3
  formula = Ge
  name = G4_Ge
  specific = 4
FEATURE [App::DocumentObjectGroupPython] As_element003  label="As_element : 002"  # scripted group (container) (typed FeaturePython)
  n = 1
  ref = As_element
FEATURE [App::DocumentObjectGroupPython] G4_As  # scripted group (container) (typed FeaturePython)
  Dunit = g/cm3
  Dvalue = 5.73
  Group = -> [As_element003]
  conduct = 2
  density = 1
  expand = 3
  formula = As
  name = G4_As
  specific = 4
FEATURE [App::DocumentObjectGroupPython] Se_element001  label="Se_element : 1"  # scripted group (container) (typed FeaturePython)
  n = 1
  ref = Se_element
FEATURE [App::DocumentObjectGroupPython] G4_Se  # scripted group (container) (typed FeaturePython)
  Dunit = g/cm3
  Dvalue = 4.5
  Group = -> [Se_element001]
  conduct = 2
  density = 1
  expand = 3
  formula = Se
  name = G4_Se
  specific = 4
FEATURE [App::DocumentObjectGroupPython] Br_element007  label="Br_element : 004"  # scripted group (container) (typed FeaturePython)
  n = 1
  ref = Br_element
FEATURE [App::DocumentObjectGroupPython] G4_Br  # scripted group (container) (typed FeaturePython)
  Dunit = g/cm3
  Dvalue = 0.0070721
  Group = -> [Br_element007]
  conduct = 2
  density = 1
  expand = 3
  formula = Br
  name = G4_Br
  specific = 4
FEATURE [App::DocumentObjectGroupPython] Kr_element001  label="Kr_element : 1"  # scripted group (container) (typed FeaturePython)
  n = 1
  ref = Kr_element
FEATURE [App::DocumentObjectGroupPython] G4_Kr  # scripted group (container) (typed FeaturePython)
  Dunit = g/cm3
  Dvalue = 0.00347832
  Group = -> [Kr_element001]
  conduct = 2
  density = 1
  expand = 3
  formula = Kr
  name = G4_Kr
  specific = 4
FEATURE [App::DocumentObjectGroupPython] Rb_element001  label="Rb_element : 1"  # scripted group (container) (typed FeaturePython)
  n = 1
  ref = Rb_element
FEATURE [App::DocumentObjectGroupPython] G4_Rb  # scripted group (container) (typed FeaturePython)
  Dunit = g/cm3
  Dvalue = 1.532
  Group = -> [Rb_element001]
  conduct = 2
  density = 1
  expand = 3
  formula = Rb
  name = G4_Rb
  specific = 4
FEATURE [App::DocumentObjectGroupPython] Sr_element001  label="Sr_element : 1"  # scripted group (container) (typed FeaturePython)
  n = 1
  ref = Sr_element
FEATURE [App::DocumentObjectGroupPython] G4_Sr  # scripted group (container) (typed FeaturePython)
  Dunit = g/cm3
  Dvalue = 2.54
  Group = -> [Sr_element001]
  conduct = 2
  density = 1
  expand = 3
  formula = Sr
  name = G4_Sr
  specific = 4
FEATURE [App::DocumentObjectGroupPython] Y_element001  label="Y_element : 1"  # scripted group (container) (typed FeaturePython)
  n = 1
  ref = Y_element
FEATURE [App::DocumentObjectGroupPython] G4_Y  # scripted group (container) (typed FeaturePython)
  Dunit = g/cm3
  Dvalue = 4.469
  Group = -> [Y_element001]
  conduct = 2
  density = 1
  expand = 3
  formula = Y
  name = G4_Y
  specific = 4
FEATURE [App::DocumentObjectGroupPython] Zr_element001  label="Zr_element : 1"  # scripted group (container) (typed FeaturePython)
  n = 1
  ref = Zr_element
FEATURE [App::DocumentObjectGroupPython] G4_Zr  # scripted group (container) (typed FeaturePython)
  Dunit = g/cm3
  Dvalue = 6.506
  Group = -> [Zr_element001]
  conduct = 2
  density = 1
  expand = 3
  formula = Zr
  name = G4_Zr
  specific = 4
FEATURE [App::DocumentObjectGroupPython] Nb_element001  label="Nb_element : 1"  # scripted group (container) (typed FeaturePython)
  n = 1
  ref = Nb_element
FEATURE [App::DocumentObjectGroupPython] G4_Nb  # scripted group (container) (typed FeaturePython)
  Dunit = g/cm3
  Dvalue = 8.57
  Group = -> [Nb_element001]
  conduct = 2
  density = 1
  expand = 3
  formula = Nb
  name = G4_Nb
  specific = 4
FEATURE [App::DocumentObjectGroupPython] Mo_element001  label="Mo_element : 1"  # scripted group (container) (typed FeaturePython)
  n = 1
  ref = Mo_element
FEATURE [App::DocumentObjectGroupPython] G4_Mo  # scripted group (container) (typed FeaturePython)
  Dunit = g/cm3
  Dvalue = 10.22
  Group = -> [Mo_element001]
  conduct = 2
  density = 1
  expand = 3
  formula = Mo
  name = G4_Mo
  specific = 4
FEATURE [App::DocumentObjectGroupPython] Tc_element001  label="Tc_element : 1"  # scripted group (container) (typed FeaturePython)
  n = 1
  ref = Tc_element
FEATURE [App::DocumentObjectGroupPython] G4_Tc  # scripted group (container) (typed FeaturePython)
  Dunit = g/cm3
  Dvalue = 11.5
  Group = -> [Tc_element001]
  conduct = 2
  density = 1
  expand = 3
  formula = Tc
  name = G4_Tc
  specific = 4
FEATURE [App::DocumentObjectGroupPython] Ru_element001  label="Ru_element : 1"  # scripted group (container) (typed FeaturePython)
  n = 1
  ref = Ru_element
FEATURE [App::DocumentObjectGroupPython] G4_Ru  # scripted group (container) (typed FeaturePython)
  Dunit = g/cm3
  Dvalue = 12.41
  Group = -> [Ru_element001]
  conduct = 2
  density = 1
  expand = 3
  formula = Ru
  name = G4_Ru
  specific = 4
FEATURE [App::DocumentObjectGroupPython] Rh_element001  label="Rh_element : 1"  # scripted group (container) (typed FeaturePython)
  n = 1
  ref = Rh_element
FEATURE [App::DocumentObjectGroupPython] G4_Rh  # scripted group (container) (typed FeaturePython)
  Dunit = g/cm3
  Dvalue = 12.41
  Group = -> [Rh_element001]
  conduct = 2
  density = 1
  expand = 3
  formula = Rh
  name = G4_Rh
  specific = 4
FEATURE [App::DocumentObjectGroupPython] Pd_element001  label="Pd_element : 1"  # scripted group (container) (typed FeaturePython)
  n = 1
  ref = Pd_element
FEATURE [App::DocumentObjectGroupPython] G4_Pd  # scripted group (container) (typed FeaturePython)
  Dunit = g/cm3
  Dvalue = 12.02
  Group = -> [Pd_element001]
  conduct = 2
  density = 1
  expand = 3
  formula = Pd
  name = G4_Pd
  specific = 4
FEATURE [App::DocumentObjectGroupPython] Ag_element006  label="Ag_element : 004"  # scripted group (container) (typed FeaturePython)
  n = 1
  ref = Ag_element
FEATURE [App::DocumentObjectGroupPython] G4_Ag  # scripted group (container) (typed FeaturePython)
  Dunit = g/cm3
  Dvalue = 10.5
  Group = -> [Ag_element006]
  conduct = 2
  density = 1
  expand = 3
  formula = Ag
  name = G4_Ag
  specific = 4
FEATURE [App::DocumentObjectGroupPython] Cd_element003  label="Cd_element : 003"  # scripted group (container) (typed FeaturePython)
  n = 1
  ref = Cd_element
FEATURE [App::DocumentObjectGroupPython] G4_Cd  # scripted group (container) (typed FeaturePython)
  Dunit = g/cm3
  Dvalue = 8.65
  Group = -> [Cd_element003]
  conduct = 2
  density = 1
  expand = 3
  formula = Cd
  name = G4_Cd
  specific = 4
FEATURE [App::DocumentObjectGroupPython] In_element001  label="In_element : 1"  # scripted group (container) (typed FeaturePython)
  n = 1
  ref = In_element
FEATURE [App::DocumentObjectGroupPython] G4_In  # scripted group (container) (typed FeaturePython)
  Dunit = g/cm3
  Dvalue = 7.31
  Group = -> [In_element001]
  conduct = 2
  density = 1
  expand = 3
  formula = In
  name = G4_In
  specific = 4
FEATURE [App::DocumentObjectGroupPython] Sn_element001  label="Sn_element : 1"  # scripted group (container) (typed FeaturePython)
  n = 1
  ref = Sn_element
FEATURE [App::DocumentObjectGroupPython] G4_Sn  # scripted group (container) (typed FeaturePython)
  Dunit = g/cm3
  Dvalue = 7.31
  Group = -> [Sn_element001]
  conduct = 2
  density = 1
  expand = 3
  formula = Sn
  name = G4_Sn
  specific = 4
FEATURE [App::DocumentObjectGroupPython] Sb_element001  label="Sb_element : 1"  # scripted group (container) (typed FeaturePython)
  n = 1
  ref = Sb_element
FEATURE [App::DocumentObjectGroupPython] G4_Sb  # scripted group (container) (typed FeaturePython)
  Dunit = g/cm3
  Dvalue = 6.691
  Group = -> [Sb_element001]
  conduct = 2
  density = 1
  expand = 3
  formula = Sb
  name = G4_Sb
  specific = 4
FEATURE [App::DocumentObjectGroupPython] Te_element002  label="Te_element : 002"  # scripted group (container) (typed FeaturePython)
  n = 1
  ref = Te_element
FEATURE [App::DocumentObjectGroupPython] G4_Te  # scripted group (container) (typed FeaturePython)
  Dunit = g/cm3
  Dvalue = 6.24
  Group = -> [Te_element002]
  conduct = 2
  density = 1
  expand = 3
  formula = Te
  name = G4_Te
  specific = 4
FEATURE [App::DocumentObjectGroupPython] I_element010  label="I_element : 006"  # scripted group (container) (typed FeaturePython)
  n = 1
  ref = I_element
FEATURE [App::DocumentObjectGroupPython] G4_I  # scripted group (container) (typed FeaturePython)
  Dunit = g/cm3
  Dvalue = 4.93
  Group = -> [I_element010]
  conduct = 2
  density = 1
  expand = 3
  formula = I
  name = G4_I
  specific = 4
FEATURE [App::DocumentObjectGroupPython] Xe_element001  label="Xe_element : 1"  # scripted group (container) (typed FeaturePython)
  n = 1
  ref = Xe_element
FEATURE [App::DocumentObjectGroupPython] G4_Xe  # scripted group (container) (typed FeaturePython)
  Dunit = g/cm3
  Dvalue = 0.00548536
  Group = -> [Xe_element001]
  conduct = 2
  density = 1
  expand = 3
  formula = Xe
  name = G4_Xe
  specific = 4
FEATURE [App::DocumentObjectGroupPython] Cs_element003  label="Cs_element : 003"  # scripted group (container) (typed FeaturePython)
  n = 1
  ref = Cs_element
FEATURE [App::DocumentObjectGroupPython] G4_Cs  # scripted group (container) (typed FeaturePython)
  Dunit = g/cm3
  Dvalue = 1.873
  Group = -> [Cs_element003]
  conduct = 2
  density = 1
  expand = 3
  formula = Cs
  name = G4_Cs
  specific = 4
FEATURE [App::DocumentObjectGroupPython] Ba_element003  label="Ba_element : 003"  # scripted group (container) (typed FeaturePython)
  n = 1
  ref = Ba_element
FEATURE [App::DocumentObjectGroupPython] G4_Ba  # scripted group (container) (typed FeaturePython)
  Dunit = g/cm3
  Dvalue = 3.5
  Group = -> [Ba_element003]
  conduct = 2
  density = 1
  expand = 3
  formula = Ba
  name = G4_Ba
  specific = 4
FEATURE [App::DocumentObjectGroupPython] La_element003  label="La_element : 003"  # scripted group (container) (typed FeaturePython)
  n = 1
  ref = La_element
FEATURE [App::DocumentObjectGroupPython] G4_La  # scripted group (container) (typed FeaturePython)
  Dunit = g/cm3
  Dvalue = 6.154
  Group = -> [La_element003]
  conduct = 2
  density = 1
  expand = 3
  formula = La
  name = G4_La
  specific = 4
FEATURE [App::DocumentObjectGroupPython] Ce_element002  label="Ce_element : 1"  # scripted group (container) (typed FeaturePython)
  n = 1
  ref = Ce_element
FEATURE [App::DocumentObjectGroupPython] G4_Ce  # scripted group (container) (typed FeaturePython)
  Dunit = g/cm3
  Dvalue = 6.657
  Group = -> [Ce_element002]
  conduct = 2
  density = 1
  expand = 3
  formula = Ce
  name = G4_Ce
  specific = 4
FEATURE [App::DocumentObjectGroupPython] Pr_element001  label="Pr_element : 1"  # scripted group (container) (typed FeaturePython)
  n = 1
  ref = Pr_element
FEATURE [App::DocumentObjectGroupPython] G4_Pr  # scripted group (container) (typed FeaturePython)
  Dunit = g/cm3
  Dvalue = 6.71
  Group = -> [Pr_element001]
  conduct = 2
  density = 1
  expand = 3
  formula = Pr
  name = G4_Pr
  specific = 4
FEATURE [App::DocumentObjectGroupPython] Nd_element001  label="Nd_element : 1"  # scripted group (container) (typed FeaturePython)
  n = 1
  ref = Nd_element
FEATURE [App::DocumentObjectGroupPython] G4_Nd  # scripted group (container) (typed FeaturePython)
  Dunit = g/cm3
  Dvalue = 6.9
  Group = -> [Nd_element001]
  conduct = 2
  density = 1
  expand = 3
  formula = Nd
  name = G4_Nd
  specific = 4
FEATURE [App::DocumentObjectGroupPython] Pm_element001  label="Pm_element : 1"  # scripted group (container) (typed FeaturePython)
  n = 1
  ref = Pm_element
FEATURE [App::DocumentObjectGroupPython] G4_Pm  # scripted group (container) (typed FeaturePython)
  Dunit = g/cm3
  Dvalue = 7.22
  Group = -> [Pm_element001]
  conduct = 2
  density = 1
  expand = 3
  formula = Pm
  name = G4_Pm
  specific = 4
FEATURE [App::DocumentObjectGroupPython] Sm_element001  label="Sm_element : 1"  # scripted group (container) (typed FeaturePython)
  n = 1
  ref = Sm_element
FEATURE [App::DocumentObjectGroupPython] G4_Sm  # scripted group (container) (typed FeaturePython)
  Dunit = g/cm3
  Dvalue = 7.46
  Group = -> [Sm_element001]
  conduct = 2
  density = 1
  expand = 3
  formula = Sm
  name = G4_Sm
  specific = 4
FEATURE [App::DocumentObjectGroupPython] Eu_element001  label="Eu_element : 1"  # scripted group (container) (typed FeaturePython)
  n = 1
  ref = Eu_element
FEATURE [App::DocumentObjectGroupPython] G4_Eu  # scripted group (container) (typed FeaturePython)
  Dunit = g/cm3
  Dvalue = 5.243
  Group = -> [Eu_element001]
  conduct = 2
  density = 1
  expand = 3
  formula = Eu
  name = G4_Eu
  specific = 4
FEATURE [App::DocumentObjectGroupPython] Gd_element002  label="Gd_element : 1"  # scripted group (container) (typed FeaturePython)
  n = 1
  ref = Gd_element
FEATURE [App::DocumentObjectGroupPython] G4_Gd  # scripted group (container) (typed FeaturePython)
  Dunit = g/cm3
  Dvalue = 7.9004
  Group = -> [Gd_element002]
  conduct = 2
  density = 1
  expand = 3
  formula = Gd
  name = G4_Gd
  specific = 4
FEATURE [App::DocumentObjectGroupPython] Tb_element001  label="Tb_element : 1"  # scripted group (container) (typed FeaturePython)
  n = 1
  ref = Tb_element
FEATURE [App::DocumentObjectGroupPython] G4_Tb  # scripted group (container) (typed FeaturePython)
  Dunit = g/cm3
  Dvalue = 8.229
  Group = -> [Tb_element001]
  conduct = 2
  density = 1
  expand = 3
  formula = Tb
  name = G4_Tb
  specific = 4
FEATURE [App::DocumentObjectGroupPython] Dy_element001  label="Dy_element : 1"  # scripted group (container) (typed FeaturePython)
  n = 1
  ref = Dy_element
FEATURE [App::DocumentObjectGroupPython] G4_Dy  # scripted group (container) (typed FeaturePython)
  Dunit = g/cm3
  Dvalue = 8.55
  Group = -> [Dy_element001]
  conduct = 2
  density = 1
  expand = 3
  formula = Dy
  name = G4_Dy
  specific = 4
FEATURE [App::DocumentObjectGroupPython] Ho_element001  label="Ho_element : 1"  # scripted group (container) (typed FeaturePython)
  n = 1
  ref = Ho_element
FEATURE [App::DocumentObjectGroupPython] G4_Ho  # scripted group (container) (typed FeaturePython)
  Dunit = g/cm3
  Dvalue = 8.795
  Group = -> [Ho_element001]
  conduct = 2
  density = 1
  expand = 3
  formula = Ho
  name = G4_Ho
  specific = 4
FEATURE [App::DocumentObjectGroupPython] Er_element001  label="Er_element : 1"  # scripted group (container) (typed FeaturePython)
  n = 1
  ref = Er_element
FEATURE [App::DocumentObjectGroupPython] G4_Er  # scripted group (container) (typed FeaturePython)
  Dunit = g/cm3
  Dvalue = 9.066
  Group = -> [Er_element001]
  conduct = 2
  density = 1
  expand = 3
  formula = Er
  name = G4_Er
  specific = 4
FEATURE [App::DocumentObjectGroupPython] Tm_element001  label="Tm_element : 1"  # scripted group (container) (typed FeaturePython)
  n = 1
  ref = Tm_element
FEATURE [App::DocumentObjectGroupPython] G4_Tm  # scripted group (container) (typed FeaturePython)
  Dunit = g/cm3
  Dvalue = 9.321
  Group = -> [Tm_element001]
  conduct = 2
  density = 1
  expand = 3
  formula = Tm
  name = G4_Tm
  specific = 4
FEATURE [App::DocumentObjectGroupPython] Yb_element001  label="Yb_element : 1"  # scripted group (container) (typed FeaturePython)
  n = 1
  ref = Yb_element
FEATURE [App::DocumentObjectGroupPython] G4_Yb  # scripted group (container) (typed FeaturePython)
  Dunit = g/cm3
  Dvalue = 6.73
  Group = -> [Yb_element001]
  conduct = 2
  density = 1
  expand = 3
  formula = Yb
  name = G4_Yb
  specific = 4
FEATURE [App::DocumentObjectGroupPython] Lu_element001  label="Lu_element : 1"  # scripted group (container) (typed FeaturePython)
  n = 1
  ref = Lu_element
FEATURE [App::DocumentObjectGroupPython] G4_Lu  # scripted group (container) (typed FeaturePython)
  Dunit = g/cm3
  Dvalue = 9.84
  Group = -> [Lu_element001]
  conduct = 2
  density = 1
  expand = 3
  formula = Lu
  name = G4_Lu
  specific = 4
FEATURE [App::DocumentObjectGroupPython] Hf_element001  label="Hf_element : 1"  # scripted group (container) (typed FeaturePython)
  n = 1
  ref = Hf_element
FEATURE [App::DocumentObjectGroupPython] G4_Hf  # scripted group (container) (typed FeaturePython)
  Dunit = g/cm3
  Dvalue = 13.31
  Group = -> [Hf_element001]
  conduct = 2
  density = 1
  expand = 3
  formula = Hf
  name = G4_Hf
  specific = 4
FEATURE [App::DocumentObjectGroupPython] Ta_element001  label="Ta_element : 1"  # scripted group (container) (typed FeaturePython)
  n = 1
  ref = Ta_element
FEATURE [App::DocumentObjectGroupPython] G4_Ta  # scripted group (container) (typed FeaturePython)
  Dunit = g/cm3
  Dvalue = 16.654
  Group = -> [Ta_element001]
  conduct = 2
  density = 1
  expand = 3
  formula = Ta
  name = G4_Ta
  specific = 4
FEATURE [App::DocumentObjectGroupPython] W_element004  label="W_element : 004"  # scripted group (container) (typed FeaturePython)
  n = 1
  ref = W_element
FEATURE [App::DocumentObjectGroupPython] G4_W  # scripted group (container) (typed FeaturePython)
  Dunit = g/cm3
  Dvalue = 19.3
  Group = -> [W_element004]
  conduct = 2
  density = 1
  expand = 3
  formula = W
  name = G4_W
  specific = 4
FEATURE [App::DocumentObjectGroupPython] Re_element001  label="Re_element : 1"  # scripted group (container) (typed FeaturePython)
  n = 1
  ref = Re_element
FEATURE [App::DocumentObjectGroupPython] G4_Re  # scripted group (container) (typed FeaturePython)
  Dunit = g/cm3
  Dvalue = 21.02
  Group = -> [Re_element001]
  conduct = 2
  density = 1
  expand = 3
  formula = Re
  name = G4_Re
  specific = 4
FEATURE [App::DocumentObjectGroupPython] Os_element001  label="Os_element : 1"  # scripted group (container) (typed FeaturePython)
  n = 1
  ref = Os_element
FEATURE [App::DocumentObjectGroupPython] G4_Os  # scripted group (container) (typed FeaturePython)
  Dunit = g/cm3
  Dvalue = 22.57
  Group = -> [Os_element001]
  conduct = 2
  density = 1
  expand = 3
  formula = Os
  name = G4_Os
  specific = 4
FEATURE [App::DocumentObjectGroupPython] Ir_element001  label="Ir_element : 1"  # scripted group (container) (typed FeaturePython)
  n = 1
  ref = Ir_element
FEATURE [App::DocumentObjectGroupPython] G4_Ir  # scripted group (container) (typed FeaturePython)
  Dunit = g/cm3
  Dvalue = 22.42
  Group = -> [Ir_element001]
  conduct = 2
  density = 1
  expand = 3
  formula = Ir
  name = G4_Ir
  specific = 4
FEATURE [App::DocumentObjectGroupPython] Pt_element001  label="Pt_element : 1"  # scripted group (container) (typed FeaturePython)
  n = 1
  ref = Pt_element
FEATURE [App::DocumentObjectGroupPython] G4_Pt  # scripted group (container) (typed FeaturePython)
  Dunit = g/cm3
  Dvalue = 21.45
  Group = -> [Pt_element001]
  conduct = 2
  density = 1
  expand = 3
  formula = Pt
  name = G4_Pt
  specific = 4
FEATURE [App::DocumentObjectGroupPython] Au_element001  label="Au_element : 1"  # scripted group (container) (typed FeaturePython)
  n = 1
  ref = Au_element
FEATURE [App::DocumentObjectGroupPython] G4_Au  # scripted group (container) (typed FeaturePython)
  Dunit = g/cm3
  Dvalue = 19.32
  Group = -> [Au_element001]
  conduct = 2
  density = 1
  expand = 3
  formula = Au
  name = G4_Au
  specific = 4
FEATURE [App::DocumentObjectGroupPython] Hg_element002  label="Hg_element : 002"  # scripted group (container) (typed FeaturePython)
  n = 1
  ref = Hg_element
FEATURE [App::DocumentObjectGroupPython] G4_Hg  # scripted group (container) (typed FeaturePython)
  Dunit = g/cm3
  Dvalue = 13.546
  Group = -> [Hg_element002]
  conduct = 2
  density = 1
  expand = 3
  formula = Hg
  name = G4_Hg
  specific = 4
FEATURE [App::DocumentObjectGroupPython] Tl_element002  label="Tl_element : 002"  # scripted group (container) (typed FeaturePython)
  n = 1
  ref = Tl_element
FEATURE [App::DocumentObjectGroupPython] G4_Tl  # scripted group (container) (typed FeaturePython)
  Dunit = g/cm3
  Dvalue = 11.72
  Group = -> [Tl_element002]
  conduct = 2
  density = 1
  expand = 3
  formula = Tl
  name = G4_Tl
  specific = 4
FEATURE [App::DocumentObjectGroupPython] Pb_element003  label="Pb_element : 1"  # scripted group (container) (typed FeaturePython)
  n = 1
  ref = Pb_element
FEATURE [App::DocumentObjectGroupPython] G4_Pb  # scripted group (container) (typed FeaturePython)
  Dunit = g/cm3
  Dvalue = 11.35
  Group = -> [Pb_element003]
  conduct = 2
  density = 1
  expand = 3
  formula = Pb
  name = G4_Pb
  specific = 4
FEATURE [App::DocumentObjectGroupPython] Bi_element002  label="Bi_element : 1"  # scripted group (container) (typed FeaturePython)
  n = 1
  ref = Bi_element
FEATURE [App::DocumentObjectGroupPython] G4_Bi  # scripted group (container) (typed FeaturePython)
  Dunit = g/cm3
  Dvalue = 9.747
  Group = -> [Bi_element002]
  conduct = 2
  density = 1
  expand = 3
  formula = Bi
  name = G4_Bi
  specific = 4
FEATURE [App::DocumentObjectGroupPython] Po_element001  label="Po_element : 1"  # scripted group (container) (typed FeaturePython)
  n = 1
  ref = Po_element
FEATURE [App::DocumentObjectGroupPython] G4_Po  # scripted group (container) (typed FeaturePython)
  Dunit = g/cm3
  Dvalue = 9.32
  Group = -> [Po_element001]
  conduct = 2
  density = 1
  expand = 3
  formula = Po
  name = G4_Po
  specific = 4
FEATURE [App::DocumentObjectGroupPython] At_element001  label="At_element : 1"  # scripted group (container) (typed FeaturePython)
  n = 1
  ref = At_element
FEATURE [App::DocumentObjectGroupPython] G4_At  # scripted group (container) (typed FeaturePython)
  Dunit = g/cm3
  Dvalue = 9.32
  Group = -> [At_element001]
  conduct = 2
  density = 1
  expand = 3
  formula = At
  name = G4_At
  specific = 4
FEATURE [App::DocumentObjectGroupPython] Rn_element001  label="Rn_element : 1"  # scripted group (container) (typed FeaturePython)
  n = 1
  ref = Rn_element
FEATURE [App::DocumentObjectGroupPython] G4_Rn  # scripted group (container) (typed FeaturePython)
  Dunit = g/cm3
  Dvalue = 0.00900662
  Group = -> [Rn_element001]
  conduct = 2
  density = 1
  expand = 3
  formula = Rn
  name = G4_Rn
  specific = 4
FEATURE [App::DocumentObjectGroupPython] Fr_element001  label="Fr_element : 1"  # scripted group (container) (typed FeaturePython)
  n = 1
  ref = Fr_element
FEATURE [App::DocumentObjectGroupPython] G4_Fr  # scripted group (container) (typed FeaturePython)
  Dunit = g/cm3
  Dvalue = 1
  Group = -> [Fr_element001]
  conduct = 2
  density = 1
  expand = 3
  formula = Fr
  name = G4_Fr
  specific = 4
FEATURE [App::DocumentObjectGroupPython] Ra_element001  label="Ra_element : 1"  # scripted group (container) (typed FeaturePython)
  n = 1
  ref = Ra_element
FEATURE [App::DocumentObjectGroupPython] G4_Ra  # scripted group (container) (typed FeaturePython)
  Dunit = g/cm3
  Dvalue = 5
  Group = -> [Ra_element001]
  conduct = 2
  density = 1
  expand = 3
  formula = Ra
  name = G4_Ra
  specific = 4
FEATURE [App::DocumentObjectGroupPython] Ac_element001  label="Ac_element : 1"  # scripted group (container) (typed FeaturePython)
  n = 1
  ref = Ac_element
FEATURE [App::DocumentObjectGroupPython] G4_Ac  # scripted group (container) (typed FeaturePython)
  Dunit = g/cm3
  Dvalue = 10.07
  Group = -> [Ac_element001]
  conduct = 2
  density = 1
  expand = 3
  formula = Ac
  name = G4_Ac
  specific = 4
FEATURE [App::DocumentObjectGroupPython] Th_element001  label="Th_element : 1"  # scripted group (container) (typed FeaturePython)
  n = 1
  ref = Th_element
FEATURE [App::DocumentObjectGroupPython] G4_Th  # scripted group (container) (typed FeaturePython)
  Dunit = g/cm3
  Dvalue = 11.72
  Group = -> [Th_element001]
  conduct = 2
  density = 1
  expand = 3
  formula = Th
  name = G4_Th
  specific = 4
FEATURE [App::DocumentObjectGroupPython] Pa_element001  label="Pa_element : 1"  # scripted group (container) (typed FeaturePython)
  n = 1
  ref = Pa_element
FEATURE [App::DocumentObjectGroupPython] G4_Pa  # scripted group (container) (typed FeaturePython)
  Dunit = g/cm3
  Dvalue = 15.37
  Group = -> [Pa_element001]
  conduct = 2
  density = 1
  expand = 3
  formula = Pa
  name = G4_Pa
  specific = 4
FEATURE [App::DocumentObjectGroupPython] U_element004  label="U_element : 004"  # scripted group (container) (typed FeaturePython)
  n = 1
  ref = U_element
FEATURE [App::DocumentObjectGroupPython] G4_U  # scripted group (container) (typed FeaturePython)
  Dunit = g/cm3
  Dvalue = 18.95
  Group = -> [U_element004]
  conduct = 2
  density = 1
  expand = 3
  formula = U
  name = G4_U
  specific = 4
FEATURE [App::DocumentObjectGroupPython] Np_element001  label="Np_element : 1"  # scripted group (container) (typed FeaturePython)
  n = 1
  ref = Np_element
FEATURE [App::DocumentObjectGroupPython] G4_Np  # scripted group (container) (typed FeaturePython)
  Dunit = g/cm3
  Dvalue = 20.25
  Group = -> [Np_element001]
  conduct = 2
  density = 1
  expand = 3
  formula = Np
  name = G4_Np
  specific = 4
FEATURE [App::DocumentObjectGroupPython] Pu_element002  label="Pu_element : 002"  # scripted group (container) (typed FeaturePython)
  n = 1
  ref = Pu_element
FEATURE [App::DocumentObjectGroupPython] G4_Pu  # scripted group (container) (typed FeaturePython)
  Dunit = g/cm3
  Dvalue = 19.84
  Group = -> [Pu_element002]
  conduct = 2
  density = 1
  expand = 3
  formula = Pu
  name = G4_Pu
  specific = 4
FEATURE [App::DocumentObjectGroupPython] Am_element001  label="Am_element : 1"  # scripted group (container) (typed FeaturePython)
  n = 1
  ref = Am_element
FEATURE [App::DocumentObjectGroupPython] G4_Am  # scripted group (container) (typed FeaturePython)
  Dunit = g/cm3
  Dvalue = 13.67
  Group = -> [Am_element001]
  conduct = 2
  density = 1
  expand = 3
  formula = Am
  name = G4_Am
  specific = 4
FEATURE [App::DocumentObjectGroupPython] Cm_element001  label="Cm_element : 1"  # scripted group (container) (typed FeaturePython)
  n = 1
  ref = Cm_element
FEATURE [App::DocumentObjectGroupPython] G4_Cm  # scripted group (container) (typed FeaturePython)
  Dunit = g/cm3
  Dvalue = 13.51
  Group = -> [Cm_element001]
  conduct = 2
  density = 1
  expand = 3
  formula = Cm
  name = G4_Cm
  specific = 4
FEATURE [App::DocumentObjectGroupPython] Bk_element001  label="Bk_element : 1"  # scripted group (container) (typed FeaturePython)
  n = 1
  ref = Bk_element
FEATURE [App::DocumentObjectGroupPython] G4_Bk  # scripted group (container) (typed FeaturePython)
  Dunit = g/cm3
  Dvalue = 14
  Group = -> [Bk_element001]
  conduct = 2
  density = 1
  expand = 3
  formula = Bk
  name = G4_Bk
  specific = 4
FEATURE [App::DocumentObjectGroupPython] Cf_element001  label="Cf_element : 1"  # scripted group (container) (typed FeaturePython)
  n = 1
  ref = Cf_element
FEATURE [App::DocumentObjectGroupPython] G4_Cf  # scripted group (container) (typed FeaturePython)
  Dunit = g/cm3
  Dvalue = 10
  Group = -> [Cf_element001]
  conduct = 2
  density = 1
  expand = 3
  formula = Cf
  name = G4_Cf
  specific = 4
FEATURE [App::DocumentObjectGroupPython] Element  # scripted group (container) (typed FeaturePython)
  Group = -> [G4_H,G4_He,G4_Li,G4_Be,G4_B,G4_C,G4_N,G4_O,G4_F,G4_Ne,G4_Na,G4_Mg,G4_Al,G4_Si,G4_P,G4_S,G4_Cl,G4_Ar,G4_K,G4_Ca,G4_Sc,G4_Ti,G4_V,G4_Cr,G4_Mn,G4_Fe,G4_Co,G4_Ni,G4_Cu,G4_Zn,G4_Ga,G4_Ge,G4_As,G4_Se,G4_Br,G4_Kr,G4_Rb,G4_Sr,G4_Y,G4_Zr,G4_Nb,G4_Mo,G4_Tc,G4_Ru,G4_Rh,G4_Pd,G4_Ag,G4_Cd,G4_In,G4_Sn,G4_Sb,G4_Te,G4_I,G4_Xe,G4_Cs,G4_Ba,G4_La,G4_Ce,G4_Pr,G4_Nd,G4_Pm,G4_Sm,G4_Eu,G4_Gd,G4_Tb,G4_Dy,G4_Ho,G4_Er,+30 more]
FEATURE [App::DocumentObjectGroupPython] H_element114  label="H_element : 063"  # scripted group (container) (typed FeaturePython)
  n = 2
  ref = H_element
FEATURE [App::DocumentObjectGroupPython] G4_lH2  # scripted group (container) (typed FeaturePython)
  Dunit = g/cm3
  Dvalue = 0.0708
  Group = -> [H_element114]
  conduct = 2
  density = 1
  expand = 3
  formula = G4_lH2
  name = G4_lH2
  specific = 4
FEATURE [App::DocumentObjectGroupPython] N_element049  label="N_element : 022"  # scripted group (container) (typed FeaturePython)
  n = 2
  ref = N_element
FEATURE [App::DocumentObjectGroupPython] G4_lN2  # scripted group (container) (typed FeaturePython)
  Dunit = g/cm3
  Dvalue = 0.807
  Group = -> [N_element049]
  conduct = 2
  density = 1
  expand = 3
  formula = G4_lN2
  name = G4_lN2
  specific = 4
FEATURE [App::DocumentObjectGroupPython] O_element106  label="O_element : 060"  # scripted group (container) (typed FeaturePython)
  n = 2
  ref = O_element
FEATURE [App::DocumentObjectGroupPython] G4_lO2  # scripted group (container) (typed FeaturePython)
  Dunit = g/cm3
  Dvalue = 1.141
  Group = -> [O_element106]
  conduct = 2
  density = 1
  expand = 3
  formula = G4_lO2
  name = G4_lO2
  specific = 4
FEATURE [App::DocumentObjectGroupPython] Ar  label="Ar : 1"  # scripted group (container) (typed FeaturePython)
  n = 1
  ref = Ar
FEATURE [App::DocumentObjectGroupPython] G4_lAr  # scripted group (container) (typed FeaturePython)
  Dunit = g/cm3
  Dvalue = 1.396
  Group = -> [Ar]
  conduct = 2
  density = 1
  expand = 3
  formula = G4_lAr
  name = G4_lAr
  specific = 4
FEATURE [App::DocumentObjectGroupPython] Br  label="Br : 1"  # scripted group (container) (typed FeaturePython)
  n = 1
  ref = Br
FEATURE [App::DocumentObjectGroupPython] G4_lBr  # scripted group (container) (typed FeaturePython)
  Dunit = g/cm3
  Dvalue = 3.1028
  Group = -> [Br]
  conduct = 2
  density = 1
  expand = 3
  formula = G4_lBr
  name = G4_lBr
  specific = 4
FEATURE [App::DocumentObjectGroupPython] Kr  label="Kr : 1"  # scripted group (container) (typed FeaturePython)
  n = 1
  ref = Kr
FEATURE [App::DocumentObjectGroupPython] G4_lKr  # scripted group (container) (typed FeaturePython)
  Dunit = g/cm3
  Dvalue = 2.418
  Group = -> [Kr]
  conduct = 2
  density = 1
  expand = 3
  formula = G4_lKr
  name = G4_lKr
  specific = 4
FEATURE [App::DocumentObjectGroupPython] Xe  label="Xe : 1"  # scripted group (container) (typed FeaturePython)
  n = 1
  ref = Xe
FEATURE [App::DocumentObjectGroupPython] G4_lXe  # scripted group (container) (typed FeaturePython)
  Dunit = g/cm3
  Dvalue = 2.953
  Group = -> [Xe]
  conduct = 2
  density = 1
  expand = 3
  formula = G4_lXe
  name = G4_lXe
  specific = 4
FEATURE [App::DocumentObjectGroupPython] O_element107  label="O_element : 061"  # scripted group (container) (typed FeaturePython)
  n = 4
  ref = O_element
FEATURE [App::DocumentObjectGroupPython] Pb_element004  label="Pb_element : 002"  # scripted group (container) (typed FeaturePython)
  n = 1
  ref = Pb_element
FEATURE [App::DocumentObjectGroupPython] W_element005  label="W_element : 005"  # scripted group (container) (typed FeaturePython)
  n = 1
  ref = W_element
FEATURE [App::DocumentObjectGroupPython] G4_PbWO4  # scripted group (container) (typed FeaturePython)
  Dunit = g/cm3
  Dvalue = 8.28
  Group = -> [O_element107,Pb_element004,W_element005]
  conduct = 2
  density = 1
  expand = 3
  formula = G4_PbWO4
  name = G4_PbWO4
  specific = 4
FEATURE [App::DocumentObjectGroupPython] alactic  label="alactic : 1"  # scripted group (container) (typed FeaturePython)
  n = 1
  ref = alactic
FEATURE [App::DocumentObjectGroupPython] G4_Galactic  # scripted group (container) (typed FeaturePython)
  Dunit = g/cm3
  Dvalue = 0
  Group = -> [alactic]
  conduct = 2
  density = 1
  expand = 3
  formula = G4_Galactic
  name = G4_Galactic
  specific = 4
FEATURE [App::DocumentObjectGroupPython] RAPHITE_POROUS  label="RAPHITE_POROUS : 1"  # scripted group (container) (typed FeaturePython)
  n = 1
  ref = RAPHITE_POROUS
FEATURE [App::DocumentObjectGroupPython] G4_GRAPHITE_POROUS  # scripted group (container) (typed FeaturePython)
  Dunit = g/cm3
  Dvalue = 1.7
  Group = -> [RAPHITE_POROUS]
  conduct = 2
  density = 1
  expand = 3
  formula = G4_GRAPHITE_POROUS
  name = G4_GRAPHITE_POROUS
  specific = 4
FEATURE [App::DocumentObjectGroupPython] H_element115  label="H_element : 0.150"  # scripted group (container) (typed FeaturePython)
  n = 0.080538
FEATURE [App::DocumentObjectGroupPython] C_element125  label="C_element : 0.600"  # scripted group (container) (typed FeaturePython)
  n = 0.599848
FEATURE [App::DocumentObjectGroupPython] O_element108  label="O_element : 0.320"  # scripted group (container) (typed FeaturePython)
  n = 0.319614
FEATURE [App::DocumentObjectGroupPython] G4_LUCITE  # scripted group (container) (typed FeaturePython)
  Dunit = g/cm3
  Dvalue = 1.19
  Group = -> [H_element115,C_element125,O_element108]
  conduct = 2
  density = 1
  expand = 3
  formula = G4_LUCITE
  name = G4_LUCITE
  specific = 4
FEATURE [App::DocumentObjectGroupPython] Cu_element002  label="Cu_element : 62"  # scripted group (container) (typed FeaturePython)
  n = 62
  ref = Cu_element
FEATURE [App::DocumentObjectGroupPython] Zn_element002  label="Zn_element : 35"  # scripted group (container) (typed FeaturePython)
  n = 35
  ref = Zn_element
FEATURE [App::DocumentObjectGroupPython] Pb_element005  label="Pb_element : 3"  # scripted group (container) (typed FeaturePython)
  n = 3
  ref = Pb_element
FEATURE [App::DocumentObjectGroupPython] G4_BRASS  # scripted group (container) (typed FeaturePython)
  Dunit = g/cm3
  Dvalue = 8.52
  Group = -> [Cu_element002,Zn_element002,Pb_element005]
  conduct = 2
  density = 1
  expand = 3
  formula = G4_BRASS
  name = G4_BRASS
  specific = 4
FEATURE [App::DocumentObjectGroupPython] Cu_element003  label="Cu_element : 89"  # scripted group (container) (typed FeaturePython)
  n = 89
  ref = Cu_element
FEATURE [App::DocumentObjectGroupPython] Zn_element003  label="Zn_element : 9"  # scripted group (container) (typed FeaturePython)
  n = 9
  ref = Zn_element
FEATURE [App::DocumentObjectGroupPython] Pb_element006  label="Pb_element : 2"  # scripted group (container) (typed FeaturePython)
  n = 2
  ref = Pb_element
FEATURE [App::DocumentObjectGroupPython] G4_BRONZE  # scripted group (container) (typed FeaturePython)
  Dunit = g/cm3
  Dvalue = 8.82
  Group = -> [Cu_element003,Zn_element003,Pb_element006]
  conduct = 2
  density = 1
  expand = 3
  formula = G4_BRONZE
  name = G4_BRONZE
  specific = 4
FEATURE [App::DocumentObjectGroupPython] Fe_element008  label="Fe_element : 74"  # scripted group (container) (typed FeaturePython)
  n = 74
  ref = Fe_element
FEATURE [App::DocumentObjectGroupPython] Cr_element002  label="Cr_element : 18"  # scripted group (container) (typed FeaturePython)
  n = 18
  ref = Cr_element
FEATURE [App::DocumentObjectGroupPython] Ni_element002  label="Ni_element : 8"  # scripted group (container) (typed FeaturePython)
  n = 8
  ref = Ni_element
FEATURE [App::DocumentObjectGroupPython] G4_STAINLESS_STEEL  label="G4_STAINLESS-STEEL"  # scripted group (container) (typed FeaturePython)
  Dunit = g/cm3
  Dvalue = 8
  Group = -> [Fe_element008,Cr_element002,Ni_element002]
  conduct = 2
  density = 1
  expand = 3
  formula = G4_STAINLESS-STEEL
  name = G4_STAINLESS-STEEL
  specific = 4
FEATURE [App::DocumentObjectGroupPython] H_element116  label="H_element : 064"  # scripted group (container) (typed FeaturePython)
  n = 18
  ref = H_element
FEATURE [App::DocumentObjectGroupPython] C_element126  label="C_element : 071"  # scripted group (container) (typed FeaturePython)
  n = 12
  ref = C_element
FEATURE [App::DocumentObjectGroupPython] O_element109  label="O_element : 062"  # scripted group (container) (typed FeaturePython)
  n = 7
  ref = O_element
FEATURE [App::DocumentObjectGroupPython] G4_CR39  # scripted group (container) (typed FeaturePython)
  Dunit = g/cm3
  Dvalue = 1.32
  Group = -> [H_element116,C_element126,O_element109]
  conduct = 2
  density = 1
  expand = 3
  formula = G4_CR39
  name = G4_CR39
  specific = 4
FEATURE [App::DocumentObjectGroupPython] H_element117  label="H_element : 38"  # scripted group (container) (typed FeaturePython)
  n = 38
  ref = H_element
FEATURE [App::DocumentObjectGroupPython] C_element127  label="C_element : 072"  # scripted group (container) (typed FeaturePython)
  n = 18
  ref = C_element
FEATURE [App::DocumentObjectGroupPython] O_element110  label="O_element : 063"  # scripted group (container) (typed FeaturePython)
  n = 1
  ref = O_element
FEATURE [App::DocumentObjectGroupPython] G4_OCTADECANOL  # scripted group (container) (typed FeaturePython)
  Dunit = g/cm3
  Dvalue = 0.812
  Group = -> [H_element117,C_element127,O_element110]
  conduct = 2
  density = 1
  expand = 3
  formula = G4_OCTADECANOL
  name = G4_OCTADECANOL
  specific = 4
FEATURE [App::DocumentObjectGroupPython] HEP  # scripted group (container) (typed FeaturePython)
  Group = -> [G4_lH2,G4_lN2,G4_lO2,G4_lAr,G4_lBr,G4_lKr,G4_lXe,G4_PbWO4,G4_Galactic,G4_GRAPHITE_POROUS,G4_LUCITE,G4_BRASS,G4_BRONZE,G4_STAINLESS_STEEL,G4_CR39,G4_OCTADECANOL]
FEATURE [App::DocumentObjectGroupPython] C_element128  label="C_element : 073"  # scripted group (container) (typed FeaturePython)
  n = 14
  ref = C_element
FEATURE [App::DocumentObjectGroupPython] H_element118  label="H_element : 065"  # scripted group (container) (typed FeaturePython)
  n = 10
  ref = H_element
FEATURE [App::DocumentObjectGroupPython] O_element111  label="O_element : 064"  # scripted group (container) (typed FeaturePython)
  n = 2
  ref = O_element
FEATURE [App::DocumentObjectGroupPython] N_element050  label="N_element : 023"  # scripted group (container) (typed FeaturePython)
  n = 2
  ref = N_element
FEATURE [App::DocumentObjectGroupPython] G4_KEVLAR  # scripted group (container) (typed FeaturePython)
  Dunit = g/cm3
  Dvalue = 1.44
  Group = -> [C_element128,H_element118,O_element111,N_element050]
  conduct = 2
  density = 1
  expand = 3
  formula = G4_KEVLAR
  name = G4_KEVLAR
  specific = 4
FEATURE [App::DocumentObjectGroupPython] C_element129  label="C_element : 074"  # scripted group (container) (typed FeaturePython)
  n = 10
  ref = C_element
FEATURE [App::DocumentObjectGroupPython] H_element119  label="H_element : 066"  # scripted group (container) (typed FeaturePython)
  n = 8
  ref = H_element
FEATURE [App::DocumentObjectGroupPython] O_element112  label="O_element : 065"  # scripted group (container) (typed FeaturePython)
  n = 4
  ref = O_element
FEATURE [App::DocumentObjectGroupPython] G4_DACRON  # scripted group (container) (typed FeaturePython)
  Dunit = g/cm3
  Dvalue = 1.4
  Group = -> [C_element129,H_element119,O_element112]
  conduct = 2
  density = 1
  expand = 3
  formula = G4_DACRON
  name = G4_DACRON
  specific = 4
FEATURE [App::DocumentObjectGroupPython] C_element130  label="C_element : 075"  # scripted group (container) (typed FeaturePython)
  n = 4
  ref = C_element
FEATURE [App::DocumentObjectGroupPython] H_element120  label="H_element : 067"  # scripted group (container) (typed FeaturePython)
  n = 5
  ref = H_element
FEATURE [App::DocumentObjectGroupPython] Cl_element030  label="Cl_element : 016"  # scripted group (container) (typed FeaturePython)
  n = 1
  ref = Cl_element
FEATURE [App::DocumentObjectGroupPython] G4_NEOPRENE  # scripted group (container) (typed FeaturePython)
  Dunit = g/cm3
  Dvalue = 1.23
  Group = -> [C_element130,H_element120,Cl_element030]
  conduct = 2
  density = 1
  expand = 3
  formula = G4_NEOPRENE
  name = G4_NEOPRENE
  specific = 4
FEATURE [App::DocumentObjectGroupPython] Space  # scripted group (container) (typed FeaturePython)
  Group = -> [G4_KEVLAR,G4_DACRON,G4_NEOPRENE]
FEATURE [App::DocumentObjectGroupPython] H_element121  label="H_element : 068"  # scripted group (container) (typed FeaturePython)
  n = 5
  ref = H_element
FEATURE [App::DocumentObjectGroupPython] C_element131  label="C_element : 076"  # scripted group (container) (typed FeaturePython)
  n = 4
  ref = C_element
FEATURE [App::DocumentObjectGroupPython] N_element051  label="N_element : 3"  # scripted group (container) (typed FeaturePython)
  n = 3
  ref = N_element
FEATURE [App::DocumentObjectGroupPython] O_element113  label="O_element : 066"  # scripted group (container) (typed FeaturePython)
  n = 1
  ref = O_element
FEATURE [App::DocumentObjectGroupPython] G4_CYTOSINE  # scripted group (container) (typed FeaturePython)
  Dunit = g/cm3
  Dvalue = 1.55
  Group = -> [H_element121,C_element131,N_element051,O_element113]
  conduct = 2
  density = 1
  expand = 3
  formula = G4_CYTOSINE
  name = G4_CYTOSINE
  specific = 4
FEATURE [App::DocumentObjectGroupPython] H_element122  label="H_element : 069"  # scripted group (container) (typed FeaturePython)
  n = 6
  ref = H_element
FEATURE [App::DocumentObjectGroupPython] C_element132  label="C_element : 077"  # scripted group (container) (typed FeaturePython)
  n = 5
  ref = C_element
FEATURE [App::DocumentObjectGroupPython] N_element052  label="N_element : 024"  # scripted group (container) (typed FeaturePython)
  n = 2
  ref = N_element
FEATURE [App::DocumentObjectGroupPython] O_element114  label="O_element : 067"  # scripted group (container) (typed FeaturePython)
  n = 2
  ref = O_element
FEATURE [App::DocumentObjectGroupPython] G4_THYMINE  # scripted group (container) (typed FeaturePython)
  Dunit = g/cm3
  Dvalue = 1.23
  Group = -> [H_element122,C_element132,N_element052,O_element114]
  conduct = 2
  density = 1
  expand = 3
  formula = G4_THYMINE
  name = G4_THYMINE
  specific = 4
FEATURE [App::DocumentObjectGroupPython] H_element123  label="H_element : 070"  # scripted group (container) (typed FeaturePython)
  n = 4
  ref = H_element
FEATURE [App::DocumentObjectGroupPython] C_element133  label="C_element : 078"  # scripted group (container) (typed FeaturePython)
  n = 4
  ref = C_element
FEATURE [App::DocumentObjectGroupPython] N_element053  label="N_element : 025"  # scripted group (container) (typed FeaturePython)
  n = 2
  ref = N_element
FEATURE [App::DocumentObjectGroupPython] O_element115  label="O_element : 068"  # scripted group (container) (typed FeaturePython)
  n = 2
  ref = O_element
FEATURE [App::DocumentObjectGroupPython] G4_URACIL  # scripted group (container) (typed FeaturePython)
  Dunit = g/cm3
  Dvalue = 1.32
  Group = -> [H_element123,C_element133,N_element053,O_element115]
  conduct = 2
  density = 1
  expand = 3
  formula = G4_URACIL
  name = G4_URACIL
  specific = 4
FEATURE [App::DocumentObjectGroupPython] H_element124  label="H_element : 071"  # scripted group (container) (typed FeaturePython)
  n = 4
  ref = H_element
FEATURE [App::DocumentObjectGroupPython] C_element134  label="C_element : 079"  # scripted group (container) (typed FeaturePython)
  n = 5
  ref = C_element
FEATURE [App::DocumentObjectGroupPython] N_element054  label="N_element : 026"  # scripted group (container) (typed FeaturePython)
  n = 5
  ref = N_element
FEATURE [App::DocumentObjectGroupPython] G4_DNA_ADENINE  # scripted group (container) (typed FeaturePython)
  Dunit = g/cm3
  Dvalue = 1
  Group = -> [H_element124,C_element134,N_element054]
  conduct = 2
  density = 1
  expand = 3
  formula = G4_DNA_ADENINE
  name = G4_DNA_ADENINE
  specific = 4
FEATURE [App::DocumentObjectGroupPython] H_element125  label="H_element : 072"  # scripted group (container) (typed FeaturePython)
  n = 4
  ref = H_element
FEATURE [App::DocumentObjectGroupPython] C_element135  label="C_element : 080"  # scripted group (container) (typed FeaturePython)
  n = 5
  ref = C_element
FEATURE [App::DocumentObjectGroupPython] N_element055  label="N_element : 027"  # scripted group (container) (typed FeaturePython)
  n = 5
  ref = N_element
FEATURE [App::DocumentObjectGroupPython] O_element116  label="O_element : 069"  # scripted group (container) (typed FeaturePython)
  n = 1
  ref = O_element
FEATURE [App::DocumentObjectGroupPython] G4_DNA_GUANINE  # scripted group (container) (typed FeaturePython)
  Dunit = g/cm3
  Dvalue = 1
  Group = -> [H_element125,C_element135,N_element055,O_element116]
  conduct = 2
  density = 1
  expand = 3
  formula = G4_DNA_GUANINE
  name = G4_DNA_GUANINE
  specific = 4
FEATURE [App::DocumentObjectGroupPython] H_element126  label="H_element : 073"  # scripted group (container) (typed FeaturePython)
  n = 4
  ref = H_element
FEATURE [App::DocumentObjectGroupPython] C_element136  label="C_element : 081"  # scripted group (container) (typed FeaturePython)
  n = 4
  ref = C_element
FEATURE [App::DocumentObjectGroupPython] N_element056  label="N_element : 028"  # scripted group (container) (typed FeaturePython)
  n = 3
  ref = N_element
FEATURE [App::DocumentObjectGroupPython] O_element117  label="O_element : 070"  # scripted group (container) (typed FeaturePython)
  n = 1
  ref = O_element
FEATURE [App::DocumentObjectGroupPython] G4_DNA_CYTOSINE  # scripted group (container) (typed FeaturePython)
  Dunit = g/cm3
  Dvalue = 1
  Group = -> [H_element126,C_element136,N_element056,O_element117]
  conduct = 2
  density = 1
  expand = 3
  formula = G4_DNA_CYTOSINE
  name = G4_DNA_CYTOSINE
  specific = 4
FEATURE [App::DocumentObjectGroupPython] H_element127  label="H_element : 074"  # scripted group (container) (typed FeaturePython)
  n = 5
  ref = H_element
FEATURE [App::DocumentObjectGroupPython] C_element137  label="C_element : 082"  # scripted group (container) (typed FeaturePython)
  n = 5
  ref = C_element
FEATURE [App::DocumentObjectGroupPython] N_element057  label="N_element : 029"  # scripted group (container) (typed FeaturePython)
  n = 2
  ref = N_element
FEATURE [App::DocumentObjectGroupPython] O_element118  label="O_element : 071"  # scripted group (container) (typed FeaturePython)
  n = 2
  ref = O_element
FEATURE [App::DocumentObjectGroupPython] G4_DNA_THYMINE  # scripted group (container) (typed FeaturePython)
  Dunit = g/cm3
  Dvalue = 1
  Group = -> [H_element127,C_element137,N_element057,O_element118]
  conduct = 2
  density = 1
  expand = 3
  formula = G4_DNA_THYMINE
  name = G4_DNA_THYMINE
  specific = 4
FEATURE [App::DocumentObjectGroupPython] H_element128  label="H_element : 075"  # scripted group (container) (typed FeaturePython)
  n = 3
  ref = H_element
FEATURE [App::DocumentObjectGroupPython] C_element138  label="C_element : 083"  # scripted group (container) (typed FeaturePython)
  n = 4
  ref = C_element
FEATURE [App::DocumentObjectGroupPython] N_element058  label="N_element : 030"  # scripted group (container) (typed FeaturePython)
  n = 2
  ref = N_element
FEATURE [App::DocumentObjectGroupPython] O_element119  label="O_element : 072"  # scripted group (container) (typed FeaturePython)
  n = 2
  ref = O_element
FEATURE [App::DocumentObjectGroupPython] G4_DNA_URACIL  # scripted group (container) (typed FeaturePython)
  Dunit = g/cm3
  Dvalue = 1
  Group = -> [H_element128,C_element138,N_element058,O_element119]
  conduct = 2
  density = 1
  expand = 3
  formula = G4_DNA_URACIL
  name = G4_DNA_URACIL
  specific = 4
FEATURE [App::DocumentObjectGroupPython] H_element129  label="H_element : 076"  # scripted group (container) (typed FeaturePython)
  n = 10
  ref = H_element
FEATURE [App::DocumentObjectGroupPython] C_element139  label="C_element : 084"  # scripted group (container) (typed FeaturePython)
  n = 10
  ref = C_element
FEATURE [App::DocumentObjectGroupPython] N_element059  label="N_element : 031"  # scripted group (container) (typed FeaturePython)
  n = 5
  ref = N_element
FEATURE [App::DocumentObjectGroupPython] O_element120  label="O_element : 073"  # scripted group (container) (typed FeaturePython)
  n = 4
  ref = O_element
FEATURE [App::DocumentObjectGroupPython] G4_DNA_ADENOSINE  # scripted group (container) (typed FeaturePython)
  Dunit = g/cm3
  Dvalue = 1
  Group = -> [H_element129,C_element139,N_element059,O_element120]
  conduct = 2
  density = 1
  expand = 3
  formula = G4_DNA_ADENOSINE
  name = G4_DNA_ADENOSINE
  specific = 4
FEATURE [App::DocumentObjectGroupPython] H_element130  label="H_element : 077"  # scripted group (container) (typed FeaturePython)
  n = 10
  ref = H_element
FEATURE [App::DocumentObjectGroupPython] C_element140  label="C_element : 085"  # scripted group (container) (typed FeaturePython)
  n = 10
  ref = C_element
FEATURE [App::DocumentObjectGroupPython] N_element060  label="N_element : 032"  # scripted group (container) (typed FeaturePython)
  n = 5
  ref = N_element
FEATURE [App::DocumentObjectGroupPython] O_element121  label="O_element : 074"  # scripted group (container) (typed FeaturePython)
  n = 5
  ref = O_element
FEATURE [App::DocumentObjectGroupPython] G4_DNA_GUANOSINE  # scripted group (container) (typed FeaturePython)
  Dunit = g/cm3
  Dvalue = 1
  Group = -> [H_element130,C_element140,N_element060,O_element121]
  conduct = 2
  density = 1
  expand = 3
  formula = G4_DNA_GUANOSINE
  name = G4_DNA_GUANOSINE
  specific = 4
FEATURE [App::DocumentObjectGroupPython] H_element131  label="H_element : 078"  # scripted group (container) (typed FeaturePython)
  n = 10
  ref = H_element
FEATURE [App::DocumentObjectGroupPython] C_element141  label="C_element : 086"  # scripted group (container) (typed FeaturePython)
  n = 9
  ref = C_element
FEATURE [App::DocumentObjectGroupPython] N_element061  label="N_element : 033"  # scripted group (container) (typed FeaturePython)
  n = 3
  ref = N_element
FEATURE [App::DocumentObjectGroupPython] O_element122  label="O_element : 075"  # scripted group (container) (typed FeaturePython)
  n = 5
  ref = O_element
FEATURE [App::DocumentObjectGroupPython] G4_DNA_CYTIDINE  # scripted group (container) (typed FeaturePython)
  Dunit = g/cm3
  Dvalue = 1
  Group = -> [H_element131,C_element141,N_element061,O_element122]
  conduct = 2
  density = 1
  expand = 3
  formula = G4_DNA_CYTIDINE
  name = G4_DNA_CYTIDINE
  specific = 4
FEATURE [App::DocumentObjectGroupPython] H_element132  label="H_element : 079"  # scripted group (container) (typed FeaturePython)
  n = 9
  ref = H_element
FEATURE [App::DocumentObjectGroupPython] C_element142  label="C_element : 087"  # scripted group (container) (typed FeaturePython)
  n = 9
  ref = C_element
FEATURE [App::DocumentObjectGroupPython] N_element062  label="N_element : 034"  # scripted group (container) (typed FeaturePython)
  n = 2
  ref = N_element
FEATURE [App::DocumentObjectGroupPython] O_element123  label="O_element : 076"  # scripted group (container) (typed FeaturePython)
  n = 6
  ref = O_element
FEATURE [App::DocumentObjectGroupPython] G4_DNA_URIDINE  # scripted group (container) (typed FeaturePython)
  Dunit = g/cm3
  Dvalue = 1
  Group = -> [H_element132,C_element142,N_element062,O_element123]
  conduct = 2
  density = 1
  expand = 3
  formula = G4_DNA_URIDINE
  name = G4_DNA_URIDINE
  specific = 4
FEATURE [App::DocumentObjectGroupPython] H_element133  label="H_element : 080"  # scripted group (container) (typed FeaturePython)
  n = 11
  ref = H_element
FEATURE [App::DocumentObjectGroupPython] C_element143  label="C_element : 088"  # scripted group (container) (typed FeaturePython)
  n = 10
  ref = C_element
FEATURE [App::DocumentObjectGroupPython] N_element063  label="N_element : 035"  # scripted group (container) (typed FeaturePython)
  n = 2
  ref = N_element
FEATURE [App::DocumentObjectGroupPython] O_element124  label="O_element : 077"  # scripted group (container) (typed FeaturePython)
  n = 6
  ref = O_element
FEATURE [App::DocumentObjectGroupPython] G4_DNA_METHYLURIDINE  # scripted group (container) (typed FeaturePython)
  Dunit = g/cm3
  Dvalue = 1
  Group = -> [H_element133,C_element143,N_element063,O_element124]
  conduct = 2
  density = 1
  expand = 3
  formula = G4_DNA_METHYLURIDINE
  name = G4_DNA_METHYLURIDINE
  specific = 4
FEATURE [App::DocumentObjectGroupPython] P_element014  label="P_element : 003"  # scripted group (container) (typed FeaturePython)
  n = 1
  ref = P_element
FEATURE [App::DocumentObjectGroupPython] O_element125  label="O_element : 078"  # scripted group (container) (typed FeaturePython)
  n = 3
  ref = O_element
FEATURE [App::DocumentObjectGroupPython] G4_DNA_MONOPHOSPHATE  # scripted group (container) (typed FeaturePython)
  Dunit = g/cm3
  Dvalue = 1
  Group = -> [P_element014,O_element125]
  conduct = 2
  density = 1
  expand = 3
  formula = G4_DNA_MONOPHOSPHATE
  name = G4_DNA_MONOPHOSPHATE
  specific = 4
FEATURE [App::DocumentObjectGroupPython] H_element134  label="H_element : 081"  # scripted group (container) (typed FeaturePython)
  n = 10
  ref = H_element
FEATURE [App::DocumentObjectGroupPython] C_element144  label="C_element : 089"  # scripted group (container) (typed FeaturePython)
  n = 10
  ref = C_element
FEATURE [App::DocumentObjectGroupPython] N_element064  label="N_element : 036"  # scripted group (container) (typed FeaturePython)
  n = 5
  ref = N_element
FEATURE [App::DocumentObjectGroupPython] O_element126  label="O_element : 079"  # scripted group (container) (typed FeaturePython)
  n = 7
  ref = O_element
FEATURE [App::DocumentObjectGroupPython] P_element015  label="P_element : 004"  # scripted group (container) (typed FeaturePython)
  n = 1
  ref = P_element
FEATURE [App::DocumentObjectGroupPython] G4_DNA_A  # scripted group (container) (typed FeaturePython)
  Dunit = g/cm3
  Dvalue = 1
  Group = -> [H_element134,C_element144,N_element064,O_element126,P_element015]
  conduct = 2
  density = 1
  expand = 3
  formula = G4_DNA_A
  name = G4_DNA_A
  specific = 4
FEATURE [App::DocumentObjectGroupPython] H_element135  label="H_element : 082"  # scripted group (container) (typed FeaturePython)
  n = 10
  ref = H_element
FEATURE [App::DocumentObjectGroupPython] C_element145  label="C_element : 090"  # scripted group (container) (typed FeaturePython)
  n = 10
  ref = C_element
FEATURE [App::DocumentObjectGroupPython] N_element065  label="N_element : 037"  # scripted group (container) (typed FeaturePython)
  n = 5
  ref = N_element
FEATURE [App::DocumentObjectGroupPython] O_element127  label="O_element : 8"  # scripted group (container) (typed FeaturePython)
  n = 8
  ref = O_element
FEATURE [App::DocumentObjectGroupPython] P_element016  label="P_element : 005"  # scripted group (container) (typed FeaturePython)
  n = 1
  ref = P_element
FEATURE [App::DocumentObjectGroupPython] G4_DNA_G  # scripted group (container) (typed FeaturePython)
  Dunit = g/cm3
  Dvalue = 1
  Group = -> [H_element135,C_element145,N_element065,O_element127,P_element016]
  conduct = 2
  density = 1
  expand = 3
  formula = G4_DNA_G
  name = G4_DNA_G
  specific = 4
FEATURE [App::DocumentObjectGroupPython] H_element136  label="H_element : 083"  # scripted group (container) (typed FeaturePython)
  n = 10
  ref = H_element
FEATURE [App::DocumentObjectGroupPython] C_element146  label="C_element : 091"  # scripted group (container) (typed FeaturePython)
  n = 9
  ref = C_element
FEATURE [App::DocumentObjectGroupPython] N_element066  label="N_element : 038"  # scripted group (container) (typed FeaturePython)
  n = 3
  ref = N_element
FEATURE [App::DocumentObjectGroupPython] O_element128  label="O_element : 080"  # scripted group (container) (typed FeaturePython)
  n = 8
  ref = O_element
FEATURE [App::DocumentObjectGroupPython] P_element017  label="P_element : 006"  # scripted group (container) (typed FeaturePython)
  n = 1
  ref = P_element
FEATURE [App::DocumentObjectGroupPython] G4_DNA_C  # scripted group (container) (typed FeaturePython)
  Dunit = g/cm3
  Dvalue = 1
  Group = -> [H_element136,C_element146,N_element066,O_element128,P_element017]
  conduct = 2
  density = 1
  expand = 3
  formula = G4_DNA_C
  name = G4_DNA_C
  specific = 4
FEATURE [App::DocumentObjectGroupPython] H_element137  label="H_element : 084"  # scripted group (container) (typed FeaturePython)
  n = 9
  ref = H_element
FEATURE [App::DocumentObjectGroupPython] C_element147  label="C_element : 092"  # scripted group (container) (typed FeaturePython)
  n = 9
  ref = C_element
FEATURE [App::DocumentObjectGroupPython] N_element067  label="N_element : 039"  # scripted group (container) (typed FeaturePython)
  n = 2
  ref = N_element
FEATURE [App::DocumentObjectGroupPython] O_element129  label="O_element : 9"  # scripted group (container) (typed FeaturePython)
  n = 9
  ref = O_element
FEATURE [App::DocumentObjectGroupPython] P_element018  label="P_element : 007"  # scripted group (container) (typed FeaturePython)
  n = 1
  ref = P_element
FEATURE [App::DocumentObjectGroupPython] G4_DNA_U  # scripted group (container) (typed FeaturePython)
  Dunit = g/cm3
  Dvalue = 1
  Group = -> [H_element137,C_element147,N_element067,O_element129,P_element018]
  conduct = 2
  density = 1
  expand = 3
  formula = G4_DNA_U
  name = G4_DNA_U
  specific = 4
FEATURE [App::DocumentObjectGroupPython] H_element138  label="H_element : 085"  # scripted group (container) (typed FeaturePython)
  n = 11
  ref = H_element
FEATURE [App::DocumentObjectGroupPython] C_element148  label="C_element : 093"  # scripted group (container) (typed FeaturePython)
  n = 10
  ref = C_element
FEATURE [App::DocumentObjectGroupPython] N_element068  label="N_element : 040"  # scripted group (container) (typed FeaturePython)
  n = 2
  ref = N_element
FEATURE [App::DocumentObjectGroupPython] O_element130  label="O_element : 081"  # scripted group (container) (typed FeaturePython)
  n = 9
  ref = O_element
FEATURE [App::DocumentObjectGroupPython] P_element019  label="P_element : 008"  # scripted group (container) (typed FeaturePython)
  n = 1
  ref = P_element
FEATURE [App::DocumentObjectGroupPython] G4_DNA_MU  # scripted group (container) (typed FeaturePython)
  Dunit = g/cm3
  Dvalue = 1
  Group = -> [H_element138,C_element148,N_element068,O_element130,P_element019]
  conduct = 2
  density = 1
  expand = 3
  formula = G4_DNA_MU
  name = G4_DNA_MU
  specific = 4
FEATURE [App::DocumentObjectGroupPython] BioChemical  # scripted group (container) (typed FeaturePython)
  Group = -> [G4_CYTOSINE,G4_THYMINE,G4_URACIL,G4_DNA_ADENINE,G4_DNA_GUANINE,G4_DNA_CYTOSINE,G4_DNA_THYMINE,G4_DNA_URACIL,G4_DNA_ADENOSINE,G4_DNA_GUANOSINE,G4_DNA_CYTIDINE,G4_DNA_URIDINE,G4_DNA_METHYLURIDINE,G4_DNA_MONOPHOSPHATE,G4_DNA_A,G4_DNA_G,G4_DNA_C,G4_DNA_U,G4_DNA_MU]
FEATURE [App::DocumentObjectGroupPython] G4Materials  # scripted group (container) (typed FeaturePython)
  Group = -> [NIST,Element,HEP,Space,BioChemical]
  version = 1
FEATURE [App::DocumentObjectGroupPython] Geant4  # scripted group (container) (typed FeaturePython)
  Group = -> [G4Isotopes,G4Elements,G4Materials]
FEATURE [App::DocumentObjectGroupPython] Materials  # scripted group (container) (typed FeaturePython)
  Group = -> [Geant4]
FEATURE [Part::FeaturePython] GDMLBox_WorldBox  # WARN: FeaturePython — macro-defined, semantics opaque (R4)
  lunit = 2
  material = 5
  x = 600
  y = 600
  z = 600
FEATURE [Part::FeaturePython] GDMLSphere_Sphere  # WARN: FeaturePython — macro-defined, semantics opaque (R4)
  Placement = pos=(20,0,0) rot=(0,0,1;0rad)
  aunit = 0
  deltaphi = 2.02
  deltatheta = 2.02
  lunit = 2
  material = 18
  rmax = 20
  rmin = 10
  startphi = 0
  starttheta = 0
FEATURE [Part::FeaturePython] GDMLTorus_Torus  # WARN: FeaturePython — macro-defined, semantics opaque (R4)
  aunit = deg
  deltaphi = 360
  lunit = 2
  material = 5
  rmax = 5
  rmin = 0
  rtor = 10
  startphi = 10
FEATURE [Part::MultiFuse] Fusion
  Shapes = -> [GDMLSphere_Sphere,GDMLTorus_Torus]
  material = 18
FEATURE [Part::FeaturePython] Array  # Draft array (typed FeaturePython)
  Angle = 360
  ArrayType = 0
  Axis = (0,0,1)
  Base = -> Fusion
  Center = (0,0,0)
  Count = 4
  Fuse = false
  IntervalAxis = (0,0,0)
  IntervalX = (100,0,0)
  IntervalY = (0,100,0)
  IntervalZ = (0,0,100)
  NumberCircles = 3
  NumberPolar = 5
  NumberX = 2
  NumberY = 2
  NumberZ = 1
  Placement = pos=(-76.5,-45,0) rot=(0,0,1;0rad)
  RadialDistance = 50
  Symmetry = 1
  TangentialDistance = 25
FEATURE [Part::FeaturePython] Clone  label="Array001"  # Draft clone (typed FeaturePython)
  AttacherType = Attacher::AttachEngine3D
  Fuse = false
  Objects = -> [Array]
  Placement = pos=(-76.5,-45,0) rot=(0,0,1;0rad)
  Scale = (2.5,1,1)
  material = 18
FEATURE [App::Part] Part
  Group = -> [Clone]
  Origin = -> Origin001
FEATURE [App::Part] worldVOL
  Group = -> [GDMLBox_WorldBox,Part]
  Origin = -> Origin
